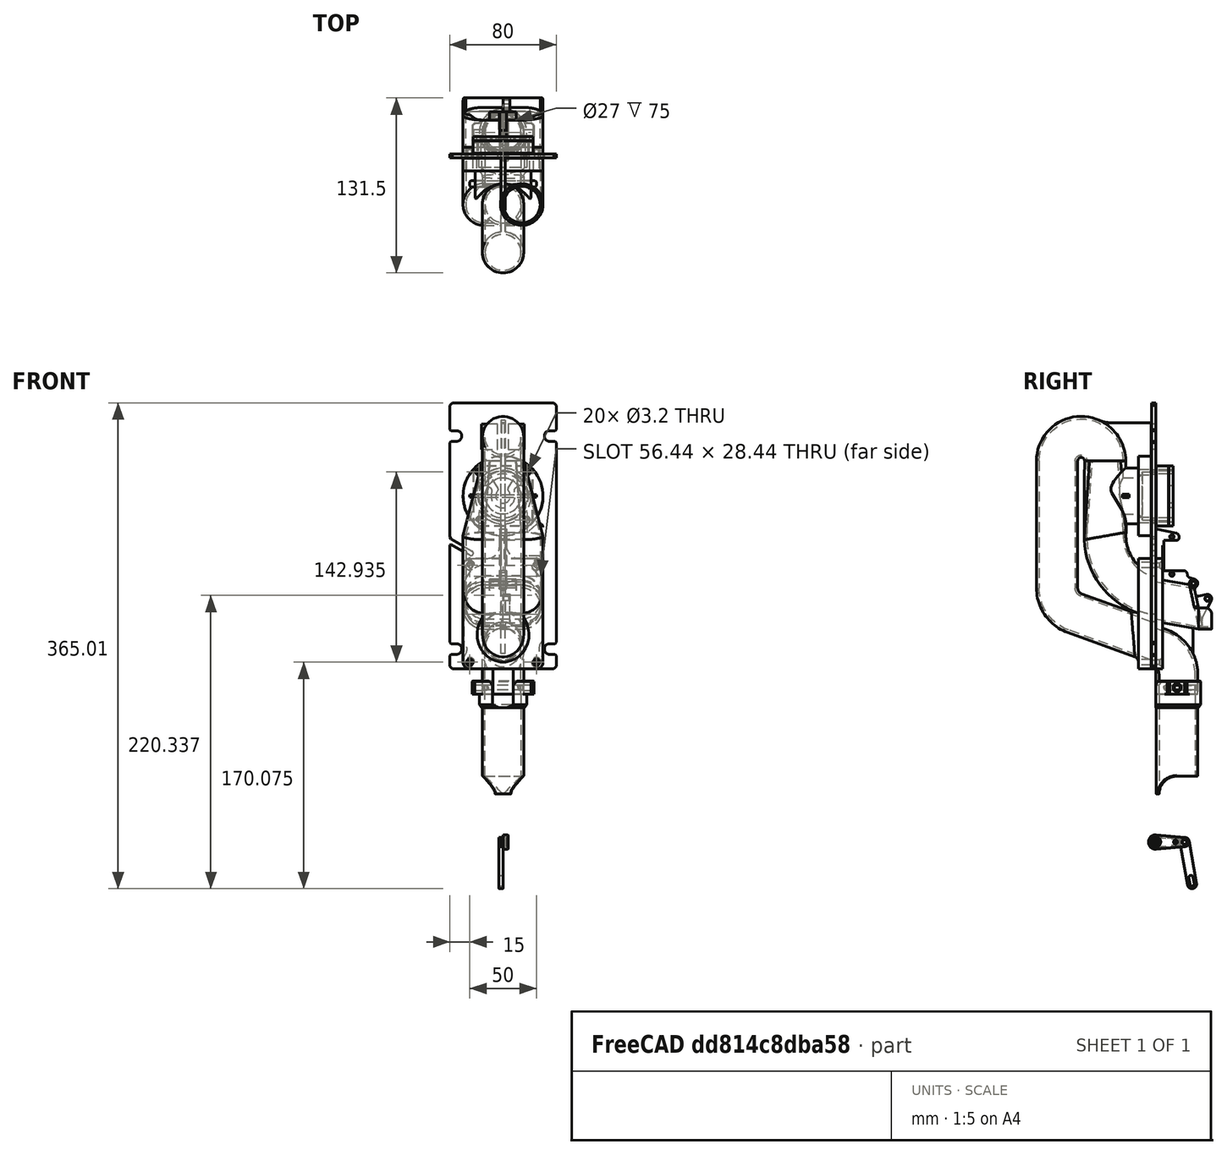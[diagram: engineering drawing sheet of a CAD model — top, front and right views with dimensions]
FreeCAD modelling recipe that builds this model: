
FCSTD DOCUMENT  (FreeCAD 2022.1128R26244 +5318 (Git))
Label: vacuum-ball
License: Creative Commons Attribution-NoDerivatives
LicenseURL: http://creativecommons.org/licenses/by-nd/4.0/
objects: Sketcher::SketchObject×58, PartDesign::Pad×27, PartDesign::Pocket×26, PartDesign::Chamfer×20, PartDesign::Fillet×20, PartDesign::Body×11, PartDesign::SubShapeBinder×9, PartDesign::SubtractivePipe×5, Part::SubShapeBinder×4, PartDesign::AdditivePipe×4, TechDraw::DrawSVGTemplate×4, TechDraw::DrawProjGroupItem×4, TechDraw::DrawProjGroup×4, TechDraw::DrawPage×4, App::Part×3, App::DocumentObjectGroup×2, PartDesign::AdditiveLoft×1, PartDesign::Line×1, PartDesign::Groove×1, PartDesign::Plane×1, +2 more types
note: 454 computed .brp shape members not serialized (recipe doc carries the construction recipe); baked Part::Feature solids carry a one-line shape summary decoded from their .brp
EXTERNAL_REF file=../table.FCStd obj=Group

FEATURE [Sketcher::SketchObject] Sketch038
  ArcFitTolerance = 1e-06
  AttachmentSupport = -> [XZ_Plane005]
  ExternalBSplineMaxDegree = 5
  ExternalBSplineTolerance = 0.0001
  FullyConstrained = true
  InternalTolerance = 1e-06
  MakeInternals = true
  MapMode = 5
  Placement = pos=(0,0,0) rot=(1,0,0;1.5708rad)
  Support = -> [XZ_Plane005]
  TreeRank = 208
  sketch-geometry (5):
    g0: LineSegment StartX=-40 StartY=130 StartZ=0 EndX=-40 EndY=330 EndZ=0
    g1: LineSegment StartX=-40 StartY=330 StartZ=0 EndX=40 EndY=330 EndZ=0
    g2: LineSegment StartX=40 StartY=330 StartZ=0 EndX=40 EndY=130 EndZ=0
    g3: LineSegment StartX=40 StartY=130 StartZ=0 EndX=-40 EndY=130 EndZ=0
    g4: GeomPoint [constr] X=2.444e-12 Y=230 Z=0
  constraints (13):
    c: Coincident(g0,g1)
    c: Coincident(g1,g2)
    c: Coincident(g2,g3)
    c: Coincident(g3,g0)
    c: Horizontal(g1)
    c: Horizontal(g3)
    c: Vertical(g0)
    c: Vertical(g2)
    c: Symmetric(g1,g0,g4)
    c: PointOnObject(g4,g-2)
    c: DistanceX(g1,g1) = 80
    c: DistanceY(g0,g0) = 200
    c: DistanceY(g-1,g0) = 130
FEATURE [PartDesign::Pad] Pad010
  AddSubType = 0
  AlongSketchNormal = false
  AutoTaperInnerAngle = true
  CheckUpToFaceLimits = true
  ClaimChildren = false
  Direction = (0,-1,2e-16)
  Fit = 0
  FitJoin = 0
  InnerFit = 0
  InnerFitJoin = 0
  Length = 3
  Length2 = 100
  Linearize = true
  NewSolid = false
  Profile = -> Sketch038
  Refine = true
  Suppress = false
  TaperInnerAngle = 0
  TaperInnerAngleRev = 0
  TreeRank = 209
  Type = 0
  _ProfileBasedVersion = 1
FEATURE [Sketcher::SketchObject] Sketch039
  ArcFitTolerance = 1e-06
  AttachmentSupport = -> [XZ_Plane005]
  ExternalBSplineMaxDegree = 5
  ExternalBSplineTolerance = 0.0001
  ExternalGeometry = -> [Pad010]
  FullyConstrained = true
  InternalTolerance = 1e-06
  MakeInternals = true
  MapMode = 5
  Placement = pos=(0,0,0) rot=(1,0,0;1.5708rad)
  Support = -> [XZ_Plane005]
  TreeRank = 211
  sketch-geometry (16):
    g0: ArcOfCircle CenterX=40 CenterY=305 CenterZ=0 NormalX=0 NormalY=0 NormalZ=1 AngleXU=0 Radius=4 StartAngle=4.71239 EndAngle=7.85398
    g1: ArcOfCircle CenterX=35 CenterY=305 CenterZ=0 NormalX=0 NormalY=0 NormalZ=1 AngleXU=0 Radius=4 StartAngle=1.5708 EndAngle=4.71239
    g2: LineSegment StartX=40 StartY=309 StartZ=0 EndX=35 EndY=309 EndZ=0
    g3: LineSegment StartX=35 StartY=301 StartZ=0 EndX=40 EndY=301 EndZ=0
    g4: ArcOfCircle CenterX=-40 CenterY=305 CenterZ=0 NormalX=0 NormalY=0 NormalZ=1 AngleXU=0 Radius=4 StartAngle=1.5708 EndAngle=4.71239
    g5: ArcOfCircle CenterX=-35 CenterY=305 CenterZ=0 NormalX=0 NormalY=0 NormalZ=1 AngleXU=0 Radius=4 StartAngle=4.71239 EndAngle=7.85398
    g6: LineSegment StartX=-40 StartY=301 StartZ=0 EndX=-35 EndY=301 EndZ=0
    g7: LineSegment StartX=-35 StartY=309 StartZ=0 EndX=-40 EndY=309 EndZ=0
    g8: ArcOfCircle CenterX=-40 CenterY=145 CenterZ=0 NormalX=0 NormalY=0 NormalZ=1 AngleXU=0 Radius=4 StartAngle=1.5708 EndAngle=4.71239
    g9: ArcOfCircle CenterX=-35 CenterY=145 CenterZ=0 NormalX=0 NormalY=0 NormalZ=1 AngleXU=0 Radius=4 StartAngle=4.71239 EndAngle=7.85398
    g10: LineSegment StartX=-40 StartY=141 StartZ=0 EndX=-35 EndY=141 EndZ=0
    g11: LineSegment StartX=-35 StartY=149 StartZ=0 EndX=-40 EndY=149 EndZ=0
    g12: ArcOfCircle CenterX=40 CenterY=145 CenterZ=0 NormalX=0 NormalY=0 NormalZ=1 AngleXU=0 Radius=4 StartAngle=4.71239 EndAngle=7.85398
    g13: ArcOfCircle CenterX=35 CenterY=145 CenterZ=0 NormalX=0 NormalY=0 NormalZ=1 AngleXU=0 Radius=4 StartAngle=1.5708 EndAngle=4.71239
    g14: LineSegment StartX=40 StartY=149 StartZ=0 EndX=35 EndY=149 EndZ=0
    g15: LineSegment StartX=35 StartY=141 StartZ=0 EndX=40 EndY=141 EndZ=0
  constraints (38):
    c: Tangent(g0,g2) = -1.5708
    c: Tangent(g2,g1) = -1.5708
    c: Tangent(g1,g3) = -1.5708
    c: Tangent(g3,g0) = -1.5708
    c: Equal(g0,g1)
    c: PointOnObject(g0,g-4)
    c: Tangent(g4,g6) = -1.5708
    c: Tangent(g6,g5) = -1.5708
    c: Tangent(g5,g7) = -1.5708
    c: Tangent(g7,g4) = -1.5708
    c: Equal(g4,g5)
    c: PointOnObject(g4,g-3)
    c: Tangent(g8,g10) = -1.5708
    c: Tangent(g10,g9) = -1.5708
    c: Tangent(g9,g11) = -1.5708
    c: Tangent(g11,g8) = -1.5708
    c: Equal(g8,g9)
    c: PointOnObject(g8,g-3)
    c: Tangent(g12,g14) = -1.5708
    c: Tangent(g14,g13) = -1.5708
    c: Tangent(g13,g15) = -1.5708
    c: Tangent(g15,g12) = -1.5708
    c: Equal(g12,g13)
    c: PointOnObject(g12,g-4)
    c: Horizontal(g14)
    c: Horizontal(g11)
    c: Horizontal(g3)
    c: Horizontal(g6)
    c: Equal(g5,g1)
    c: Equal(g5,g9)
    c: Equal(g5,g13)
    c: Radius(g5) = 4
    c: Equal(g14,g3)
    c: DistanceX(g2,g2) = 5
    c: Symmetric(g5,g1,g-2)
    c: Symmetric(g9,g13,g-2)
    c: DistanceY(g-4,g12) = 15
    c: DistanceY(g1,g-4) = 25
FEATURE [PartDesign::Pocket] Pocket012
  AddSubType = 1
  AutoTaperInnerAngle = true
  BaseFeature = -> Pad010
  CheckUpToFaceLimits = true
  ClaimChildren = false
  Fit = 0
  FitJoin = 0
  InnerFit = 0
  InnerFitJoin = 0
  Length = 5
  Length2 = 100
  Linearize = true
  NewSolid = false
  Profile = -> Sketch039
  Refine = true
  Reversed = true
  Suppress = false
  TaperInnerAngle = 0
  TaperInnerAngleRev = 0
  TreeRank = 212
  Type = 1
  _ProfileBasedVersion = 1
  _Version = 1
FEATURE [PartDesign::Chamfer] Chamfer009
  AddSubType = 0
  Angle = 45
  Base = -> Pocket012 [Edge54,Edge53,Edge44,Edge4]
  BaseFeature = -> Pocket012
  ChamferType = 0
  FlipDirection = false
  NewSolid = false
  Refine = true
  Size = 2
  Size2 = 1
  SupportTransform = false
  Suppress = false
  TreeRank = 213
FEATURE [PartDesign::Chamfer] Chamfer010
  AddSubType = 0
  Angle = 45
  Base = -> Chamfer009 [Edge3,Edge60,Edge55,Edge59,Edge61,Edge67,Edge62,Edge68]
  BaseFeature = -> Chamfer009
  ChamferType = 0
  FlipDirection = false
  NewSolid = false
  Refine = true
  Size = 1
  Size2 = 1
  SupportTransform = false
  Suppress = false
  TreeRank = 214
FEATURE [Part::SubShapeBinder] Import001  label="Import001(Chamfer010)"
  BindCopyOnChange = 0
  BindMode = 0
  ClaimChildren = false
  Context = -> <external ../table.FCStd>#Group [Link.Group002.Link017.Body006.Import001.]
  EdgeTolerance = 1e-06
  FillStyle = 0
  Fuse = false
  MakeFace = false
  MergeEdges = true
  OffsetFill = false
  OffsetIntersection = false
  OffsetJoinType = 0
  OffsetOpenResult = false
  Outline = false
  PartialLoad = false
  Relative = true
  SplitEdges = false
  Support = -> [Chamfer010]
  TightBound = false
  TreeRank = 226
  _Version = 8
FEATURE [Sketcher::SketchObject] Sketch040  label="Parcours"
  ArcFitTolerance = 1e-06
  AttachmentSupport = -> [YZ_Plane006]
  ExternalBSplineMaxDegree = 5
  ExternalBSplineTolerance = 0.0001
  ExternalGeometry = -> [Import001]
  FullyConstrained = true
  InternalTolerance = 1e-06
  MakeInternals = true
  MapMode = 5
  Placement = pos=(0,0,0) rot=(0.57735,0.57735,0.57735;2.0944rad)
  Support = -> [YZ_Plane006]
  TreeRank = 228
  sketch-geometry (13):
    g0: LineSegment StartX=16 StartY=0 StartZ=0 EndX=16 EndY=130 EndZ=0
    g1: ArcOfCircle CenterX=-4 CenterY=130 CenterZ=0 NormalX=0 NormalY=0 NormalZ=1 AngleXU=0 Radius=20 StartAngle=-8.153e-13 EndAngle=1.22173
    g2: LineSegment StartX=2.8404 StartY=148.794 StartZ=0 EndX=-60.8404 EndY=171.972 EndZ=0
    g3: ArcOfCircle CenterX=-54 CenterY=190.766 CenterZ=0 NormalX=0 NormalY=0 NormalZ=1 AngleXU=0 Radius=20 StartAngle=3.14159 EndAngle=4.36332
    g4: LineSegment StartX=-74 StartY=190.766 StartZ=0 EndX=-74 EndY=286.27 EndZ=0
    g5: ArcOfCircle CenterX=-56 CenterY=286.27 CenterZ=0 NormalX=0 NormalY=0 NormalZ=1 AngleXU=0 Radius=18 StartAngle=2.075e-13 EndAngle=3.14159
    g6: LineSegment StartX=-38 StartY=286.27 StartZ=0 EndX=-38 EndY=229.911 EndZ=0
    g7: ArcOfCircle CenterX=7.98526 CenterY=229.911 CenterZ=0 NormalX=0 NormalY=0 NormalZ=1 AngleXU=0 Radius=45.9853 StartAngle=3.14159 EndAngle=4.53786
    g8: LineSegment [constr] StartX=-90 StartY=0 StartZ=0 EndX=-90 EndY=300 EndZ=0
    g9: LineSegment [constr] StartX=-8.4e-15 StartY=130 StartZ=0 EndX=-90 EndY=130 EndZ=0
    g10: LineSegment [constr] StartX=-18.6874 StartY=156.629 StartZ=0 EndX=-7.74272 EndY=186.699 EndZ=0
    g11: LineSegment [constr] StartX=-7.74272 StartY=186.699 StartZ=0 EndX=70 EndY=158.403 EndZ=0
    g12: LineSegment StartX=-1.65748e-11 StartY=184.625 StartZ=0 EndX=32 EndY=178.982 EndZ=0
  constraints (38):
    c: Vertical(g0)
    c: Tangent(g1,g0) = -1.5708
    c: DistanceX(g-1,g0) = 16
    c: Tangent(g2,g1) = -1.5708
    c: Tangent(g3,g2) = 1.5708
    c: Vertical(g4)
    c: Tangent(g4,g3) = 1.5708
    c: Tangent(g5,g4) = 1.5708
    c: Tangent(g7,g6) = -1.5708
    c: PointOnObject(g8,g-1)
    c: Vertical(g8)
    c: DistanceX(g8,g-1) = 90
    c: DistanceY(g8,g8) = 300
    c: DistanceX(g8,g4) = 16
    c: Coincident(g9,g-3)
    c: PointOnObject(g9,g8)
    c: Horizontal(g9)
    c: Radius(g3) = 20
    c: Radius(g5) = 18
    c: Vertical(g6)
    c: PointOnObject(g10,g2)
    c: PointOnObject(g10,g7)
    c: Perpendicular(g2,g10)
    c: Coincident(g11,g10)
    c: Tangent(g11,g7)
    c: Perpendicular(g10,g11)
    c: Distance(g10) = 32
    c: PointOnObject(g7,g-2)
    c: Radius(g1) = 20
    c: PointOnObject(g0,g9)
    c: DistanceY(g5,g-4) = 43.73
    c: Tangent(g6,g5) = 1.5708
    c: Tangent(g12,g7) = -1.5708
    c: Angle(g-2,g12) = 1.39626
    c: Angle(g2,g-2) = 1.91986
    c: DistanceX(g-1,g12) = 32
    c: PointOnObject(g0,g-1)
    c: DistanceX(g11) = 70
FEATURE [Sketcher::SketchObject] Sketch041
  ArcFitTolerance = 1e-06
  AttachmentSupport = -> [XY_Plane006]
  ExternalBSplineMaxDegree = 5
  ExternalBSplineTolerance = 0.0001
  ExternalGeometry = -> [Sketch040]
  FullyConstrained = true
  InternalTolerance = 1e-06
  MakeInternals = true
  MapMode = 5
  Support = -> [XY_Plane006]
  TreeRank = 227
  sketch-geometry (1):
    g0: Circle CenterX=3.6e-15 CenterY=16 CenterZ=0 NormalX=0 NormalY=0 NormalZ=1 AngleXU=0 Radius=15.5
  constraints (2):
    c: Coincident(g0,g-3)
    c: Diameter(g0) = 31
FEATURE [PartDesign::AdditivePipe] Pipe014
  AddSubType = 0
  AuxilleryCurvelinear = true
  AuxillerySpineTangent = false
  Binormal = (0,0,0)
  ClaimChildren = false
  Fit = 0
  FitJoin = 0
  InnerFit = 0
  InnerFitJoin = 0
  Linearize = true
  Mode = 0
  MoveProfile = false
  NewSolid = false
  Profile = -> Sketch041
  Refine = true
  RotateProfile = false
  Spine = -> Sketch040 [Edge1,Edge2,Edge3,Edge4,?Edge5,?Edge6]
  SpineTangent = false
  Suppress = false
  Transformation = 0
  Transition = 1
  TreeRank = 229
  _ProfileBasedVersion = 2
FEATURE [Sketcher::SketchObject] Sketch042
  ArcFitTolerance = 1e-06
  AttachmentSupport = -> [XZ_Plane006]
  ExternalBSplineMaxDegree = 5
  ExternalBSplineTolerance = 0.0001
  ExternalGeometry = -> [Sketch040]
  FullyConstrained = true
  InternalTolerance = 1e-06
  MakeInternals = true
  MapMode = 5
  Placement = pos=(0,0,0) rot=(1,0,0;1.5708rad)
  Support = -> [XZ_Plane006]
  TreeRank = 237
  sketch-geometry (13):
    g0: LineSegment [constr] StartX=-30 StartY=200.625 StartZ=0 EndX=-30 EndY=168.625 EndZ=0
    g1: LineSegment [constr] StartX=-30 StartY=168.625 StartZ=0 EndX=30 EndY=168.625 EndZ=0
    g2: LineSegment [constr] StartX=30 StartY=168.625 StartZ=0 EndX=30 EndY=200.625 EndZ=0
    g3: LineSegment [constr] StartX=30 StartY=200.625 StartZ=0 EndX=-30 EndY=200.625 EndZ=0
    g4: GeomPoint X=-4.1e-14 Y=184.625 Z=0
    g5: ArcOfCircle CenterX=-14 CenterY=184.625 CenterZ=0 NormalX=0 NormalY=0 NormalZ=1 AngleXU=0 Radius=16 StartAngle=1.5708 EndAngle=4.71239
    g6: ArcOfCircle CenterX=14 CenterY=184.625 CenterZ=0 NormalX=0 NormalY=0 NormalZ=1 AngleXU=0 Radius=16 StartAngle=4.71239 EndAngle=7.85398
    g7: LineSegment StartX=-14 StartY=168.625 StartZ=0 EndX=14 EndY=168.625 EndZ=0
    g8: LineSegment StartX=14 StartY=200.625 StartZ=0 EndX=-14 EndY=200.625 EndZ=0
    g9: ArcOfCircle CenterX=-14 CenterY=184.625 CenterZ=0 NormalX=0 NormalY=0 NormalZ=1 AngleXU=0 Radius=14 StartAngle=1.5708 EndAngle=4.71239
    g10: ArcOfCircle CenterX=14 CenterY=184.625 CenterZ=0 NormalX=0 NormalY=0 NormalZ=1 AngleXU=0 Radius=14 StartAngle=4.71239 EndAngle=7.85398
    g11: LineSegment StartX=-14 StartY=170.625 StartZ=0 EndX=14 EndY=170.625 EndZ=0
    g12: LineSegment StartX=14 StartY=198.625 StartZ=0 EndX=-14 EndY=198.625 EndZ=0
  constraints (29):
    c: Coincident(g0,g1)
    c: Coincident(g1,g2)
    c: Coincident(g2,g3)
    c: Coincident(g3,g0)
    c: Horizontal(g1)
    c: Horizontal(g3)
    c: Vertical(g0)
    c: Vertical(g2)
    c: Symmetric(g1,g0,g4)
    c: Coincident(g4,g-3)
    c: DistanceX(g3,g3) = 60
    c: DistanceY(g2,g2) = 32
    c: Tangent(g5,g7) = -1.5708
    c: Tangent(g7,g6) = -1.5708
    c: Tangent(g6,g8) = -1.5708
    c: Tangent(g8,g5) = -1.5708
    c: Equal(g5,g6)
    c: PointOnObject(g5,g1)
    c: Tangent(g8,g3)
    c: Tangent(g5,g0)
    c: Tangent(g6,g2)
    c: Tangent(g9,g11) = -1.5708
    c: Tangent(g11,g10) = -1.5708
    c: Tangent(g10,g12) = -1.5708
    c: Tangent(g12,g9) = -1.5708
    c: Equal(g9,g10)
    c: Coincident(g10,g6)
    c: Coincident(g9,g5)
    c: DistanceY(g9,g5) = 2
FEATURE [Sketcher::SketchObject] Sketch044
  ArcFitTolerance = 1e-06
  AttachmentSupport = -> [XY_Plane006]
  ExternalBSplineMaxDegree = 5
  ExternalBSplineTolerance = 0.0001
  FullyConstrained = true
  InternalTolerance = 1e-06
  MakeInternals = true
  MapMode = 5
  Support = -> [XY_Plane006]
  TreeRank = 238
  sketch-geometry (1):
    g0: Circle CenterX=3.6e-15 CenterY=16 CenterZ=0 NormalX=0 NormalY=0 NormalZ=1 AngleXU=0 Radius=13.5
  constraints (3):
    c: Diameter(g0) = 27
    c: DistanceY(g-1,g0) = 16
    c: PointOnObject(g0,g-2)
FEATURE [PartDesign::SubtractivePipe] Pipe015
  AddSubType = 1
  AuxilleryCurvelinear = true
  AuxillerySpineTangent = false
  BaseFeature = -> Pipe014
  Binormal = (0,0,0)
  ClaimChildren = false
  Fit = 0
  FitJoin = 0
  InnerFit = 0
  InnerFitJoin = 0
  Linearize = true
  Mode = 0
  MoveProfile = false
  NewSolid = false
  Profile = -> Sketch044
  Refine = true
  RotateProfile = false
  Spine = -> Sketch040 [Edge9,Edge1,Edge2,Edge3,Edge4,Edge5,Edge6,Edge7,Edge8]
  SpineTangent = false
  Suppress = false
  Transformation = 0
  Transition = 1
  TreeRank = 239
  _ProfileBasedVersion = 2
FEATURE [PartDesign::AdditivePipe] Pipe016
  AddSubType = 0
  AuxilleryCurvelinear = true
  AuxillerySpineTangent = false
  BaseFeature = -> Pipe015
  Binormal = (0,0,0)
  ClaimChildren = false
  Fit = 0
  FitJoin = 0
  InnerFit = 0
  InnerFitJoin = 0
  Linearize = true
  Mode = 0
  MoveProfile = false
  NewSolid = false
  Profile = -> Sketch042
  Refine = true
  RotateProfile = false
  Spine = -> Sketch040 [Edge8,Edge9]
  SpineTangent = false
  Suppress = false
  Transformation = 0
  Transition = 1
  TreeRank = 240
  _ProfileBasedVersion = 2
FEATURE [PartDesign::AdditiveLoft] Loft
  AddSubType = 0
  BaseFeature = -> Pipe016
  ClaimChildren = false
  Closed = false
  Fit = 0
  FitJoin = 0
  InnerFit = 0
  InnerFitJoin = 0
  Linearize = true
  NewSolid = false
  Profile = -> Pipe016 [Face23]
  Refine = true
  Ruled = false
  Sections = -> [Pipe016]
  SplitProfile = false
  Suppress = false
  TreeRank = 241
  _ProfileBasedVersion = 1
FEATURE [Sketcher::SketchObject] Sketch045
  ArcFitTolerance = 1e-06
  AttachmentOffset = pos=(0,0,-3) rot=(0,0,1;0rad)
  AttachmentSupport = -> [XZ_Plane006]
  ExternalBSplineMaxDegree = 5
  ExternalBSplineTolerance = 0.0001
  FullyConstrained = true
  InternalTolerance = 1e-06
  MakeInternals = true
  MapMode = 5
  Placement = pos=(0,-3,-7e-16) rot=(0,0.707107,0.707107;3.14159rad)
  Support = -> [XZ_Plane006]
  TreeRank = 242
  sketch-geometry (1):
    g0: Circle CenterX=0 CenterY=260 CenterZ=0 NormalX=0 NormalY=0 NormalZ=1 AngleXU=0 Radius=21
  constraints (3):
    c: PointOnObject(g0,g-2)
    c: Diameter(g0) = 42
    c: DistanceY(g0) = 260
FEATURE [PartDesign::Pad] Pad011
  AddSubType = 0
  AlongSketchNormal = false
  AutoTaperInnerAngle = true
  BaseFeature = -> Loft
  CheckUpToFaceLimits = false
  ClaimChildren = false
  Direction = (1e-16,1,2e-16)
  Fit = 0
  FitJoin = 0
  InnerFit = 0
  InnerFitJoin = 0
  Length = 10
  Length2 = 100
  Linearize = true
  NewSolid = false
  Profile = -> Sketch045
  Refine = true
  Suppress = false
  TaperInnerAngle = 0
  TaperInnerAngleRev = 0
  TreeRank = 243
  Type = 3
  UpToFace = -> Loft [Face16]
  _ProfileBasedVersion = 1
FEATURE [Sketcher::SketchObject] Sketch046
  ArcFitTolerance = 1e-06
  AttachmentSupport = -> [Pad011]
  ExternalBSplineMaxDegree = 5
  ExternalBSplineTolerance = 0.0001
  ExternalGeometry = -> [Pad011]
  FullyConstrained = true
  InternalTolerance = 1e-06
  MakeInternals = true
  MapMode = 5
  Placement = pos=(-3e-16,-3,-7e-16) rot=(0,0.707107,0.707107;3.14159rad)
  Support = -> [Pad011]
  TreeRank = 245
  sketch-geometry (1):
    g0: Circle CenterX=0 CenterY=260 CenterZ=0 NormalX=0 NormalY=0 NormalZ=1 AngleXU=0 Radius=13.5
  constraints (2):
    c: Diameter(g0) = 27
    c: Coincident(g0,g-3)
FEATURE [Sketcher::SketchObject] Sketch047
  ArcFitTolerance = 1e-06
  AttachmentSupport = -> [Pad011]
  ExternalBSplineMaxDegree = 5
  ExternalBSplineTolerance = 0.0001
  ExternalGeometry = -> [Pad011]
  FullyConstrained = true
  InternalTolerance = 1e-06
  MakeInternals = true
  MapMode = 5
  Placement = pos=(-3e-16,-3,-7e-16) rot=(0,0.707107,0.707107;3.14159rad)
  Support = -> [Pad011]
  TreeRank = 247
  sketch-geometry (1):
    g0: Circle CenterX=0 CenterY=260 CenterZ=0 NormalX=0 NormalY=0 NormalZ=1 AngleXU=0 Radius=18.25
  constraints (2):
    c: Diameter(g0) = 36.5
    c: Coincident(g0,g-3)
FEATURE [PartDesign::Pocket] Pocket013
  AddSubType = 1
  AutoTaperInnerAngle = true
  BaseFeature = -> Pad011
  CheckUpToFaceLimits = true
  ClaimChildren = false
  Fit = 0
  FitJoin = 0
  InnerFit = 0
  InnerFitJoin = 0
  Length = 33
  Length2 = 100
  Linearize = true
  NewSolid = false
  Profile = -> Sketch046
  Refine = true
  Suppress = false
  TaperInnerAngle = 0
  TaperInnerAngleRev = 0
  TreeRank = 248
  Type = 0
  _ProfileBasedVersion = 1
  _Version = 1
FEATURE [PartDesign::Pocket] Pocket014
  AddSubType = 1
  AutoTaperInnerAngle = true
  BaseFeature = -> Pocket013
  CheckUpToFaceLimits = true
  ClaimChildren = false
  Fit = 0
  FitJoin = 0
  InnerFit = 0
  InnerFitJoin = 0
  Length = 7
  Length2 = 100
  Linearize = true
  NewSolid = false
  Profile = -> Sketch047
  Refine = true
  Suppress = false
  TaperInnerAngle = 0
  TaperInnerAngleRev = 0
  TreeRank = 249
  Type = 0
  _ProfileBasedVersion = 1
  _Version = 1
FEATURE [Sketcher::SketchObject] Sketch048
  ArcFitTolerance = 1e-06
  AttachmentSupport = -> [YZ_Plane006]
  ExternalBSplineMaxDegree = 5
  ExternalBSplineTolerance = 0.0001
  ExternalGeometry = -> [Pocket014]
  FullyConstrained = true
  InternalTolerance = 1e-06
  MakeInternals = true
  MapMode = 5
  Placement = pos=(0,0,0) rot=(0.57735,0.57735,0.57735;2.0944rad)
  Support = -> [YZ_Plane006]
  TreeRank = 250
  sketch-geometry (7):
    g0: LineSegment StartX=-21.15 StartY=257.254 StartZ=0 EndX=-20 EndY=259.246 EndZ=0
    g1: LineSegment StartX=-20 StartY=259.246 StartZ=0 EndX=-26.0622 EndY=262.746 EndZ=0
    g2: LineSegment StartX=-26.0622 StartY=262.746 StartZ=0 EndX=-27.2122 EndY=260.754 EndZ=0
    g3: LineSegment StartX=-27.2122 StartY=260.754 StartZ=0 EndX=-21.15 EndY=257.254 EndZ=0
    g4: GeomPoint [constr] X=-23.6061 Y=260 Z=0
    g5: LineSegment [constr] StartX=-27.2122 StartY=260.754 StartZ=0 EndX=-20 EndY=259.246 EndZ=0
    g6: LineSegment [constr] StartX=-23.6061 StartY=260 StartZ=0 EndX=-3 EndY=260 EndZ=0
  constraints (17):
    c: Coincident(g0,g1)
    c: Coincident(g1,g2)
    c: Coincident(g2,g3)
    c: Coincident(g3,g0)
    c: Parallel(g0,g2)
    c: Parallel(g1,g3)
    c: Perpendicular(g1,g0)
    c: Distance(g2) = 2.3
    c: Angle(g1,g-2) = 2.0944
    c: Coincident(g5,g2)
    c: Coincident(g5,g0)
    c: Symmetric(g2,g0,g4)
    c: Coincident(g6,g4)
    c: Horizontal(g6)
    c: Symmetric(g-3,g-3,g6)
    c: Distance(g3) = 7
    c: DistanceX(g0,g-4) = 10
FEATURE [PartDesign::Pocket] Pocket015
  AddSubType = 1
  AutoTaperInnerAngle = true
  BaseFeature = -> Pocket014
  CheckUpToFaceLimits = true
  ClaimChildren = false
  Fit = 0
  FitJoin = 0
  InnerFit = 0
  InnerFitJoin = 0
  Length = 5
  Length2 = 100
  Linearize = true
  Midplane = true
  NewSolid = false
  Profile = -> Sketch048
  Refine = true
  Suppress = false
  TaperInnerAngle = 0
  TaperInnerAngleRev = 0
  TreeRank = 251
  Type = 0
  _ProfileBasedVersion = 1
  _Version = 1
FEATURE [Sketcher::SketchObject] Sketch049
  ArcFitTolerance = 1e-06
  AttachmentSupport = -> [Pocket015]
  ExternalBSplineMaxDegree = 5
  ExternalBSplineTolerance = 0.0001
  FullyConstrained = true
  InternalTolerance = 1e-06
  MakeInternals = true
  MapMode = 5
  Placement = pos=(-3e-16,-3,-7e-16) rot=(0,0.707107,0.707107;3.14159rad)
  Support = -> [Pocket015]
  TreeRank = 252
  sketch-geometry (2):
    g0: Circle CenterX=0 CenterY=260 CenterZ=0 NormalX=0 NormalY=0 NormalZ=1 AngleXU=0 Radius=20
    g1: Circle CenterX=0 CenterY=260 CenterZ=0 NormalX=0 NormalY=0 NormalZ=1 AngleXU=0 Radius=30
  constraints (5):
    c: Coincident(g1,g0)
    c: Diameter(g1) = 60
    c: Diameter(g0) = 40
    c: DistanceY(g0) = 260
    c: PointOnObject(g0,g-2)
FEATURE [PartDesign::Pad] Pad012
  AddSubType = 0
  AlongSketchNormal = false
  AutoTaperInnerAngle = true
  BaseFeature = -> Pocket015
  CheckUpToFaceLimits = true
  ClaimChildren = false
  Direction = (1e-16,1,2e-16)
  Fit = 0
  FitJoin = 0
  InnerFit = 0
  InnerFitJoin = 0
  Length = 10
  Length2 = 100
  Linearize = true
  NewSolid = false
  Profile = -> Sketch049
  Refine = true
  Reversed = true
  Suppress = false
  TaperInnerAngle = 0
  TaperInnerAngleRev = 0
  TreeRank = 253
  Type = 0
  _ProfileBasedVersion = 1
FEATURE [Sketcher::SketchObject] Sketch050
  ArcFitTolerance = 1e-06
  AttachmentSupport = -> [XZ_Plane006]
  ExternalBSplineMaxDegree = 5
  ExternalBSplineTolerance = 0.0001
  ExternalGeometry = -> [Pad012]
  FullyConstrained = true
  InternalTolerance = 1e-06
  MakeInternals = true
  MapMode = 5
  Placement = pos=(0,0,0) rot=(0,0.707107,0.707107;3.14159rad)
  Support = -> [XZ_Plane006]
  TreeRank = 254
  sketch-geometry (9):
    g0: Circle CenterX=-18 CenterY=278 CenterZ=0 NormalX=0 NormalY=0 NormalZ=1 AngleXU=0 Radius=2.1
    g1: Circle CenterX=-18 CenterY=242 CenterZ=0 NormalX=0 NormalY=0 NormalZ=1 AngleXU=0 Radius=2.1
    g2: Circle CenterX=18 CenterY=242 CenterZ=0 NormalX=0 NormalY=0 NormalZ=1 AngleXU=0 Radius=2.1
    g3: Circle CenterX=18 CenterY=278 CenterZ=0 NormalX=0 NormalY=0 NormalZ=1 AngleXU=0 Radius=2.1
    g4: LineSegment [constr] StartX=18 StartY=278 StartZ=0 EndX=-18 EndY=278 EndZ=0
    g5: LineSegment [constr] StartX=-18 StartY=278 StartZ=0 EndX=-18 EndY=242 EndZ=0
    g6: LineSegment [constr] StartX=-18 StartY=242 StartZ=0 EndX=18 EndY=242 EndZ=0
    g7: LineSegment [constr] StartX=18 StartY=242 StartZ=0 EndX=18 EndY=278 EndZ=0
    g8: Circle [constr] CenterX=-2.0331e-12 CenterY=260 CenterZ=0 NormalX=0 NormalY=0 NormalZ=1 AngleXU=0 Radius=25.4558
  constraints (22):
    c: Equal(g3,g0)
    c: Equal(g3,g1)
    c: Equal(g3,g2)
    c: Diameter(g3) = 4.2
    c: Coincident(g4,g5)
    c: Coincident(g5,g6)
    c: Coincident(g6,g7)
    c: Coincident(g7,g4)
    c: Equal(g4,g5)
    c: Equal(g4,g6)
    c: Equal(g4,g7)
    c: PointOnObject(g4,g8)
    c: PointOnObject(g5,g8)
    c: PointOnObject(g6,g8)
    c: PointOnObject(g7,g8)
    c: Coincident(g8,g-3)
    c: Coincident(g7,g3)
    c: Horizontal(g4)
    c: Coincident(g0,g4)
    c: Coincident(g2,g6)
    c: Coincident(g1,g5)
    c: DistanceX(g-3,g3) = 18
FEATURE [PartDesign::Pocket] Pocket016
  AddSubType = 1
  AutoTaperInnerAngle = true
  BaseFeature = -> Pad012
  CheckUpToFaceLimits = true
  ClaimChildren = false
  Fit = 0
  FitJoin = 0
  InnerFit = 0
  InnerFitJoin = 0
  Length = 0
  Length2 = 100
  Linearize = true
  NewSolid = false
  Profile = -> Sketch050
  Refine = true
  Suppress = false
  TaperInnerAngle = 0
  TaperInnerAngleRev = 0
  TreeRank = 255
  Type = 3
  UpToFace = -> Pad012 [Face32]
  _ProfileBasedVersion = 1
  _Version = 1
FEATURE [Sketcher::SketchObject] Sketch051
  ArcFitTolerance = 1e-06
  AttachmentOffset = pos=(0,0,-3) rot=(0,0,1;0rad)
  AttachmentSupport = -> [XZ_Plane006]
  ExternalBSplineMaxDegree = 5
  ExternalBSplineTolerance = 0.0001
  FullyConstrained = true
  InternalTolerance = 1e-06
  MakeInternals = true
  MapMode = 5
  Placement = pos=(0,-3,-7e-16) rot=(0,0.707107,0.707107;3.14159rad)
  Support = -> [XZ_Plane006]
  TreeRank = 256
  sketch-geometry (4):
    g0: LineSegment StartX=-33.5 StartY=205 StartZ=0 EndX=33.5 EndY=205 EndZ=0
    g1: LineSegment StartX=33.5 StartY=205 StartZ=0 EndX=33.5 EndY=168 EndZ=0
    g2: LineSegment StartX=33.5 StartY=168 StartZ=0 EndX=-33.5 EndY=168 EndZ=0
    g3: LineSegment StartX=-33.5 StartY=168 StartZ=0 EndX=-33.5 EndY=205 EndZ=0
  constraints (11):
    c: Coincident(g0,g1)
    c: Coincident(g1,g2)
    c: Coincident(g2,g3)
    c: Coincident(g3,g0)
    c: Horizontal(g2)
    c: Vertical(g1)
    c: Vertical(g3)
    c: Symmetric(g0,g0,g-2)
    c: DistanceY(g2) = 168
    c: DistanceY(g-1,g0) = 205
    c: DistanceX(g0,g0) = 67
FEATURE [PartDesign::Pocket] Pocket017
  AddSubType = 1
  AutoTaperInnerAngle = true
  BaseFeature = -> Pocket016
  CheckUpToFaceLimits = true
  ClaimChildren = false
  Fit = 0
  FitJoin = 0
  InnerFit = 0
  InnerFitJoin = 0
  Length = 38
  Length2 = 100
  Linearize = true
  NewSolid = false
  Profile = -> Sketch051
  Refine = true
  Reversed = true
  Suppress = false
  TaperAngle = 10
  TaperInnerAngle = -10
  TaperInnerAngleRev = 0
  TreeRank = 257
  Type = 0
  _ProfileBasedVersion = 1
  _Version = 1
FEATURE [Sketcher::SketchObject] Sketch053
  ArcFitTolerance = 1e-06
  AttachmentSupport = -> [YZ_Plane006]
  ExternalBSplineMaxDegree = 5
  ExternalBSplineTolerance = 0.0001
  FullyConstrained = true
  InternalTolerance = 1e-06
  MakeInternals = true
  MapMode = 5
  Placement = pos=(0,0,0) rot=(0.57735,0.57735,0.57735;2.0944rad)
  Support = -> [YZ_Plane006]
  TreeRank = 259
  sketch-geometry (4):
    g0: LineSegment StartX=-13 StartY=3.13e-13 StartZ=0 EndX=-13 EndY=220 EndZ=0
    g1: LineSegment StartX=-13 StartY=220 StartZ=0 EndX=37 EndY=220 EndZ=0
    g2: LineSegment StartX=37 StartY=220 StartZ=0 EndX=37 EndY=0 EndZ=0
    g3: LineSegment StartX=37 StartY=0 StartZ=0 EndX=-13 EndY=3.13e-13 EndZ=0
  constraints (12):
    c: DistanceX(g0) = -13
    c: Vertical(g0)
    c: Coincident(g0,g1)
    c: Horizontal(g1)
    c: Coincident(g1,g2)
    c: PointOnObject(g2,g-1)
    c: Vertical(g2)
    c: Coincident(g2,g3)
    c: Coincident(g3,g0)
    c: PointOnObject(g0,g-1)
    c: DistanceY(g0,g0) = 220
    c: DistanceX(g3,g3) = 50
FEATURE [PartDesign::Pocket] Pocket018
  AddSubType = 1
  AutoTaperInnerAngle = true
  BaseFeature = -> Pocket017
  CheckUpToFaceLimits = true
  ClaimChildren = false
  Fit = 0
  FitJoin = 0
  InnerFit = 0
  InnerFitJoin = 0
  Length = 5
  Length2 = 100
  Linearize = true
  Midplane = true
  NewSolid = false
  Profile = -> Sketch053
  Refine = true
  Suppress = false
  TaperInnerAngle = 0
  TaperInnerAngleRev = 0
  TreeRank = 260
  Type = 1
  _ProfileBasedVersion = 1
  _Version = 1
FEATURE [Sketcher::SketchObject] Sketch054
  ArcFitTolerance = 1e-06
  AttachmentOffset = pos=(0,0,-13) rot=(0,0,1;0rad)
  AttachmentSupport = -> [XZ_Plane006]
  ExternalBSplineMaxDegree = 5
  ExternalBSplineTolerance = 0.0001
  FullyConstrained = false
  InternalTolerance = 1e-06
  MakeInternals = true
  MapMode = 5
  Placement = pos=(0,-13,-2.9e-15) rot=(0,0.707107,0.707107;3.14159rad)
  Support = -> [XZ_Plane006]
  TreeRank = 261
  sketch-geometry (15):
    g0: ArcOfCircle CenterX=-25 CenterY=207.978 CenterZ=0 NormalX=0 NormalY=0 NormalZ=1 AngleXU=0 Radius=5 StartAngle=1.5708 EndAngle=3.14159
    g1: LineSegment StartX=-25 StartY=212.978 StartZ=0 EndX=25 EndY=212.978 EndZ=0
    g2: ArcOfCircle CenterX=25 CenterY=207.978 CenterZ=0 NormalX=0 NormalY=0 NormalZ=1 AngleXU=0 Radius=5 StartAngle=-8.316e-12 EndAngle=1.5708
    g3: LineSegment StartX=30 StartY=207.978 StartZ=0 EndX=30 EndY=135.065 EndZ=0
    g4: ArcOfCircle CenterX=25 CenterY=135.065 CenterZ=0 NormalX=0 NormalY=0 NormalZ=1 AngleXU=0 Radius=5 StartAngle=4.71239 EndAngle=6.28319
    g5: LineSegment StartX=25 StartY=130.065 StartZ=0 EndX=-25 EndY=130.065 EndZ=0
    g6: ArcOfCircle CenterX=-25 CenterY=135.065 CenterZ=0 NormalX=0 NormalY=0 NormalZ=1 AngleXU=0 Radius=5 StartAngle=3.14159 EndAngle=4.71239
    g7: LineSegment StartX=-30 StartY=135.065 StartZ=0 EndX=-30 EndY=207.978 EndZ=0
    g8: GeomPoint [constr] X=-30 Y=212.978 Z=0
    g9: GeomPoint [constr] X=30 Y=130.065 Z=0
    g10: Circle CenterX=-25 CenterY=207.978 CenterZ=0 NormalX=0 NormalY=0 NormalZ=1 AngleXU=0 Radius=2.1
    g11: Circle CenterX=-25 CenterY=135.065 CenterZ=0 NormalX=0 NormalY=0 NormalZ=1 AngleXU=0 Radius=2.1
    g12: Circle CenterX=25 CenterY=135.065 CenterZ=0 NormalX=0 NormalY=0 NormalZ=1 AngleXU=0 Radius=2.1
    g13: Circle CenterX=25 CenterY=207.978 CenterZ=0 NormalX=0 NormalY=0 NormalZ=1 AngleXU=0 Radius=2.1
    g14: GeomPoint [constr] X=0 Y=138.065 Z=0
  constraints (31):
    c: Tangent(g0,g1) = 1.5708
    c: Tangent(g1,g2) = 1.5708
    c: Tangent(g2,g3) = 1.5708
    c: Tangent(g3,g4) = 1.5708
    c: Tangent(g4,g5) = 1.5708
    c: Tangent(g5,g6) = 1.5708
    c: Tangent(g6,g7) = 1.5708
    c: Tangent(g7,g0) = 1.5708
    c: Horizontal(g5)
    c: Vertical(g3)
    c: Vertical(g7)
    c: Equal(g0,g2)
    c: Equal(g2,g4)
    c: Equal(g4,g6)
    c: PointOnObject(g8,g1)
    c: PointOnObject(g8,g7)
    c: PointOnObject(g9,g3)
    c: PointOnObject(g9,g5)
    c: Symmetric(g0,g1,g-2)
    c: Coincident(g10,g0)
    c: Coincident(g11,g6)
    c: Coincident(g12,g4)
    c: Coincident(g13,g2)
    c: Equal(g13,g12)
    c: Equal(g13,g11)
    c: Equal(g13,g10)
    c: Diameter(g13) = 4.2
    c: Radius(g2) = 5
    c: DistanceX(g0,g2) = 60
    c: PointOnObject(g14,g-2)
    c: DistanceY(g4,g14) = 8
FEATURE [PartDesign::Pad] Pad013
  AddSubType = 0
  AlongSketchNormal = false
  AutoTaperInnerAngle = true
  BaseFeature = -> Pocket018
  CheckUpToFaceLimits = true
  ClaimChildren = false
  Direction = (1e-16,1,2e-16)
  Fit = 0
  FitJoin = 0
  InnerFit = 0
  InnerFitJoin = 0
  Length = 10
  Length2 = 100
  Linearize = true
  NewSolid = false
  Profile = -> Sketch054
  Refine = true
  Suppress = false
  TaperInnerAngle = 0
  TaperInnerAngleRev = 0
  TreeRank = 262
  Type = 0
  _ProfileBasedVersion = 1
FEATURE [PartDesign::SubtractivePipe] Pipe017
  AddSubType = 1
  AuxilleryCurvelinear = true
  AuxillerySpineTangent = false
  BaseFeature = -> Pad013
  Binormal = (0,0,0)
  ClaimChildren = false
  Fit = 0
  FitJoin = 0
  InnerFit = 0
  InnerFitJoin = 0
  Linearize = true
  Mode = 0
  MoveProfile = false
  NewSolid = false
  Profile = -> Sketch044
  Refine = true
  RotateProfile = false
  Spine = -> Sketch040 [Edge1,Edge2,Edge3]
  SpineTangent = false
  Suppress = false
  Transformation = 0
  Transition = 1
  TreeRank = 263
  _ProfileBasedVersion = 2
FEATURE [PartDesign::SubtractivePipe] Pipe018
  AddSubType = 1
  AuxilleryCurvelinear = true
  AuxillerySpineTangent = false
  BaseFeature = -> Pipe017
  Binormal = (0,0,0)
  ClaimChildren = false
  Fit = 0
  FitJoin = 0
  InnerFit = 0
  InnerFitJoin = 0
  Linearize = true
  Mode = 0
  MoveProfile = false
  NewSolid = false
  Profile = -> Sketch042 [InternalFace2]
  Refine = true
  RotateProfile = false
  Spine = -> Sketch040 [Edge9,Edge8]
  SpineTangent = false
  Suppress = false
  Transformation = 0
  Transition = 1
  TreeRank = 264
  _ProfileBasedVersion = 2
FEATURE [Sketcher::SketchObject] Sketch055
  ArcFitTolerance = 1e-06
  AttachmentSupport = -> [YZ_Plane006]
  ExternalBSplineMaxDegree = 5
  ExternalBSplineTolerance = 0.0001
  ExternalGeometry = -> [Sketch040,Pipe018]
  FullyConstrained = true
  InternalTolerance = 1e-06
  MakeInternals = true
  MapMode = 5
  Placement = pos=(0,0,0) rot=(0.57735,0.57735,0.57735;2.0944rad)
  Support = -> [YZ_Plane006]
  TreeRank = 265
  sketch-geometry (7):
    g0: LineSegment StartX=-3 StartY=166.35 StartZ=0 EndX=-55.8811 EndY=185.597 EndZ=0
    g1: LineSegment StartX=-59.5 StartY=190.766 StartZ=0 EndX=-59.5 EndY=286.27 EndZ=0
    g2: LineSegment StartX=-52.5 StartY=286.27 StartZ=0 EndX=-52.5 EndY=229.911 EndZ=0
    g3: ArcOfCircle CenterX=-56 CenterY=286.27 CenterZ=0 NormalX=0 NormalY=0 NormalZ=1 AngleXU=0 Radius=3.5 StartAngle=-8.642e-13 EndAngle=3.14159
    g4: ArcOfCircle CenterX=-54 CenterY=190.766 CenterZ=0 NormalX=0 NormalY=0 NormalZ=1 AngleXU=0 Radius=5.5 StartAngle=3.14159 EndAngle=4.36332
    g5: ArcOfCircle CenterX=7.98526 CenterY=229.911 CenterZ=0 NormalX=0 NormalY=0 NormalZ=1 AngleXU=0 Radius=60.4853 StartAngle=3.14159 EndAngle=4.52976
    g6: LineSegment StartX=-3 StartY=170.432 StartZ=0 EndX=-3 EndY=166.35 EndZ=0
  constraints (16):
    c: Vertical(g1)
    c: Vertical(g2)
    c: Coincident(g6,g5)
    c: Coincident(g0,g6)
    c: Vertical(g6)
    c: Tangent(g3,g2) = 1.5708
    c: Tangent(g3,g1) = 1.5708
    c: Tangent(g4,g1) = 1.5708
    c: Tangent(g4,g0) = 1.5708
    c: Tangent(g5,g2) = -1.5708
    c: Angle(g0,g-2) = 1.91986
    c: Coincident(g3,g-5)
    c: Coincident(g4,g-3)
    c: Coincident(g5,g-4)
    c: Radius(g3) = 3.5
    c: PointOnObject(g5,g-6)
FEATURE [PartDesign::Pad] Pad014
  AddSubType = 0
  AlongSketchNormal = false
  AutoTaperInnerAngle = true
  BaseFeature = -> Pipe018
  CheckUpToFaceLimits = true
  ClaimChildren = false
  Direction = (1,-2e-16,3e-16)
  Fit = 0
  FitJoin = 0
  InnerFit = 0
  InnerFitJoin = 0
  Length = 3
  Length2 = 100
  Linearize = true
  Midplane = true
  NewSolid = false
  Profile = -> Sketch055
  Refine = true
  Suppress = false
  TaperInnerAngle = 0
  TaperInnerAngleRev = 0
  TreeRank = 266
  Type = 0
  _ProfileBasedVersion = 1
FEATURE [Sketcher::SketchObject] Sketch056
  ArcFitTolerance = 1e-06
  AttachmentSupport = -> [YZ_Plane006]
  ExternalBSplineMaxDegree = 5
  ExternalBSplineTolerance = 0.0001
  ExternalGeometry = -> [Sketch040]
  FullyConstrained = true
  InternalTolerance = 1e-06
  MakeInternals = true
  MapMode = 5
  Placement = pos=(0,0,0) rot=(0.57735,0.57735,0.57735;2.0944rad)
  Support = -> [YZ_Plane006]
  TreeRank = 267
  sketch-geometry (4):
    g0: LineSegment StartX=-3 StartY=200.939 StartZ=0 EndX=-3 EndY=240.939 EndZ=0
    g1: LineSegment StartX=-3 StartY=240.939 StartZ=0 EndX=-23 EndY=240.939 EndZ=0
    g2: LineSegment StartX=-23 StartY=240.939 StartZ=0 EndX=-23 EndY=229.911 EndZ=0
    g3: ArcOfCircle CenterX=7.98526 CenterY=229.911 CenterZ=0 NormalX=0 NormalY=0 NormalZ=1 AngleXU=0 Radius=30.9853 StartAngle=3.14159 EndAngle=4.34998
  constraints (11):
    c: Vertical(g0)
    c: Coincident(g1,g0)
    c: Horizontal(g1)
    c: Coincident(g2,g1)
    c: Vertical(g2)
    c: Coincident(g3,g0)
    c: Coincident(g3,g-3)
    c: Tangent(g3,g2) = -1.5708
    c: DistanceX(g1,g1) = 20
    c: DistanceY(g0,g0) = 40
    c: DistanceX(g0) = -3
FEATURE [PartDesign::Pad] Pad015
  AddSubType = 0
  AlongSketchNormal = false
  AutoTaperInnerAngle = true
  BaseFeature = -> Pad014
  CheckUpToFaceLimits = true
  ClaimChildren = false
  Direction = (1,-2e-16,3e-16)
  Fit = 0
  FitJoin = 0
  InnerFit = 0
  InnerFitJoin = 0
  Length = 3
  Length2 = 100
  Linearize = true
  Midplane = true
  NewSolid = false
  Profile = -> Sketch056
  Refine = true
  Suppress = false
  TaperInnerAngle = 0
  TaperInnerAngleRev = 0
  TreeRank = 268
  Type = 0
  _ProfileBasedVersion = 1
FEATURE [Sketcher::SketchObject] Sketch057
  ArcFitTolerance = 1e-06
  AttachmentSupport = -> [YZ_Plane006]
  ExternalBSplineMaxDegree = 5
  ExternalBSplineTolerance = 0.0001
  ExternalGeometry = -> [Sketch040]
  FullyConstrained = false
  InternalTolerance = 1e-06
  MakeInternals = true
  MapMode = 5
  Placement = pos=(0,0,0) rot=(0.57735,0.57735,0.57735;2.0944rad)
  Support = -> [YZ_Plane006]
  TreeRank = 269
  sketch-geometry (5):
    g0: LineSegment StartX=-39.5437 StartY=315 StartZ=0 EndX=-3 EndY=315 EndZ=0
    g1: LineSegment StartX=-3 StartY=315 StartZ=0 EndX=-3 EndY=279 EndZ=0
    g2: LineSegment StartX=-3 StartY=279 StartZ=0 EndX=-23 EndY=279 EndZ=0
    g3: LineSegment StartX=-23 StartY=279 StartZ=0 EndX=-23 EndY=288.957 EndZ=0
    g4: ArcOfCircle CenterX=-56 CenterY=286.27 CenterZ=0 NormalX=0 NormalY=0 NormalZ=1 AngleXU=0 Radius=33.1092 StartAngle=0.0812516 EndAngle=1.05062
  constraints (14):
    c: Horizontal(g0)
    c: Coincident(g1,g0)
    c: Vertical(g1)
    c: Coincident(g2,g1)
    c: Horizontal(g2)
    c: Coincident(g3,g2)
    c: Vertical(g3)
    c: Coincident(g4,g0)
    c: Coincident(g4,g3)
    c: Coincident(g4,g-3)
    c: DistanceY(g1) = 279
    c: DistanceX(g2,g1) = 20
    c: DistanceY(g0) = 315
    c: DistanceX(g1) = -3
FEATURE [PartDesign::Pad] Pad016
  AddSubType = 0
  AlongSketchNormal = false
  AutoTaperInnerAngle = true
  BaseFeature = -> Pad015
  CheckUpToFaceLimits = true
  ClaimChildren = false
  Direction = (1,-2e-16,3e-16)
  Fit = 0
  FitJoin = 0
  InnerFit = 0
  InnerFitJoin = 0
  Length = 3
  Length2 = 100
  Linearize = true
  Midplane = true
  NewSolid = false
  Profile = -> Sketch057
  Refine = true
  Suppress = false
  TaperInnerAngle = 0
  TaperInnerAngleRev = 0
  TreeRank = 270
  Type = 0
  _ProfileBasedVersion = 1
FEATURE [PartDesign::Fillet] Fillet005
  AddSubType = 0
  Base = -> Pad016 [Edge28]
  BaseFeature = -> Pad016
  NewSolid = false
  Radius = 20
  Refine = true
  SupportTransform = false
  Suppress = false
  TreeRank = 271
FEATURE [PartDesign::Chamfer] Chamfer011
  AddSubType = 0
  Angle = 45
  Base = -> Fillet005 [Edge182,Edge136,Edge135,Edge179,Edge99,Edge100,Edge89,Edge90]
  BaseFeature = -> Fillet005
  ChamferType = 0
  FlipDirection = false
  NewSolid = false
  Refine = true
  Size = 0.4
  Size2 = 1
  SupportTransform = false
  Suppress = false
  TreeRank = 272
FEATURE [PartDesign::Fillet] Fillet006
  AddSubType = 0
  Base = -> Chamfer011 [Edge178]
  BaseFeature = -> Chamfer011
  NewSolid = false
  Radius = 4
  Refine = true
  SupportTransform = false
  Suppress = false
  TreeRank = 274
FEATURE [Sketcher::SketchObject] Sketch058
  ArcFitTolerance = 1e-06
  AttachmentSupport = -> [YZ_Plane006]
  ExternalBSplineMaxDegree = 5
  ExternalBSplineTolerance = 0.0001
  FullyConstrained = true
  InternalTolerance = 1e-06
  MakeInternals = true
  MapMode = 5
  Placement = pos=(0,0,0) rot=(0.57735,0.57735,0.57735;2.0944rad)
  Support = -> [YZ_Plane006]
  TreeRank = 276
  sketch-geometry (5):
    g0: LineSegment StartX=-25 StartY=261.15 StartZ=0 EndX=-20 EndY=261.15 EndZ=0
    g1: LineSegment StartX=-20 StartY=261.15 StartZ=0 EndX=-20 EndY=258.85 EndZ=0
    g2: LineSegment StartX=-20 StartY=258.85 StartZ=0 EndX=-25 EndY=258.85 EndZ=0
    g3: LineSegment StartX=-25 StartY=258.85 StartZ=0 EndX=-25 EndY=261.15 EndZ=0
    g4: LineSegment [constr] StartX=-25 StartY=260 StartZ=0 EndX=-20 EndY=260 EndZ=0
  constraints (15):
    c: Coincident(g0,g1)
    c: Coincident(g1,g2)
    c: Coincident(g2,g3)
    c: Coincident(g3,g0)
    c: Horizontal(g0)
    c: Horizontal(g2)
    c: Vertical(g1)
    c: Vertical(g3)
    c: PointOnObject(g4,g3)
    c: Symmetric(g1,g0,g4)
    c: DistanceY(g3,g3) = 2.3
    c: DistanceX(g0,g0) = 5
    c: DistanceY(g4) = 260
    c: DistanceX(g4) = -20
    c: Horizontal(g4)
FEATURE [PartDesign::Pocket] Pocket019
  AddSubType = 1
  AutoTaperInnerAngle = true
  BaseFeature = -> Fillet006
  CheckUpToFaceLimits = true
  ClaimChildren = false
  Fit = 0
  FitJoin = 0
  InnerFit = 0
  InnerFitJoin = 0
  Length = 5
  Length2 = 100
  Linearize = true
  Midplane = true
  NewSolid = false
  Profile = -> Sketch058
  Refine = true
  Suppress = false
  TaperInnerAngle = 0
  TaperInnerAngleRev = 0
  TreeRank = 277
  Type = 1
  _ProfileBasedVersion = 1
  _Version = 1
FEATURE [PartDesign::SubShapeBinder] Binder001  label="Binder001(Parcours)"
  BindCopyOnChange = 0
  BindMode = 0
  ClaimChildren = false
  Context = -> Part [Body.Binder001.]
  EdgeTolerance = 1e-06
  FillStyle = 0
  Fuse = false
  MakeFace = true
  MergeEdges = true
  OffsetFill = false
  OffsetIntersection = false
  OffsetJoinType = 0
  OffsetOpenResult = false
  Outline = false
  PartialLoad = false
  Relative = true
  SplitEdges = false
  Support = -> [Body006[Sketch040.]]
  TightBound = false
  TreeRank = 294
  _Version = 8
FEATURE [Sketcher::SketchObject] Sketch059  label="Externe"
  ArcFitTolerance = 1e-06
  AttachmentSupport = -> [XY_Plane]
  ExternalBSplineMaxDegree = 5
  ExternalBSplineTolerance = 0.0001
  ExternalGeometry = -> [Binder001]
  FullyConstrained = true
  InternalTolerance = 1e-06
  MakeInternals = true
  MapMode = 5
  Placement = pos=(0,0,0) rot=(0,1,0;3.14159rad)
  Support = -> [XY_Plane]
  TreeRank = 296
  sketch-geometry (1):
    g0: Circle CenterX=0 CenterY=16 CenterZ=0 NormalX=0 NormalY=0 NormalZ=1 AngleXU=0 Radius=15.5
  constraints (2):
    c: Coincident(g0,g-3)
    c: Diameter(g0) = 31
FEATURE [Sketcher::SketchObject] Sketch060  label="Interne"
  ArcFitTolerance = 1e-06
  AttachmentSupport = -> [XY_Plane]
  ExternalBSplineMaxDegree = 5
  ExternalBSplineTolerance = 0.0001
  ExternalGeometry = -> [Binder001]
  FullyConstrained = true
  InternalTolerance = 1e-06
  MakeInternals = true
  MapMode = 5
  Support = -> [XY_Plane]
  TreeRank = 297
  sketch-geometry (1):
    g0: Circle CenterX=0 CenterY=16 CenterZ=0 NormalX=0 NormalY=0 NormalZ=1 AngleXU=0 Radius=13.5
  constraints (2):
    c: Coincident(g0,g-3)
    c: Diameter(g0) = 27
FEATURE [PartDesign::AdditivePipe] Pipe
  AddSubType = 0
  AuxilleryCurvelinear = true
  AuxillerySpineTangent = false
  Binormal = (0,0,0)
  ClaimChildren = false
  Fit = 0
  FitJoin = 0
  InnerFit = 0
  InnerFitJoin = 0
  Linearize = true
  Mode = 0
  MoveProfile = false
  NewSolid = false
  Profile = -> Sketch059
  Refine = true
  RotateProfile = false
  Spine = -> Binder001 [Edge1,Edge2,Edge3]
  SpineTangent = false
  Suppress = false
  Transformation = 0
  Transition = 1
  TreeRank = 298
  _ProfileBasedVersion = 2
FEATURE [Sketcher::SketchObject] Sketch061
  ArcFitTolerance = 1e-06
  AttachmentSupport = -> [YZ_Plane]
  ExternalBSplineMaxDegree = 5
  ExternalBSplineTolerance = 0.0001
  FullyConstrained = true
  InternalTolerance = 1e-06
  MakeInternals = true
  MapMode = 5
  Placement = pos=(0,0,0) rot=(0.57735,0.57735,0.57735;2.0944rad)
  Support = -> [YZ_Plane]
  TreeRank = 299
  sketch-geometry (4):
    g0: LineSegment StartX=-3.25e-13 StartY=-5.36e-14 StartZ=0 EndX=-100 EndY=-5.36e-14 EndZ=0
    g1: LineSegment StartX=-100 StartY=-5.36e-14 StartZ=0 EndX=-100 EndY=330 EndZ=0
    g2: LineSegment StartX=-100 StartY=330 StartZ=0 EndX=-3.268e-13 EndY=330 EndZ=0
    g3: LineSegment StartX=-3.25e-13 StartY=330 StartZ=0 EndX=-3.25e-13 EndY=-5.68e-14 EndZ=0
  constraints (11):
    c: Coincident(g0,g1)
    c: Coincident(g1,g2)
    c: Coincident(g2,g3)
    c: Coincident(g3,g0)
    c: Horizontal(g0)
    c: Horizontal(g2)
    c: Vertical(g1)
    c: Vertical(g3)
    c: Coincident(g0,g-1)
    c: DistanceY(g3,g3) = 330
    c: DistanceX(g0,g0) = 100
FEATURE [PartDesign::Pocket] Pocket021
  AddSubType = 1
  AutoTaperInnerAngle = true
  BaseFeature = -> Pipe
  CheckUpToFaceLimits = true
  ClaimChildren = false
  Fit = 0
  FitJoin = 0
  InnerFit = 0
  InnerFitJoin = 0
  Length = 5
  Length2 = 100
  Linearize = true
  Midplane = true
  NewSolid = false
  Profile = -> Sketch061
  Refine = true
  Suppress = false
  TaperInnerAngle = 0
  TaperInnerAngleRev = 0
  TreeRank = 300
  Type = 1
  _ProfileBasedVersion = 1
  _Version = 1
FEATURE [Part::SubShapeBinder] Import  label="Import(Pocket020)"
  BindCopyOnChange = 0
  BindMode = 0
  ClaimChildren = false
  Context = -> Part [Body.Import.]
  EdgeTolerance = 1e-06
  FillStyle = 0
  Fuse = false
  MakeFace = false
  MergeEdges = true
  OffsetFill = false
  OffsetIntersection = false
  OffsetJoinType = 0
  OffsetOpenResult = false
  Outline = false
  PartialLoad = false
  Relative = true
  SplitEdges = false
  Support = -> [Body005[Pocket020.]]
  TightBound = false
  TreeRank = 302
  _Version = 8
FEATURE [Sketcher::SketchObject] Sketch062
  ArcFitTolerance = 1e-06
  AttachmentSupport = -> [XZ_Plane]
  ExternalBSplineMaxDegree = 5
  ExternalBSplineTolerance = 0.0001
  ExternalGeometry = -> [Import]
  FullyConstrained = true
  InternalTolerance = 1e-06
  MakeInternals = true
  MapMode = 5
  Placement = pos=(0,0,0) rot=(1,0,0;1.5708rad)
  Support = -> [XZ_Plane]
  TreeRank = 312
  sketch-geometry (5):
    g0: ArcOfCircle CenterX=-14 CenterY=181.627 CenterZ=0 NormalX=0 NormalY=0 NormalZ=1 AngleXU=0 Radius=16 StartAngle=1.5708 EndAngle=4.71239
    g1: ArcOfCircle CenterX=14 CenterY=181.627 CenterZ=0 NormalX=0 NormalY=0 NormalZ=1 AngleXU=0 Radius=16 StartAngle=4.71239 EndAngle=7.85398
    g2: LineSegment StartX=-14 StartY=165.627 StartZ=0 EndX=14 EndY=165.627 EndZ=0
    g3: LineSegment StartX=14 StartY=197.627 StartZ=0 EndX=-14 EndY=197.627 EndZ=0
    g4: LineSegment [constr] StartX=-30 StartY=181.627 StartZ=0 EndX=30 EndY=181.627 EndZ=0
  constraints (12):
    c: Tangent(g0,g2) = -1.5708
    c: Tangent(g2,g1) = -1.5708
    c: Tangent(g1,g3) = -1.5708
    c: Tangent(g3,g0) = -1.5708
    c: Equal(g0,g1)
    c: Symmetric(g1,g0,g-2)
    c: PointOnObject(g4,g0)
    c: PointOnObject(g4,g1)
    c: PointOnObject(g1,g4)
    c: DistanceY(g0,g0) = 32
    c: DistanceX(g4,g4) = 60
    c: Symmetric(g-3,g-4,g4)
FEATURE [Sketcher::SketchObject] Sketch064
  ArcFitTolerance = 1e-06
  AttachmentSupport = -> [XZ_Plane]
  ExternalBSplineMaxDegree = 5
  ExternalBSplineTolerance = 0.0001
  ExternalGeometry = -> [Import]
  FullyConstrained = true
  InternalTolerance = 1e-06
  MakeInternals = true
  MapMode = 5
  Placement = pos=(0,0,0) rot=(1,0,0;1.5708rad)
  Support = -> [XZ_Plane]
  TreeRank = 306
  sketch-geometry (14):
    g0: ArcOfCircle CenterX=-25 CenterY=207.978 CenterZ=0 NormalX=0 NormalY=0 NormalZ=1 AngleXU=0 Radius=5 StartAngle=1.5708 EndAngle=3.14159
    g1: LineSegment StartX=-25 StartY=212.978 StartZ=0 EndX=25 EndY=212.978 EndZ=0
    g2: ArcOfCircle CenterX=25 CenterY=207.978 CenterZ=0 NormalX=0 NormalY=0 NormalZ=1 AngleXU=0 Radius=5 StartAngle=1.15802e-11 EndAngle=1.5708
    g3: LineSegment StartX=30 StartY=207.978 StartZ=0 EndX=30 EndY=135.065 EndZ=0
    g4: ArcOfCircle CenterX=25 CenterY=135.065 CenterZ=0 NormalX=0 NormalY=0 NormalZ=1 AngleXU=0 Radius=5 StartAngle=4.71239 EndAngle=6.28319
    g5: LineSegment StartX=25 StartY=130.065 StartZ=0 EndX=-25 EndY=130.065 EndZ=0
    g6: ArcOfCircle CenterX=-25 CenterY=135.065 CenterZ=0 NormalX=0 NormalY=0 NormalZ=1 AngleXU=0 Radius=5 StartAngle=3.14159 EndAngle=4.71239
    g7: LineSegment StartX=-30 StartY=135.065 StartZ=0 EndX=-30 EndY=207.978 EndZ=0
    g8: GeomPoint [constr] X=-30 Y=212.978 Z=0
    g9: GeomPoint [constr] X=30 Y=130.065 Z=0
    g10: Circle CenterX=25 CenterY=207.978 CenterZ=0 NormalX=0 NormalY=0 NormalZ=1 AngleXU=0 Radius=1.6
    g11: Circle CenterX=-25 CenterY=135.065 CenterZ=0 NormalX=0 NormalY=0 NormalZ=1 AngleXU=0 Radius=1.6
    g12: Circle CenterX=25 CenterY=135.065 CenterZ=0 NormalX=0 NormalY=0 NormalZ=1 AngleXU=0 Radius=1.6
    g13: Circle CenterX=-25 CenterY=207.978 CenterZ=0 NormalX=0 NormalY=0 NormalZ=1 AngleXU=0 Radius=1.6
  constraints (29):
    c: Tangent(g0,g1) = 1.5708
    c: Tangent(g1,g2) = 1.5708
    c: Tangent(g2,g3) = 1.5708
    c: Tangent(g3,g4) = 1.5708
    c: Tangent(g4,g5) = 1.5708
    c: Tangent(g5,g6) = 1.5708
    c: Tangent(g6,g7) = 1.5708
    c: Tangent(g7,g0) = 1.5708
    c: Horizontal(g1)
    c: Horizontal(g5)
    c: Vertical(g3)
    c: Vertical(g7)
    c: Equal(g0,g2)
    c: PointOnObject(g8,g1)
    c: PointOnObject(g8,g7)
    c: PointOnObject(g9,g3)
    c: PointOnObject(g9,g5)
    c: Coincident(g-5,g6)
    c: Symmetric(g3,g6,g-2)
    c: Coincident(g2,g-3)
    c: Coincident(g10,g2)
    c: Coincident(g11,g6)
    c: Coincident(g12,g4)
    c: Coincident(g13,g0)
    c: Equal(g13,g10)
    c: Equal(g13,g12)
    c: Equal(g13,g11)
    c: Diameter(g13) = 3.2
    c: DistanceX(g0,g2) = 60
FEATURE [Sketcher::SketchObject] Sketch065
  ArcFitTolerance = 1e-06
  AttachmentSupport = -> [XY_Plane]
  ExternalBSplineMaxDegree = 5
  ExternalBSplineTolerance = 0.0001
  FullyConstrained = true
  InternalTolerance = 1e-06
  MakeInternals = true
  MapMode = 5
  Placement = pos=(0,0,0) rot=(0,1,0;3.14159rad)
  Support = -> [XY_Plane]
  TreeRank = 309
  sketch-geometry (4):
    g0: LineSegment StartX=-7.5 StartY=0 StartZ=0 EndX=7.5 EndY=0 EndZ=0
    g1: LineSegment StartX=7.5 StartY=0 StartZ=0 EndX=7.5 EndY=15 EndZ=0
    g2: LineSegment StartX=7.5 StartY=15 StartZ=0 EndX=-7.5 EndY=15 EndZ=0
    g3: LineSegment StartX=-7.5 StartY=15 StartZ=0 EndX=-7.5 EndY=0 EndZ=0
  constraints (11):
    c: Coincident(g0,g1)
    c: Coincident(g1,g2)
    c: Coincident(g2,g3)
    c: Coincident(g3,g0)
    c: Horizontal(g0)
    c: Horizontal(g2)
    c: Vertical(g1)
    c: Vertical(g3)
    c: Symmetric(g0,g0,g-1)
    c: DistanceY(g1,g1) = 15
    c: DistanceX(g2,g2) = 15
FEATURE [PartDesign::Pad] Pad
  AddSubType = 0
  AlongSketchNormal = false
  AutoTaperInnerAngle = true
  BaseFeature = -> Pocket021
  CheckUpToFaceLimits = true
  ClaimChildren = false
  Direction = (0,-1,-2e-16)
  Fit = 0
  FitJoin = 0
  InnerFit = 0
  InnerFitJoin = 0
  Length = 5
  Length2 = 100
  Linearize = true
  NewSolid = false
  Profile = -> Sketch064
  Refine = true
  Reversed = true
  Suppress = false
  TaperInnerAngle = 0
  TaperInnerAngleRev = 0
  TreeRank = 310
  Type = 0
  _ProfileBasedVersion = 1
FEATURE [PartDesign::Pad] Pad017
  AddSubType = 0
  AlongSketchNormal = false
  AutoTaperInnerAngle = true
  BaseFeature = -> Pad
  CheckUpToFaceLimits = true
  ClaimChildren = false
  Direction = (1e-16,0,-1)
  Fit = 0
  FitJoin = 0
  InnerFit = 0
  InnerFitJoin = 0
  Length = 10
  Length2 = 100
  Linearize = true
  NewSolid = false
  Profile = -> Sketch065
  Refine = true
  Reversed = true
  Suppress = false
  TaperInnerAngle = 0
  TaperInnerAngleRev = 0
  TreeRank = 311
  Type = 3
  UpToFace = -> Pad [Face6]
  _ProfileBasedVersion = 1
FEATURE [PartDesign::AdditivePipe] Pipe019
  AddSubType = 0
  AuxilleryCurvelinear = true
  AuxillerySpineTangent = false
  BaseFeature = -> Pad017
  Binormal = (0,0,0)
  ClaimChildren = false
  Fit = 0
  FitJoin = 0
  InnerFit = 0
  InnerFitJoin = 0
  Linearize = true
  Mode = 0
  MoveProfile = false
  NewSolid = false
  Profile = -> Sketch062
  Refine = true
  RotateProfile = false
  Spine = -> Binder001 [Edge9]
  SpineTangent = false
  Suppress = false
  Transformation = 0
  Transition = 1
  TreeRank = 313
  _ProfileBasedVersion = 2
FEATURE [Sketcher::SketchObject] Sketch066
  ArcFitTolerance = 1e-06
  AttachmentSupport = -> [YZ_Plane]
  ExternalBSplineMaxDegree = 5
  ExternalBSplineTolerance = 0.0001
  ExternalGeometry = -> [Pipe019]
  FullyConstrained = true
  InternalTolerance = 1e-06
  MakeInternals = true
  MapMode = 5
  Placement = pos=(0,0,0) rot=(0.57735,0.57735,0.57735;2.0944rad)
  Support = -> [YZ_Plane]
  TreeRank = 314
  sketch-geometry (4):
    g0: LineSegment StartX=28 StartY=191.985 StartZ=0 EndX=1.563e-13 EndY=191.985 EndZ=0
    g1: LineSegment StartX=1.556e-13 StartY=191.985 StartZ=0 EndX=1.556e-13 EndY=0 EndZ=0
    g2: LineSegment StartX=1.556e-13 StartY=0 StartZ=0 EndX=28 EndY=0 EndZ=0
    g3: LineSegment StartX=28 StartY=0 StartZ=0 EndX=28 EndY=191.985 EndZ=0
  constraints (11):
    c: Coincident(g0,g1)
    c: Coincident(g1,g2)
    c: Coincident(g2,g3)
    c: Coincident(g3,g0)
    c: Horizontal(g0)
    c: Horizontal(g2)
    c: Vertical(g1)
    c: Vertical(g3)
    c: DistanceX(g2,g2) = 28
    c: Horizontal(g0,g-3)
    c: Coincident(g1,g-1)
FEATURE [PartDesign::Pad] Pad018
  AddSubType = 0
  AlongSketchNormal = false
  AutoTaperInnerAngle = true
  BaseFeature = -> Pipe019
  CheckUpToFaceLimits = true
  ClaimChildren = false
  Direction = (1,-2e-16,3e-16)
  Fit = 0
  FitJoin = 0
  InnerFit = 0
  InnerFitJoin = 0
  Length = 3
  Length2 = 100
  Linearize = true
  Midplane = true
  NewSolid = false
  Profile = -> Sketch066
  Refine = true
  Suppress = false
  TaperInnerAngle = 0
  TaperInnerAngleRev = 0
  TreeRank = 315
  Type = 0
  _ProfileBasedVersion = 1
FEATURE [Sketcher::SketchObject] Sketch067
  ArcFitTolerance = 1e-06
  AttachmentSupport = -> [XZ_Plane]
  ExternalBSplineMaxDegree = 5
  ExternalBSplineTolerance = 0.0001
  ExternalGeometry = -> [Import]
  FullyConstrained = true
  InternalTolerance = 1e-06
  MakeInternals = true
  MapMode = 5
  Placement = pos=(0,0,0) rot=(1,0,0;1.5708rad)
  Support = -> [XZ_Plane]
  TreeRank = 316
  sketch-geometry (8):
    g0: ArcOfCircle CenterX=-40 CenterY=145 CenterZ=0 NormalX=0 NormalY=0 NormalZ=1 AngleXU=0 Radius=8 StartAngle=1.5708 EndAngle=4.71239
    g1: ArcOfCircle CenterX=-35 CenterY=145 CenterZ=0 NormalX=0 NormalY=0 NormalZ=1 AngleXU=0 Radius=8 StartAngle=4.71239 EndAngle=7.85398
    g2: LineSegment StartX=-40 StartY=137 StartZ=0 EndX=-35 EndY=137 EndZ=0
    g3: LineSegment StartX=-35 StartY=153 StartZ=0 EndX=-40 EndY=153 EndZ=0
    g4: ArcOfCircle CenterX=40 CenterY=145 CenterZ=0 NormalX=0 NormalY=0 NormalZ=1 AngleXU=0 Radius=8 StartAngle=4.71239 EndAngle=7.85398
    g5: ArcOfCircle CenterX=35 CenterY=145 CenterZ=0 NormalX=0 NormalY=0 NormalZ=1 AngleXU=0 Radius=8 StartAngle=1.5708 EndAngle=4.71239
    g6: LineSegment StartX=40 StartY=153 StartZ=0 EndX=35 EndY=153 EndZ=0
    g7: LineSegment StartX=35 StartY=137 StartZ=0 EndX=40 EndY=137 EndZ=0
  constraints (17):
    c: Tangent(g0,g2) = -1.5708
    c: Tangent(g2,g1) = -1.5708
    c: Tangent(g1,g3) = -1.5708
    c: Tangent(g3,g0) = -1.5708
    c: Equal(g0,g1)
    c: Tangent(g4,g6) = -1.5708
    c: Tangent(g6,g5) = -1.5708
    c: Tangent(g5,g7) = -1.5708
    c: Tangent(g7,g4) = -1.5708
    c: Equal(g4,g5)
    c: Horizontal(g4,g5)
    c: Coincident(g1,g-3)
    c: Equal(g5,g1)
    c: Symmetric(g5,g1,g-2)
    c: Symmetric(g4,g0,g-2)
    c: PointOnObject(g4,g-4)
    c: Radius(g1) = 8
FEATURE [PartDesign::Pocket] Pocket022
  AddSubType = 1
  AutoTaperInnerAngle = true
  BaseFeature = -> Pad018
  CheckUpToFaceLimits = true
  ClaimChildren = false
  Fit = 0
  FitJoin = 0
  InnerFit = 0
  InnerFitJoin = 0
  Length = 5
  Length2 = 100
  Linearize = true
  NewSolid = false
  Profile = -> Sketch067
  Refine = true
  Suppress = false
  TaperInnerAngle = 0
  TaperInnerAngleRev = 0
  TreeRank = 317
  Type = 1
  _ProfileBasedVersion = 1
  _Version = 1
FEATURE [PartDesign::Fillet] Fillet
  AddSubType = 0
  Base = -> Pocket022 [Edge64,Edge67,Edge49,Edge51]
  BaseFeature = -> Pocket022
  NewSolid = false
  Radius = 4
  Refine = true
  SupportTransform = false
  Suppress = false
  TreeRank = 318
FEATURE [PartDesign::Chamfer] Chamfer015
  AddSubType = 0
  Angle = 45
  Base = -> Fillet [Edge81,Edge77,Edge79,Edge75]
  BaseFeature = -> Fillet
  ChamferType = 0
  FlipDirection = false
  NewSolid = false
  Refine = true
  Size = 2
  Size2 = 1
  SupportTransform = false
  Suppress = false
  TreeRank = 319
FEATURE [PartDesign::Pocket] Pocket023
  AddSubType = 1
  AutoTaperInnerAngle = true
  BaseFeature = -> Chamfer015
  CheckUpToFaceLimits = true
  ClaimChildren = false
  Fit = 0
  FitJoin = 0
  InnerFit = 0
  InnerFitJoin = 0
  Length = 111
  Length2 = 100
  Linearize = true
  NewSolid = false
  Profile = -> Chamfer015 [Face13]
  Refine = true
  Suppress = false
  TaperInnerAngle = 0
  TaperInnerAngleRev = 0
  TreeRank = 320
  Type = 0
  _ProfileBasedVersion = 1
  _Version = 1
FEATURE [Sketcher::SketchObject] Sketch068
  ArcFitTolerance = 1e-06
  AttachmentSupport = -> [YZ_Plane]
  ExternalBSplineMaxDegree = 5
  ExternalBSplineTolerance = 0.0001
  ExternalGeometry = -> [Pocket023]
  FullyConstrained = true
  InternalTolerance = 1e-06
  MakeInternals = true
  MapMode = 5
  Placement = pos=(0,0,0) rot=(0.57735,0.57735,0.57735;2.0944rad)
  Support = -> [YZ_Plane]
  TreeRank = 321
  sketch-geometry (9):
    g0: LineSegment StartX=31.4967 StartY=117.6 StartZ=0 EndX=30.4967 EndY=117.6 EndZ=0
    g1: LineSegment StartX=30.4967 StartY=117.6 StartZ=0 EndX=30.4967 EndY=114.4 EndZ=0
    g2: LineSegment StartX=30.4967 StartY=114.4 StartZ=0 EndX=31.4967 EndY=114.4 EndZ=0
    g3: LineSegment [constr] StartX=31.4967 StartY=114.4 StartZ=0 EndX=31.4967 EndY=117.6 EndZ=0
    g4: LineSegment [constr] StartX=30.4967 StartY=116 StartZ=0 EndX=31.4967 EndY=116 EndZ=0
    g5: LineSegment [constr] StartX=16.966 StartY=111 StartZ=0 EndX=16.966 EndY=0 EndZ=0
    g6: LineSegment StartX=31.4967 StartY=117.6 StartZ=0 EndX=32.4967 EndY=117.6 EndZ=0
    g7: LineSegment StartX=32.4967 StartY=117.6 StartZ=0 EndX=32.4967 EndY=114.4 EndZ=0
    g8: LineSegment StartX=32.4967 StartY=114.4 StartZ=0 EndX=31.4967 EndY=114.4 EndZ=0
  constraints (26):
    c: Coincident(g0,g1)
    c: Coincident(g1,g2)
    c: Coincident(g2,g3)
    c: Coincident(g3,g0)
    c: Horizontal(g0)
    c: Horizontal(g2)
    c: Vertical(g1)
    c: Vertical(g3)
    c: PointOnObject(g4,g1)
    c: Horizontal(g4)
    c: Symmetric(g2,g0,g4)
    c: Vertical(g2,g-3)
    c: DistanceY(g1,g1) = 3.2
    c: DistanceX(g0,g0) = 1
    c: DistanceY(g-3,g4) = 5
    c: Vertical(g5)
    c: PointOnObject(g5,g-1)
    c: Symmetric(g-3,g-3,g5)
    c: Coincident(g6,g0)
    c: Horizontal(g6)
    c: Coincident(g7,g6)
    c: Vertical(g7)
    c: Coincident(g8,g7)
    c: Coincident(g8,g2)
    c: Horizontal(g8)
    c: Equal(g6,g0)
FEATURE [PartDesign::Line] DatumLine
  AttacherType = Attacher::AttachEngineLine
  AttachmentSupport = -> [Sketch059]
  Length = 235.37
  MapMode = 42
  MinimumLength = 10
  Placement = pos=(-1.07e-14,16,0) rot=(0,0,1;0rad)
  ResizeMode = 0
  Support = -> [Sketch059]
  TreeRank = 322
FEATURE [PartDesign::Groove] Groove
  AddSubType = 1
  Angle = 260
  Axis = (0,0,1)
  Base = (-1.07e-14,16,0)
  BaseFeature = -> Pocket023
  ClaimChildren = false
  Fit = 0
  FitJoin = 0
  InnerFit = 0
  InnerFitJoin = 0
  Linearize = true
  Midplane = true
  NewSolid = false
  Profile = -> Sketch068
  ReferenceAxis = -> DatumLine
  Refine = true
  Suppress = false
  TreeRank = 323
  _ProfileBasedVersion = 1
FEATURE [PartDesign::Fillet] Fillet007
  AddSubType = 0
  Base = -> Groove [Edge142,Edge132,Edge140,Edge135,Edge137]
  BaseFeature = -> Groove
  NewSolid = false
  Radius = 1.5
  Refine = true
  SupportTransform = false
  Suppress = false
  TreeRank = 324
FEATURE [PartDesign::SubtractivePipe] Pipe020
  AddSubType = 1
  AuxilleryCurvelinear = true
  AuxillerySpineTangent = false
  BaseFeature = -> Fillet007
  Binormal = (0,0,0)
  ClaimChildren = false
  Fit = 0
  FitJoin = 0
  InnerFit = 0
  InnerFitJoin = 0
  Linearize = true
  Mode = 0
  MoveProfile = false
  NewSolid = false
  Profile = -> Sketch060
  Refine = true
  RotateProfile = false
  Spine = -> Binder001 [Edge1,Edge2,Edge3]
  SpineTangent = false
  Suppress = false
  Transformation = 0
  Transition = 1
  TreeRank = 325
  _ProfileBasedVersion = 2
FEATURE [Sketcher::SketchObject] Sketch069
  ArcFitTolerance = 1e-06
  AttachmentSupport = -> [XZ_Plane]
  ExternalBSplineMaxDegree = 5
  ExternalBSplineTolerance = 0.0001
  ExternalGeometry = -> [Sketch062]
  FullyConstrained = true
  InternalTolerance = 1e-06
  MakeInternals = true
  MapMode = 5
  Placement = pos=(0,0,0) rot=(1,0,0;1.5708rad)
  Support = -> [XZ_Plane]
  TreeRank = 326
  sketch-geometry (4):
    g0: ArcOfCircle CenterX=-14 CenterY=181.627 CenterZ=0 NormalX=0 NormalY=0 NormalZ=1 AngleXU=0 Radius=14 StartAngle=1.5708 EndAngle=4.71239
    g1: ArcOfCircle CenterX=14 CenterY=181.627 CenterZ=0 NormalX=0 NormalY=0 NormalZ=1 AngleXU=0 Radius=14 StartAngle=4.71239 EndAngle=7.85398
    g2: LineSegment StartX=-14 StartY=167.627 StartZ=0 EndX=14 EndY=167.627 EndZ=0
    g3: LineSegment StartX=14 StartY=195.627 StartZ=0 EndX=-14 EndY=195.627 EndZ=0
  constraints (8):
    c: Tangent(g0,g2) = -1.5708
    c: Tangent(g2,g1) = -1.5708
    c: Tangent(g1,g3) = -1.5708
    c: Tangent(g3,g0) = -1.5708
    c: Equal(g0,g1)
    c: Coincident(g0,g-3)
    c: Coincident(g1,g-4)
    c: DistanceY(g1,g-4) = 2
FEATURE [PartDesign::SubtractivePipe] Pipe021
  AddSubType = 1
  AuxilleryCurvelinear = true
  AuxillerySpineTangent = false
  BaseFeature = -> Pipe020
  Binormal = (0,0,0)
  ClaimChildren = false
  Fit = 0
  FitJoin = 0
  InnerFit = 0
  InnerFitJoin = 0
  Linearize = true
  Mode = 0
  MoveProfile = false
  NewSolid = false
  Profile = -> Sketch069
  Refine = true
  RotateProfile = false
  Spine = -> Binder001 [Edge8,Edge9]
  SpineTangent = false
  Suppress = false
  Transformation = 0
  Transition = 1
  TreeRank = 327
  _ProfileBasedVersion = 2
FEATURE [Sketcher::SketchObject] Sketch070
  ArcFitTolerance = 1e-06
  AttachmentSupport = -> [XY_Plane007]
  ExternalBSplineMaxDegree = 5
  ExternalBSplineTolerance = 0.0001
  FullyConstrained = true
  InternalTolerance = 1e-06
  MakeInternals = true
  MapMode = 5
  Placement = pos=(0,0,0) rot=(0,1,0;3.14159rad)
  Support = -> [XY_Plane007]
  TreeRank = 338
  sketch-geometry (2):
    g0: Circle CenterX=0 CenterY=16 CenterZ=0 NormalX=0 NormalY=0 NormalZ=1 AngleXU=0 Radius=13.5
    g1: Circle CenterX=0 CenterY=16 CenterZ=0 NormalX=0 NormalY=0 NormalZ=1 AngleXU=0 Radius=15.5
  constraints (5):
    c: PointOnObject(g0,g-2)
    c: Coincident(g1,g0)
    c: Diameter(g1) = 31
    c: Diameter(g0) = 27
    c: DistanceY(g-1,g0) = 16
FEATURE [PartDesign::SubShapeBinder] Import002  label="Import002(Pipe021)"
  BindCopyOnChange = 0
  BindMode = 0
  ClaimChildren = false
  Context = -> Part [Body007.Import002.]
  EdgeTolerance = 1e-06
  FillStyle = 0
  Fuse = false
  MakeFace = false
  MergeEdges = true
  OffsetFill = false
  OffsetIntersection = false
  OffsetJoinType = 0
  OffsetOpenResult = false
  Outline = false
  PartialLoad = false
  Relative = true
  SplitEdges = false
  Support = -> [Body[Pipe021.Face10]]
  TightBound = false
  TreeRank = 340
  _Version = 8
FEATURE [PartDesign::Pad] Pad019
  AddSubType = 0
  AlongSketchNormal = false
  AutoTaperInnerAngle = true
  CheckUpToFaceLimits = true
  ClaimChildren = false
  Direction = (1e-16,0,-1)
  Fit = 0
  FitJoin = 0
  InnerFit = 0
  InnerFitJoin = 0
  Length = 10
  Length2 = 100
  Linearize = true
  NewSolid = false
  Profile = -> Sketch070
  Refine = true
  Reversed = true
  Suppress = false
  TaperInnerAngle = 0
  TaperInnerAngleRev = 0
  TreeRank = 339
  Type = 3
  UpToFace = -> Import002
  _ProfileBasedVersion = 1
FEATURE [Sketcher::SketchObject] Sketch071
  ArcFitTolerance = 1e-06
  AttachmentSupport = -> [Pad019]
  ExternalBSplineMaxDegree = 5
  ExternalBSplineTolerance = 0.0001
  ExternalGeometry = -> [Pad019]
  FullyConstrained = true
  InternalTolerance = 1e-06
  MakeInternals = true
  MapMode = 5
  Placement = pos=(-3.59e-14,1.27e-14,111) rot=(0,0,1;0rad)
  Support = -> [Pad019]
  TreeRank = 341
  sketch-geometry (4):
    g0: ArcOfCircle CenterX=-8.6903e-12 CenterY=16 CenterZ=0 NormalX=0 NormalY=0 NormalZ=1 AngleXU=0 Radius=15.5 StartAngle=5.23599 EndAngle=10.472
    g1: ArcOfCircle CenterX=-8.6903e-12 CenterY=16 CenterZ=0 NormalX=0 NormalY=0 NormalZ=1 AngleXU=0 Radius=17.7781 StartAngle=5.16346 EndAngle=10.5445
    g2: LineSegment StartX=7.75 StartY=-8.926e-13 StartZ=0 EndX=7.75 EndY=2.57661 EndZ=0
    g3: LineSegment StartX=-7.75 StartY=2.57661 StartZ=0 EndX=-7.75 EndY=-1.39573e-11 EndZ=0
  constraints (12):
    c: Coincident(g0,g-3)
    c: PointOnObject(g0,g-3)
    c: Coincident(g1,g0)
    c: PointOnObject(g1,g-1)
    c: PointOnObject(g1,g-1)
    c: Horizontal(g0,g0)
    c: DistanceX(g0,g0) = 15.5
    c: Coincident(g2,g1)
    c: Coincident(g2,g0)
    c: Coincident(g3,g0)
    c: Coincident(g3,g1)
    c: Vertical(g3)
FEATURE [Sketcher::SketchObject] Sketch072
  ArcFitTolerance = 1e-06
  AttachmentSupport = -> [Pad019]
  ExternalBSplineMaxDegree = 5
  ExternalBSplineTolerance = 0.0001
  ExternalGeometry = -> [Sketch071]
  FullyConstrained = true
  InternalTolerance = 1e-06
  MakeInternals = true
  MapMode = 5
  Placement = pos=(-3.59e-14,1.27e-14,111) rot=(0,0,1;0rad)
  Support = -> [Pad019]
  TreeRank = 342
  sketch-geometry (3):
    g0: ArcOfCircle CenterX=0 CenterY=16 CenterZ=0 NormalX=0 NormalY=0 NormalZ=1 AngleXU=0 Radius=17.7781 StartAngle=5.16346 EndAngle=10.5445
    g1: LineSegment StartX=-7.75 StartY=0 StartZ=0 EndX=7.75 EndY=-8.926e-13 EndZ=0
    g2: Circle CenterX=0 CenterY=16 CenterZ=0 NormalX=0 NormalY=0 NormalZ=1 AngleXU=0 Radius=14.5
  constraints (8):
    c: PointOnObject(g0,g-2)
    c: PointOnObject(g0,g-1)
    c: Coincident(g1,g0)
    c: Coincident(g1,g0)
    c: Coincident(g-3,g0)
    c: Tangent(g0,g-4)
    c: Coincident(g2,g0)
    c: Diameter(g2) = 29
FEATURE [PartDesign::Pad] Pad020
  AddSubType = 0
  AlongSketchNormal = false
  AutoTaperInnerAngle = true
  BaseFeature = -> Pad019
  CheckUpToFaceLimits = true
  ClaimChildren = false
  Direction = (-3e-16,1e-16,1)
  Fit = 0
  FitJoin = 0
  InnerFit = 0
  InnerFitJoin = 0
  Length = 10
  Length2 = 100
  Linearize = true
  NewSolid = false
  Profile = -> Sketch072
  Refine = true
  Reversed = true
  Suppress = false
  TaperInnerAngle = 0
  TaperInnerAngleRev = 0
  TreeRank = 343
  Type = 0
  _ProfileBasedVersion = 1
FEATURE [PartDesign::Pad] Pad021
  AddSubType = 0
  AlongSketchNormal = false
  AutoTaperInnerAngle = true
  BaseFeature = -> Pad020
  CheckUpToFaceLimits = true
  ClaimChildren = false
  Direction = (-3e-16,1e-16,1)
  Fit = 0
  FitJoin = 0
  InnerFit = 0
  InnerFitJoin = 0
  Length = 10
  Length2 = 100
  Linearize = true
  NewSolid = false
  Profile = -> Sketch071
  Refine = true
  Suppress = false
  TaperInnerAngle = 0
  TaperInnerAngleRev = 0
  TreeRank = 344
  Type = 0
  _ProfileBasedVersion = 1
FEATURE [PartDesign::Pocket] Pocket024
  AddSubType = 1
  AutoTaperInnerAngle = true
  BaseFeature = -> Pad021
  CheckUpToFaceLimits = true
  ClaimChildren = false
  Fit = 0
  FitJoin = 0
  InnerFit = 0
  InnerFitJoin = 0
  Length = 36
  Length2 = 100
  Linearize = true
  NewSolid = false
  Profile = -> Pad021 [Face3]
  Refine = true
  Suppress = false
  TaperInnerAngle = 0
  TaperInnerAngleRev = 0
  TreeRank = 345
  Type = 0
  _ProfileBasedVersion = 1
  _Version = 1
FEATURE [Sketcher::SketchObject] Sketch073
  ArcFitTolerance = 1e-06
  AttachmentSupport = -> [YZ_Plane007]
  ExternalBSplineMaxDegree = 5
  ExternalBSplineTolerance = 0.0001
  ExternalGeometry = -> [Pocket024]
  FullyConstrained = true
  InternalTolerance = 1e-06
  MakeInternals = true
  MapMode = 5
  Placement = pos=(0,0,0) rot=(0.57735,0.57735,0.57735;2.0944rad)
  Support = -> [YZ_Plane007]
  TreeRank = 346
  sketch-geometry (4):
    g0: ArcOfCircle CenterX=16 CenterY=36 CenterZ=0 NormalX=0 NormalY=0 NormalZ=1 AngleXU=0 Radius=13.5 StartAngle=1.5708 EndAngle=3.14159
    g1: LineSegment StartX=16 StartY=49.5 StartZ=0 EndX=35 EndY=49.5 EndZ=0
    g2: LineSegment StartX=35 StartY=49.5 StartZ=0 EndX=35 EndY=36 EndZ=0
    g3: LineSegment StartX=35 StartY=36 StartZ=0 EndX=2.5 EndY=36 EndZ=0
  constraints (11):
    c: Horizontal(g1)
    c: Coincident(g2,g1)
    c: Vertical(g2)
    c: Coincident(g3,g0)
    c: Coincident(g3,g2)
    c: Horizontal(g3)
    c: PointOnObject(g0,g3)
    c: DistanceX(g0) = 16
    c: Coincident(g0,g-3)
    c: Tangent(g1,g0) = 1.5708
    c: DistanceX(g2) = 35
FEATURE [PartDesign::Pocket] Pocket025
  AddSubType = 1
  AutoTaperInnerAngle = true
  BaseFeature = -> Pocket024
  CheckUpToFaceLimits = true
  ClaimChildren = false
  Fit = 0
  FitJoin = 0
  InnerFit = 0
  InnerFitJoin = 0
  Length = 5
  Length2 = 100
  Linearize = true
  Midplane = true
  NewSolid = false
  Profile = -> Sketch073
  Refine = true
  Suppress = false
  TaperInnerAngle = 0
  TaperInnerAngleRev = 0
  TreeRank = 347
  Type = 1
  _ProfileBasedVersion = 1
  _Version = 1
FEATURE [PartDesign::Chamfer] Chamfer016
  AddSubType = 0
  Angle = 45
  Base = -> Pocket025 [Edge11]
  BaseFeature = -> Pocket025
  ChamferType = 0
  FlipDirection = false
  NewSolid = false
  Refine = true
  Size = 2
  Size2 = 1
  SupportTransform = false
  Suppress = false
  TreeRank = 348
FEATURE [PartDesign::Fillet] Fillet008
  AddSubType = 0
  Base = -> Chamfer016 [Edge17]
  BaseFeature = -> Chamfer016
  NewSolid = false
  Radius = 0.5
  Refine = true
  SupportTransform = false
  Suppress = false
  TreeRank = 349
FEATURE [PartDesign::Chamfer] Chamfer017
  AddSubType = 0
  Angle = 45
  Base = -> Fillet008 [Edge44,Edge42]
  BaseFeature = -> Fillet008
  ChamferType = 0
  FlipDirection = false
  NewSolid = false
  Refine = true
  Size = 3
  Size2 = 1
  SupportTransform = false
  Suppress = false
  TreeRank = 350
FEATURE [Sketcher::SketchObject] Sketch074
  ArcFitTolerance = 1e-06
  AttachmentSupport = -> [YZ_Plane007]
  ExternalBSplineMaxDegree = 5
  ExternalBSplineTolerance = 0.0001
  ExternalGeometry = -> [Chamfer017]
  FullyConstrained = true
  InternalTolerance = 1e-06
  MakeInternals = true
  MapMode = 5
  Placement = pos=(0,0,0) rot=(0.57735,0.57735,0.57735;2.0944rad)
  Support = -> [YZ_Plane007]
  TreeRank = 351
  sketch-geometry (1):
    g0: Circle CenterX=16 CenterY=116 CenterZ=0 NormalX=0 NormalY=0 NormalZ=1 AngleXU=0 Radius=2.1
  constraints (3):
    c: DistanceX(g0) = 16
    c: DistanceY(g0,g-3) = 5
    c: Diameter(g0) = 4.2
FEATURE [Sketcher::SketchObject] Sketch075
  ArcFitTolerance = 1e-06
  AttachmentSupport = -> [Chamfer017]
  ExternalBSplineMaxDegree = 5
  ExternalBSplineTolerance = 0.0001
  ExternalGeometry = -> [Chamfer017]
  FullyConstrained = true
  InternalTolerance = 1e-06
  MakeInternals = true
  MapMode = 5
  Placement = pos=(-3.19e-14,1.92e-14,121) rot=(0,0,1;0rad)
  Support = -> [Chamfer017]
  TreeRank = 352
  sketch-geometry (9):
    g0: LineSegment StartX=16.1187 StartY=23.5 StartZ=0 EndX=23.1187 EndY=23.5 EndZ=0
    g1: LineSegment StartX=23.1187 StartY=23.5 StartZ=0 EndX=23.1187 EndY=8.5 EndZ=0
    g2: LineSegment StartX=23.1187 StartY=8.5 StartZ=0 EndX=16.1187 EndY=8.5 EndZ=0
    g3: LineSegment StartX=16.1187 StartY=8.5 StartZ=0 EndX=16.1187 EndY=23.5 EndZ=0
    g4: LineSegment [constr] StartX=-8.7138e-12 StartY=16 StartZ=0 EndX=23.1187 EndY=16 EndZ=0
    g5: LineSegment StartX=-16.1187 StartY=23.5 StartZ=0 EndX=-23.1187 EndY=23.5 EndZ=0
    g6: LineSegment StartX=-23.1187 StartY=23.5 StartZ=0 EndX=-23.1187 EndY=8.5 EndZ=0
    g7: LineSegment StartX=-23.1187 StartY=8.5 StartZ=0 EndX=-16.1187 EndY=8.5 EndZ=0
    g8: LineSegment StartX=-16.1187 StartY=8.5 StartZ=0 EndX=-16.1187 EndY=23.5 EndZ=0
  constraints (26):
    c: Coincident(g0,g1)
    c: Coincident(g1,g2)
    c: Coincident(g2,g3)
    c: Coincident(g3,g0)
    c: Horizontal(g0)
    c: Horizontal(g2)
    c: Vertical(g1)
    c: Vertical(g3)
    c: Coincident(g4,g-3)
    c: PointOnObject(g4,g1)
    c: Symmetric(g2,g0,g4)
    c: PointOnObject(g0,g-3)
    c: DistanceX(g0,g0) = 7
    c: DistanceY(g1,g1) = 15
    c: Coincident(g5,g6)
    c: Coincident(g6,g7)
    c: Coincident(g7,g8)
    c: Coincident(g8,g5)
    c: Horizontal(g5)
    c: Horizontal(g7)
    c: Vertical(g6)
    c: Vertical(g8)
    c: PointOnObject(g5,g-3)
    c: PointOnObject(g7,g-3)
    c: Equal(g8,g3)
    c: Equal(g5,g0)
FEATURE [PartDesign::Pad] Pad022
  AddSubType = 0
  AlongSketchNormal = false
  AutoTaperInnerAngle = true
  BaseFeature = -> Chamfer017
  CheckUpToFaceLimits = true
  ClaimChildren = false
  Direction = (-3e-16,2e-16,1)
  Fit = 0
  FitJoin = 0
  InnerFit = 0
  InnerFitJoin = 0
  Length = 10
  Length2 = 100
  Linearize = true
  NewSolid = false
  Profile = -> Sketch075
  Refine = true
  Reversed = true
  Suppress = false
  TaperInnerAngle = 0
  TaperInnerAngleRev = 0
  TreeRank = 353
  Type = 0
  _ProfileBasedVersion = 1
FEATURE [PartDesign::Fillet] Fillet009
  AddSubType = 0
  Base = -> Pad022 [Edge3,Edge5,Edge7,Edge9]
  BaseFeature = -> Pad022
  NewSolid = false
  Radius = 4
  Refine = true
  SupportTransform = false
  Suppress = false
  TreeRank = 354
FEATURE [PartDesign::Chamfer] Chamfer018
  AddSubType = 0
  Angle = 45
  Base = -> Fillet009 [Edge65,Edge66,Edge67,Edge63]
  BaseFeature = -> Fillet009
  ChamferType = 0
  FlipDirection = false
  NewSolid = false
  Refine = true
  Size = 2
  Size2 = 1
  SupportTransform = false
  Suppress = false
  TreeRank = 355
FEATURE [PartDesign::Pocket] Pocket026
  AddSubType = 1
  AutoTaperInnerAngle = true
  BaseFeature = -> Chamfer018
  CheckUpToFaceLimits = true
  ClaimChildren = false
  Fit = 0
  FitJoin = 0
  InnerFit = 0
  InnerFitJoin = 0
  Length = 5
  Length2 = 100
  Linearize = true
  Midplane = true
  NewSolid = false
  Profile = -> Sketch074
  Refine = true
  Suppress = false
  TaperInnerAngle = 0
  TaperInnerAngleRev = 0
  TreeRank = 356
  Type = 1
  _ProfileBasedVersion = 1
  _Version = 1
FEATURE [PartDesign::Chamfer] Chamfer019
  AddSubType = 0
  Angle = 45
  Base = -> Pocket026 [Face1]
  BaseFeature = -> Pocket026
  ChamferType = 0
  FlipDirection = false
  NewSolid = false
  Refine = true
  Size = 0.4
  Size2 = 1
  SupportTransform = false
  Suppress = false
  TreeRank = 357
FEATURE [PartDesign::Chamfer] Chamfer020
  AddSubType = 0
  Angle = 45
  Base = -> Chamfer019 [Edge120,Edge74]
  BaseFeature = -> Chamfer019
  ChamferType = 0
  FlipDirection = false
  NewSolid = false
  Refine = true
  Size = 1
  Size2 = 1
  SupportTransform = false
  Suppress = false
  TreeRank = 358
FEATURE [PartDesign::Body] Body007  label="TubeEntree"
  AutoGroupSolids = false
  ClaimAllChildren = false
  ExportMode = 0
  Group = -> [Sketch070,Pad019,Import002,Sketch071,Sketch072,Pad020,Pad021,Pocket024,Sketch073,Pocket025,Chamfer016,Fillet008,Chamfer017,Sketch074,Sketch075,Pad022,Fillet009,Chamfer018,Pocket026,Chamfer019,Chamfer020]
  Origin = -> Origin009
  SingleSolid = true
  Tip = -> Chamfer020
  TreeRank = 337
  _ExportChildren = -> [Pad019,Import002,Pad020,Pad021,Pocket024,Pocket025,Chamfer016,Fillet008,Chamfer017,Pad022,Fillet009,Chamfer018,Pocket026,Chamfer019,Chamfer020]
  _GroupVersion = 1
FEATURE [PartDesign::SubShapeBinder] Binder002  label="Binder002(Pocket020)"
  BindCopyOnChange = 0
  BindMode = 0
  ClaimChildren = false
  Context = -> Part [Body008.Binder002.]
  EdgeTolerance = 1e-06
  FillStyle = 0
  Fuse = false
  MakeFace = true
  MergeEdges = true
  OffsetFill = false
  OffsetIntersection = false
  OffsetJoinType = 0
  OffsetOpenResult = false
  Outline = false
  PartialLoad = false
  Relative = true
  SplitEdges = false
  Support = -> [Body005[Pocket020.Face2]]
  TightBound = false
  TreeRank = 369
  _Version = 8
FEATURE [Sketcher::SketchObject] Sketch076
  ArcFitTolerance = 1e-06
  AttachmentSupport = -> [XZ_Plane008]
  ExternalBSplineMaxDegree = 5
  ExternalBSplineTolerance = 0.0001
  ExternalGeometry = -> [Binder002]
  FullyConstrained = true
  InternalTolerance = 1e-06
  MakeInternals = true
  MapMode = 5
  Placement = pos=(0,0,0) rot=(1,0,0;1.5708rad)
  Support = -> [XZ_Plane008]
  TreeRank = 370
  sketch-geometry (15):
    g0: Circle CenterX=-2e-16 CenterY=260 CenterZ=0 NormalX=0 NormalY=0 NormalZ=1 AngleXU=0 Radius=18.65
    g1: Circle CenterX=-18 CenterY=278 CenterZ=0 NormalX=0 NormalY=0 NormalZ=1 AngleXU=0 Radius=1.6
    g2: Circle CenterX=18 CenterY=278 CenterZ=0 NormalX=0 NormalY=0 NormalZ=1 AngleXU=0 Radius=1.6
    g3: Circle CenterX=18 CenterY=242 CenterZ=0 NormalX=0 NormalY=0 NormalZ=1 AngleXU=0 Radius=1.6
    g4: Circle CenterX=-18 CenterY=242 CenterZ=0 NormalX=0 NormalY=0 NormalZ=1 AngleXU=0 Radius=1.6
    g5: ArcOfCircle CenterX=-18 CenterY=278 CenterZ=0 NormalX=0 NormalY=0 NormalZ=1 AngleXU=0 Radius=4.5 StartAngle=1.5708 EndAngle=3.14159
    g6: LineSegment StartX=-18 StartY=282.5 StartZ=0 EndX=18 EndY=282.5 EndZ=0
    g7: ArcOfCircle CenterX=18 CenterY=278 CenterZ=0 NormalX=0 NormalY=0 NormalZ=1 AngleXU=0 Radius=4.5 StartAngle=-7.274e-13 EndAngle=1.5708
    g8: LineSegment StartX=22.5 StartY=278 StartZ=0 EndX=22.5 EndY=242 EndZ=0
    g9: ArcOfCircle CenterX=18 CenterY=242 CenterZ=0 NormalX=0 NormalY=0 NormalZ=1 AngleXU=0 Radius=4.5 StartAngle=4.71239 EndAngle=6.28319
    g10: LineSegment StartX=18 StartY=237.5 StartZ=0 EndX=-18 EndY=237.5 EndZ=0
    g11: ArcOfCircle CenterX=-18 CenterY=242 CenterZ=0 NormalX=0 NormalY=0 NormalZ=1 AngleXU=0 Radius=4.5 StartAngle=3.14159 EndAngle=4.71239
    g12: LineSegment StartX=-22.5 StartY=242 StartZ=0 EndX=-22.5 EndY=278 EndZ=0
    g13: GeomPoint [constr] X=-22.5 Y=282.5 Z=0
    g14: GeomPoint [constr] X=22.5 Y=237.5 Z=0
  constraints (32):
    c: Tangent(g0,g-3) = -1.5708
    c: Equal(g0,g-3)
    c: Coincident(g1,g-4)
    c: Coincident(g2,g-5)
    c: Coincident(g3,g-6)
    c: Coincident(g4,g-7)
    c: Equal(g4,g1)
    c: Equal(g4,g2)
    c: Equal(g4,g3)
    c: Diameter(g4) = 3.2
    c: Tangent(g5,g6) = 1.5708
    c: Tangent(g6,g7) = 1.5708
    c: Tangent(g7,g8) = 1.5708
    c: Tangent(g8,g9) = 1.5708
    c: Tangent(g9,g10) = 1.5708
    c: Tangent(g10,g11) = 1.5708
    c: Tangent(g11,g12) = 1.5708
    c: Tangent(g12,g5) = 1.5708
    c: Horizontal(g6)
    c: Horizontal(g10)
    c: Vertical(g8)
    c: Vertical(g12)
    c: Equal(g5,g7)
    c: Equal(g7,g9)
    c: Equal(g9,g11)
    c: PointOnObject(g13,g6)
    c: PointOnObject(g13,g12)
    c: PointOnObject(g14,g8)
    c: PointOnObject(g14,g10)
    c: Coincident(g9,g3)
    c: Coincident(g5,g1)
    c: DistanceX(g5,g7) = 45
FEATURE [PartDesign::Pad] Pad023
  AddSubType = 0
  AlongSketchNormal = false
  AutoTaperInnerAngle = true
  CheckUpToFaceLimits = true
  ClaimChildren = false
  Direction = (0,-1,-2e-16)
  Fit = 0
  FitJoin = 0
  InnerFit = 0
  InnerFitJoin = 0
  Length = 10
  Length2 = 100
  Linearize = true
  NewSolid = false
  Profile = -> Sketch076
  Refine = true
  Reversed = true
  Suppress = false
  TaperInnerAngle = 0
  TaperInnerAngleRev = 0
  TreeRank = 371
  Type = 0
  _ProfileBasedVersion = 1
FEATURE [PartDesign::Chamfer] Chamfer021
  AddSubType = 0
  Angle = 45
  Base = -> Pad023 [Face14,Face15]
  BaseFeature = -> Pad023
  ChamferType = 0
  FlipDirection = false
  NewSolid = false
  Refine = true
  Size = 0.4
  Size2 = 1
  SupportTransform = false
  Suppress = false
  TreeRank = 372
FEATURE [PartDesign::Body] Body008  label="SpacerTurbine"
  AutoGroupSolids = false
  ClaimAllChildren = false
  ExportMode = 0
  Group = -> [Binder002,Sketch076,Pad023,Chamfer021]
  Origin = -> Origin010
  SingleSolid = true
  Tip = -> Chamfer021
  TreeRank = 368
  _ExportChildren = -> [Binder002,Pad023,Chamfer021]
  _GroupVersion = 1
FEATURE [PartDesign::SubShapeBinder] Binder003  label="Binder003(Pad023)"
  BindCopyOnChange = 0
  BindMode = 0
  ClaimChildren = false
  Context = -> Part [Body009.Binder003.]
  EdgeTolerance = 1e-06
  FillStyle = 0
  Fuse = false
  MakeFace = true
  MergeEdges = true
  OffsetFill = false
  OffsetIntersection = false
  OffsetJoinType = 0
  OffsetOpenResult = false
  Outline = false
  PartialLoad = false
  Relative = true
  SplitEdges = false
  Support = -> [Body008[Pad023.Face15]]
  TightBound = false
  TreeRank = 384
  _Version = 8
FEATURE [Sketcher::SketchObject] Sketch077
  ArcFitTolerance = 1e-06
  AttachmentSupport = -> [Binder003]
  ExternalBSplineMaxDegree = 5
  ExternalBSplineTolerance = 0.0001
  ExternalGeometry = -> [Binder003]
  FullyConstrained = true
  InternalTolerance = 1e-06
  MakeInternals = true
  MapMode = 5
  Placement = pos=(0,10,2.2e-15) rot=(0,0.707107,0.707107;3.14159rad)
  Support = -> [Binder003]
  TreeRank = 385
  sketch-geometry (12):
    g0: Circle CenterX=-18 CenterY=278 CenterZ=0 NormalX=0 NormalY=0 NormalZ=1 AngleXU=0 Radius=1.6
    g1: Circle CenterX=18 CenterY=278 CenterZ=0 NormalX=0 NormalY=0 NormalZ=1 AngleXU=0 Radius=1.6
    g2: Circle CenterX=18 CenterY=242 CenterZ=0 NormalX=0 NormalY=0 NormalZ=1 AngleXU=0 Radius=1.6
    g3: Circle CenterX=-18 CenterY=242 CenterZ=0 NormalX=0 NormalY=0 NormalZ=1 AngleXU=0 Radius=1.6
    g4: ArcOfCircle CenterX=1.79506e-11 CenterY=260 CenterZ=0 NormalX=0 NormalY=0 NormalZ=1 AngleXU=0 Radius=18.65 StartAngle=1.00488 EndAngle=2.13672
    g5: ArcOfCircle CenterX=1.79506e-11 CenterY=260 CenterZ=0 NormalX=0 NormalY=0 NormalZ=1 AngleXU=0 Radius=5.5 StartAngle=2.13672 EndAngle=7.28806
    g6: LineSegment StartX=-2.94906 StartY=264.643 StartZ=0 EndX=-10 EndY=275.742 EndZ=0
    g7: LineSegment StartX=2.94906 StartY=264.643 StartZ=0 EndX=10 EndY=275.742 EndZ=0
    g8: ArcOfCircle CenterX=1.79506e-11 CenterY=260 CenterZ=0 NormalX=0 NormalY=0 NormalZ=1 AngleXU=0 Radius=9 StartAngle=2.58391 EndAngle=6.84087
    g9: ArcOfCircle CenterX=1.79506e-11 CenterY=260 CenterZ=0 NormalX=0 NormalY=0 NormalZ=1 AngleXU=0 Radius=16.5 StartAngle=2.58391 EndAngle=6.84087
    g10: LineSegment StartX=-14 StartY=268.732 StartZ=0 EndX=-7.63636 EndY=264.763 EndZ=0
    g11: LineSegment StartX=7.63636 StartY=264.763 StartZ=0 EndX=14 EndY=268.732 EndZ=0
  constraints (32):
    c: Coincident(g0,g-4)
    c: Coincident(g1,g-10)
    c: Coincident(g2,g-8)
    c: Coincident(g3,g-6)
    c: Equal(g1,g2)
    c: Equal(g1,g3)
    c: Equal(g1,g0)
    c: Diameter(g1) = 3.2
    c: Coincident(g4,g-11)
    c: PointOnObject(g4,g-11)
    c: Horizontal(g4,g4)
    c: DistanceX(g4,g4) = 20
    c: Coincident(g5,g4)
    c: Horizontal(g5,g5)
    c: Diameter(g5) = 11
    c: Coincident(g6,g5)
    c: Coincident(g6,g4)
    c: Coincident(g7,g5)
    c: Coincident(g7,g4)
    c: PointOnObject(g4,g7)
    c: Coincident(g8,g4)
    c: Coincident(g9,g4)
    c: Coincident(g10,g8)
    c: Coincident(g11,g8)
    c: Coincident(g11,g9)
    c: Coincident(g9,g10)
    c: PointOnObject(g4,g11)
    c: PointOnObject(g4,g10)
    c: Horizontal(g8,g8)
    c: Diameter(g8) = 18
    c: Diameter(g9) = 33
    c: DistanceX(g9,g9) = 28
FEATURE [PartDesign::Pad] Pad024
  AddSubType = 0
  AlongSketchNormal = false
  AutoTaperInnerAngle = true
  CheckUpToFaceLimits = true
  ClaimChildren = false
  Direction = (0,1,2e-16)
  Fit = 0
  FitJoin = 0
  InnerFit = 0
  InnerFitJoin = 0
  Length = 3
  Length2 = 100
  Linearize = true
  NewSolid = false
  Profile = -> Sketch077
  Refine = true
  Suppress = false
  TaperInnerAngle = 0
  TaperInnerAngleRev = 0
  TreeRank = 386
  Type = 0
  _ProfileBasedVersion = 1
FEATURE [PartDesign::Fillet] Fillet010
  AddSubType = 0
  Base = -> Pad024 [Edge26,Edge25,Edge41,Edge44,Edge29,Edge32,Edge37,Edge38]
  BaseFeature = -> Pad024
  NewSolid = false
  Radius = 2
  Refine = true
  SupportTransform = false
  Suppress = false
  TreeRank = 387
FEATURE [PartDesign::Body] Body009  label="CacheTurbine"
  AutoGroupSolids = false
  ClaimAllChildren = false
  ExportMode = 0
  Group = -> [Binder003,Sketch077,Pad024,Fillet010]
  Origin = -> Origin011
  SingleSolid = true
  Tip = -> Fillet010
  TreeRank = 382
  _ExportChildren = -> [Binder003,Pad024,Fillet010]
  _GroupVersion = 1
FEATURE [TechDraw::DrawSVGTemplate] Template
  Height = 210
  Orientation = 1
  TreeRank = 389
  Width = 297
FEATURE [TechDraw::DrawProjGroupItem] ProjItem  label="Front"
  CoarseView = false
  Direction = (0,1,0)
  Focus = 100
  HardHidden = false
  IsoCount = 0
  IsoHidden = false
  IsoVisible = false
  LockPosition = true
  Perspective = false
  Rotation = 0
  RotationVector = (1,0,0)
  ScaleType = 2
  SeamHidden = false
  SeamVisible = true
  SmoothHidden = false
  SmoothVisible = true
  Source = -> [Fillet010]
  TreeRank = 392
  Type = 0
  X = 0
  XDirection = (1,0,0)
  Y = 0
FEATURE [TechDraw::DrawProjGroup] ProjGroup
  Anchor = -> ProjItem
  AutoDistribute = true
  LockPosition = false
  ProjectionType = 0
  Rotation = 0
  ScaleType = 0
  Source = -> [Fillet010]
  TreeRank = 393
  Views = -> [ProjItem]
  X = 26.388
  Y = 184.2
  spacingX = 15
  spacingY = 15
FEATURE [TechDraw::DrawPage] Page  label="CacheTurbine3mmLaser"
  KeepUpdated = true
  NextBalloonIndex = 1
  ProjectionType = 0
  Template = -> Template
  TreeRank = 390
  Views = -> [ProjGroup]
FEATURE [Part::SubShapeBinder] Import003  label="Import003(Chamfer)"
  BindCopyOnChange = 0
  BindMode = 0
  ClaimChildren = false
  Context = -> Part [Body010.Import003.]
  EdgeTolerance = 1e-06
  FillStyle = 0
  Fuse = false
  MakeFace = false
  MergeEdges = true
  OffsetFill = false
  OffsetIntersection = false
  OffsetJoinType = 0
  OffsetOpenResult = false
  Outline = false
  PartialLoad = false
  Relative = true
  SplitEdges = false
  Support = -> [Body006[Chamfer.]]
  TightBound = false
  TreeRank = 405
  _Version = 8
FEATURE [Sketcher::SketchObject] Sketch078
  ArcFitTolerance = 1e-06
  AttachmentSupport = -> [YZ_Plane010]
  ExternalBSplineMaxDegree = 5
  ExternalBSplineTolerance = 0.0001
  ExternalGeometry = -> [Import003]
  FullyConstrained = true
  InternalTolerance = 1e-06
  MakeInternals = true
  MapMode = 5
  Placement = pos=(0,0,0) rot=(0.57735,0.57735,0.57735;2.0944rad)
  Support = -> [YZ_Plane010]
  TreeRank = 404
  sketch-geometry (4):
    g0: LineSegment StartX=-24.9 StartY=261.05 StartZ=0 EndX=-20.1 EndY=261.05 EndZ=0
    g1: LineSegment StartX=-20.1 StartY=261.05 StartZ=0 EndX=-20.1 EndY=258.95 EndZ=0
    g2: LineSegment StartX=-20.1 StartY=258.95 StartZ=0 EndX=-24.9 EndY=258.95 EndZ=0
    g3: LineSegment StartX=-24.9 StartY=258.95 StartZ=0 EndX=-24.9 EndY=261.05 EndZ=0
  constraints (12):
    c: Coincident(g0,g1)
    c: Coincident(g1,g2)
    c: Coincident(g2,g3)
    c: Coincident(g3,g0)
    c: Horizontal(g0)
    c: Horizontal(g2)
    c: Vertical(g1)
    c: Vertical(g3)
    c: DistanceX(g0,g-3) = 0.1
    c: DistanceX(g-3,g0) = 0.1
    c: DistanceY(g0,g-3) = 0.1
    c: DistanceY(g-4,g1) = 0.1
FEATURE [PartDesign::Pad] Pad025
  AddSubType = 0
  AlongSketchNormal = false
  AutoTaperInnerAngle = true
  CheckUpToFaceLimits = true
  ClaimChildren = false
  Direction = (1,-2e-16,3e-16)
  Fit = 0
  FitJoin = 0
  InnerFit = 0
  InnerFitJoin = 0
  Length = 50
  Length2 = 100
  Linearize = true
  Midplane = true
  NewSolid = false
  Profile = -> Sketch078
  Refine = true
  Suppress = false
  TaperInnerAngle = 0
  TaperInnerAngleRev = 0
  TreeRank = 406
  Type = 0
  _ProfileBasedVersion = 1
FEATURE [PartDesign::Chamfer] Chamfer022
  AddSubType = 0
  Angle = 45
  Base = -> Pad025 [Edge7,Edge12,Edge6,Edge11]
  BaseFeature = -> Pad025
  ChamferType = 0
  FlipDirection = false
  NewSolid = false
  Refine = true
  Size = 1
  Size2 = 1
  SupportTransform = false
  Suppress = false
  TreeRank = 407
FEATURE [PartDesign::Body] Body010  label="LamelleTurbine"
  AutoGroupSolids = false
  ClaimAllChildren = false
  ExportMode = 0
  Group = -> [Sketch078,Import003,Pad025,Chamfer022]
  Origin = -> Origin012
  SingleSolid = true
  Tip = -> Chamfer022
  TreeRank = 403
  _ExportChildren = -> [Import003,Pad025,Chamfer022]
  _GroupVersion = 1
FEATURE [TechDraw::DrawSVGTemplate] Template001
  Height = 210
  Orientation = 1
  TreeRank = 409
  Width = 297
FEATURE [TechDraw::DrawProjGroupItem] ProjItem001  label="Front001"
  CoarseView = false
  Direction = (0,0,1)
  Focus = 100
  HardHidden = false
  IsoCount = 0
  IsoHidden = false
  IsoVisible = false
  LockPosition = true
  Perspective = false
  Rotation = 0
  RotationVector = (0,-1,0)
  ScaleType = 2
  SeamHidden = false
  SeamVisible = true
  SmoothHidden = false
  SmoothVisible = true
  Source = -> [Chamfer022]
  TreeRank = 412
  Type = 0
  X = 0
  XDirection = (0,-1,0)
  Y = 0
FEATURE [TechDraw::DrawProjGroup] ProjGroup001
  Anchor = -> ProjItem001
  AutoDistribute = true
  LockPosition = false
  ProjectionType = 0
  Rotation = 0
  ScaleType = 0
  Source = -> [Chamfer022]
  TreeRank = 413
  Views = -> [ProjItem001]
  X = 9.78
  Y = 181.8
  spacingX = 15
  spacingY = 15
FEATURE [TechDraw::DrawPage] Page001  label="LamelleTurbine2mmLaser"
  KeepUpdated = true
  NextBalloonIndex = 1
  ProjectionType = 0
  Template = -> Template001
  TreeRank = 410
  Views = -> [ProjGroup001]
FEATURE [Sketcher::SketchObject] Sketch079
  ArcFitTolerance = 1e-06
  AttachmentSupport = -> [XZ_Plane005]
  ExternalBSplineMaxDegree = 5
  ExternalBSplineTolerance = 0.0001
  FullyConstrained = true
  InternalTolerance = 1e-06
  MakeInternals = true
  MapMode = 5
  Placement = pos=(0,0,0) rot=(0,0.707107,0.707107;3.14159rad)
  Support = -> [XZ_Plane005]
  TreeRank = 414
  sketch-geometry (8):
    g0: LineSegment StartX=-16 StartY=314 StartZ=0 EndX=-4 EndY=314 EndZ=0
    g1: LineSegment StartX=-4 StartY=314 StartZ=0 EndX=-4 EndY=295 EndZ=0
    g2: LineSegment StartX=-4 StartY=295 StartZ=0 EndX=-16 EndY=295 EndZ=0
    g3: LineSegment StartX=-16 StartY=295 StartZ=0 EndX=-16 EndY=314 EndZ=0
    g4: LineSegment StartX=4 StartY=314 StartZ=0 EndX=16 EndY=314 EndZ=0
    g5: LineSegment StartX=16 StartY=314 StartZ=0 EndX=16 EndY=295 EndZ=0
    g6: LineSegment StartX=16 StartY=295 StartZ=0 EndX=4 EndY=295 EndZ=0
    g7: LineSegment StartX=4 StartY=295 StartZ=0 EndX=4 EndY=314 EndZ=0
  constraints (23):
    c: Coincident(g0,g1)
    c: Coincident(g1,g2)
    c: Coincident(g2,g3)
    c: Coincident(g3,g0)
    c: Horizontal(g0)
    c: Horizontal(g2)
    c: Vertical(g1)
    c: Vertical(g3)
    c: Coincident(g4,g5)
    c: Coincident(g5,g6)
    c: Coincident(g6,g7)
    c: Coincident(g7,g4)
    c: Horizontal(g4)
    c: Horizontal(g6)
    c: Vertical(g5)
    c: Vertical(g7)
    c: Equal(g7,g1)
    c: Equal(g4,g0)
    c: Symmetric(g4,g0,g-2)
    c: DistanceY(g3,g3) = 19
    c: DistanceX(g0,g0) = 12
    c: DistanceX(g0,g4) = 8
    c: DistanceY(g2) = 295
FEATURE [TechDraw::DrawSVGTemplate] Template002
  Height = 210
  Orientation = 1
  TreeRank = 424
  Width = 297
FEATURE [PartDesign::Pad] Pad026
  AddSubType = 0
  AlongSketchNormal = false
  AutoTaperInnerAngle = true
  BaseFeature = -> Pipe021
  CheckUpToFaceLimits = true
  ClaimChildren = false
  Direction = (0,1,3e-16)
  Fit = 0
  FitJoin = 0
  InnerFit = 0
  InnerFitJoin = 0
  Length = 10
  Length2 = 100
  Linearize = true
  NewSolid = false
  Profile = -> Pipe021 [Face59]
  Refine = true
  Suppress = false
  TaperInnerAngle = 0
  TaperInnerAngleRev = 0
  TreeRank = 429
  Type = 0
  _ProfileBasedVersion = 1
FEATURE [Sketcher::SketchObject] Sketch082
  ArcFitTolerance = 1e-06
  AttachmentSupport = -> [YZ_Plane]
  ExternalBSplineMaxDegree = 5
  ExternalBSplineTolerance = 0.0001
  ExternalGeometry = -> [Pad026]
  FullyConstrained = true
  InternalTolerance = 1e-06
  MakeInternals = true
  MapMode = 5
  Placement = pos=(0,0,0) rot=(0.57735,0.57735,0.57735;2.0944rad)
  Support = -> [YZ_Plane]
  TreeRank = 430
  sketch-geometry (4):
    g0: LineSegment StartX=29 StartY=175.985 StartZ=0 EndX=24.7143 EndY=195.985 EndZ=0
    g1: LineSegment StartX=24.7143 StartY=195.985 StartZ=0 EndX=42 EndY=195.985 EndZ=0
    g2: LineSegment StartX=42 StartY=195.985 StartZ=0 EndX=42 EndY=175.985 EndZ=0
    g3: LineSegment StartX=29 StartY=175.985 StartZ=0 EndX=42 EndY=175.985 EndZ=0
  constraints (11):
    c: Coincident(g1,g0)
    c: Horizontal(g1)
    c: Coincident(g2,g1)
    c: Vertical(g2)
    c: Coincident(g3,g0)
    c: Coincident(g3,g2)
    c: Symmetric(g-3,g-3,g3)
    c: PointOnObject(g-4,g0)
    c: PointOnObject(g2,g-3)
    c: DistanceX(g0,g-4) = 3
    c: DistanceY(g2,g2) = 20
FEATURE [PartDesign::Pocket] Pocket030
  AddSubType = 1
  AutoTaperInnerAngle = true
  BaseFeature = -> Pad026
  CheckUpToFaceLimits = true
  ClaimChildren = false
  Fit = 0
  FitJoin = 0
  InnerFit = 0
  InnerFitJoin = 0
  Length = 5
  Length2 = 100
  Linearize = true
  Midplane = true
  NewSolid = false
  Profile = -> Sketch082
  Refine = true
  Suppress = false
  TaperInnerAngle = 0
  TaperInnerAngleRev = 0
  TreeRank = 431
  Type = 1
  _ProfileBasedVersion = 1
  _Version = 1
FEATURE [PartDesign::Fillet] Fillet013
  AddSubType = 0
  Base = -> Pocket030 [Edge191,Edge182]
  BaseFeature = -> Pocket030
  NewSolid = false
  Radius = 5
  Refine = true
  SupportTransform = false
  Suppress = false
  TreeRank = 432
FEATURE [Sketcher::SketchObject] Sketch083
  ArcFitTolerance = 1e-06
  AttachmentSupport = -> [YZ_Plane]
  ExternalBSplineMaxDegree = 5
  ExternalBSplineTolerance = 0.0001
  ExternalGeometry = -> [Fillet013]
  FullyConstrained = true
  InternalTolerance = 1e-06
  MakeInternals = true
  MapMode = 5
  Placement = pos=(0,0,0) rot=(0.57735,0.57735,0.57735;2.0944rad)
  Support = -> [YZ_Plane]
  TreeRank = 433
  sketch-geometry (5):
    g0: LineSegment StartX=-3.449e-13 StartY=212.978 StartZ=0 EndX=1.689e-13 EndY=235.37 EndZ=0
    g1: LineSegment StartX=1.689e-13 StartY=235.37 StartZ=0 EndX=17.0513 EndY=231.746 EndZ=0
    g2: LineSegment StartX=17.0513 StartY=231.746 StartZ=0 EndX=25.5417 EndY=192.124 EndZ=0
    g3: LineSegment StartX=25.5417 StartY=192.124 StartZ=0 EndX=5 EndY=195.746 EndZ=0
    g4: LineSegment StartX=5 StartY=195.746 StartZ=0 EndX=5 EndY=212.978 EndZ=0
  constraints (13):
    c: Coincident(g0,g-3)
    c: PointOnObject(g0,g-2)
    c: Coincident(g1,g0)
    c: Coincident(g2,g1)
    c: Coincident(g3,g2)
    c: Coincident(g4,g3)
    c: Coincident(g4,g-3)
    c: Vertical(g4)
    c: Parallel(g3,g-4)
    c: Tangent(g-5,g2)
    c: DistanceY(g3,g-4) = 1
    c: DistanceY(g-4,g1) = 35
    c: Angle(g0,g1) = 1.36136
FEATURE [PartDesign::Pad] Pad027
  AddSubType = 0
  AlongSketchNormal = false
  AutoTaperInnerAngle = true
  BaseFeature = -> Fillet013
  CheckUpToFaceLimits = true
  ClaimChildren = false
  Direction = (1,-2e-16,3e-16)
  Fit = 0
  FitJoin = 0
  InnerFit = 0
  InnerFitJoin = 0
  Length = 5
  Length2 = 100
  Linearize = true
  Midplane = true
  NewSolid = false
  Profile = -> Sketch083
  Refine = true
  Suppress = false
  TaperInnerAngle = 0
  TaperInnerAngleRev = 0
  TreeRank = 434
  Type = 0
  _ProfileBasedVersion = 1
FEATURE [Sketcher::SketchObject] Sketch084
  ArcFitTolerance = 1e-06
  AttachmentSupport = -> [YZ_Plane]
  ExternalBSplineMaxDegree = 5
  ExternalBSplineTolerance = 0.0001
  ExternalGeometry = -> [Pad027]
  FullyConstrained = true
  InternalTolerance = 1e-06
  MakeInternals = true
  MapMode = 5
  Placement = pos=(0,0,0) rot=(0.57735,0.57735,0.57735;2.0944rad)
  Support = -> [YZ_Plane]
  TreeRank = 435
  sketch-geometry (8):
    g0: LineSegment StartX=18.1227 StartY=226.746 StartZ=0 EndX=6.12268 EndY=226.746 EndZ=0
    g1: LineSegment StartX=6.12268 StartY=226.746 StartZ=0 EndX=6.12268 EndY=203.746 EndZ=0
    g2: LineSegment StartX=6.12268 StartY=203.746 StartZ=0 EndX=23.0513 EndY=203.746 EndZ=0
    g3: LineSegment StartX=18.1227 StartY=226.746 StartZ=0 EndX=23.0513 EndY=203.746 EndZ=0
    g4: Circle CenterX=12.1227 CenterY=229.246 CenterZ=0 NormalX=0 NormalY=0 NormalZ=1 AngleXU=0 Radius=1.25
    g5: Circle CenterX=12.1227 CenterY=201.246 CenterZ=0 NormalX=0 NormalY=0 NormalZ=1 AngleXU=0 Radius=1.25
    g6: LineSegment [constr] StartX=12.1227 StartY=229.246 StartZ=0 EndX=12.1227 EndY=201.246 EndZ=0
    g7: LineSegment [constr] StartX=12.1227 StartY=215.246 StartZ=0 EndX=6.12268 EndY=215.246 EndZ=0
  constraints (22):
    c: PointOnObject(g0,g-3)
    c: Horizontal(g0)
    c: Coincident(g1,g0)
    c: Vertical(g1)
    c: Coincident(g2,g1)
    c: PointOnObject(g2,g-3)
    c: Horizontal(g2)
    c: DistanceY(g1,g1) = 23
    c: DistanceY(g0,g-4) = 5
    c: Coincident(g3,g0)
    c: Coincident(g3,g2)
    c: DistanceX(g0,g0) = 12
    c: Vertical(g5,g4)
    c: Equal(g4,g5)
    c: Diameter(g4) = 2.5
    c: Coincident(g6,g4)
    c: Coincident(g6,g5)
    c: Horizontal(g7)
    c: Symmetric(g5,g4,g7)
    c: DistanceX(g0,g4) = 6
    c: DistanceY(g6,g6) = 28
    c: Symmetric(g1,g0,g7)
FEATURE [PartDesign::Pocket] Pocket031
  AddSubType = 1
  AutoTaperInnerAngle = true
  BaseFeature = -> Pad027
  CheckUpToFaceLimits = true
  ClaimChildren = false
  Fit = 0
  FitJoin = 0
  InnerFit = 0
  InnerFitJoin = 0
  Length = 5
  Length2 = 100
  Linearize = true
  Midplane = true
  NewSolid = false
  Profile = -> Sketch084
  Refine = true
  Suppress = false
  TaperInnerAngle = 0
  TaperInnerAngleRev = 0
  TreeRank = 436
  Type = 1
  _ProfileBasedVersion = 1
  _Version = 1
FEATURE [PartDesign::Fillet] Fillet014
  AddSubType = 0
  Base = -> Pocket031 [Edge84,Edge104]
  BaseFeature = -> Pocket031
  NewSolid = false
  Radius = 10
  Refine = true
  SupportTransform = false
  Suppress = false
  TreeRank = 437
FEATURE [PartDesign::Fillet] Fillet015
  AddSubType = 0
  Base = -> Fillet014 [Edge59]
  BaseFeature = -> Fillet014
  NewSolid = false
  Radius = 3
  Refine = true
  SupportTransform = false
  Suppress = false
  TreeRank = 438
FEATURE [PartDesign::Fillet] Fillet016
  AddSubType = 0
  Base = -> Fillet015 [Edge55,Edge69]
  BaseFeature = -> Fillet015
  NewSolid = false
  Radius = 2
  Refine = true
  SupportTransform = false
  Suppress = false
  TreeRank = 439
FEATURE [Sketcher::SketchObject] Sketch085
  ArcFitTolerance = 1e-06
  AttachmentSupport = -> [YZ_Plane]
  ExternalBSplineMaxDegree = 5
  ExternalBSplineTolerance = 0.0001
  ExternalGeometry = -> [Fillet016]
  FullyConstrained = true
  InternalTolerance = 1e-06
  MakeInternals = true
  MapMode = 5
  Placement = pos=(0,0,0) rot=(0.57735,0.57735,0.57735;2.0944rad)
  Support = -> [YZ_Plane]
  TreeRank = 440
  sketch-geometry (6):
    g0: Circle CenterX=28.3513 CenterY=194.284 CenterZ=0 NormalX=0 NormalY=0 NormalZ=1 AngleXU=0 Radius=1.6
    g1: ArcOfCircle CenterX=28.3513 CenterY=194.284 CenterZ=0 NormalX=0 NormalY=0 NormalZ=1 AngleXU=0 Radius=3.2 StartAngle=4.71239 EndAngle=7.53339
    g2: LineSegment StartX=29.3597 StartY=197.321 StartZ=0 EndX=24.0501 EndY=199.084 EndZ=0
    g3: LineSegment StartX=25.7644 StartY=191.084 StartZ=0 EndX=28.3513 EndY=191.084 EndZ=0
    g4: LineSegment StartX=25.7644 StartY=191.084 StartZ=0 EndX=24.0501 EndY=199.084 EndZ=0
    g5: Circle [constr] CenterX=28.3513 CenterY=194.284 CenterZ=0 NormalX=0 NormalY=0 NormalZ=1 AngleXU=0 Radius=3.2
  constraints (14):
    c: Diameter(g0) = 3.2
    c: Tangent(g1,g2) = -1.5708
    c: Tangent(g3,g1) = -1.5708
    c: Coincident(g1,g0)
    c: Horizontal(g3)
    c: Coincident(g4,g3)
    c: Coincident(g4,g2)
    c: Coincident(g3,g-5)
    c: PointOnObject(g2,g-4)
    c: Radius(g1) = 3.2
    c: Coincident(g5,g0)
    c: PointOnObject(g1,g5)
    c: Tangent(g5,g4)
    c: DistanceY(g3,g2) = 8
FEATURE [PartDesign::Pad] Pad028
  AddSubType = 0
  AlongSketchNormal = false
  AutoTaperInnerAngle = true
  BaseFeature = -> Fillet016
  CheckUpToFaceLimits = true
  ClaimChildren = false
  Direction = (1,-2e-16,3e-16)
  Fit = 0
  FitJoin = 0
  InnerFit = 0
  InnerFitJoin = 0
  Length = 5
  Length2 = 100
  Linearize = true
  Midplane = true
  NewSolid = false
  Profile = -> Sketch085
  Refine = true
  Suppress = false
  TaperInnerAngle = 0
  TaperInnerAngleRev = 0
  TreeRank = 441
  Type = 0
  _ProfileBasedVersion = 1
FEATURE [PartDesign::Fillet] Fillet017
  AddSubType = 0
  Base = -> Pad028 [Edge73]
  BaseFeature = -> Pad028
  NewSolid = false
  Radius = 2
  Refine = true
  SupportTransform = false
  Suppress = false
  TreeRank = 442
FEATURE [PartDesign::Chamfer] Chamfer024
  AddSubType = 0
  Angle = 45
  Base = -> Fillet017 [Edge45,Edge46,Edge23,Edge24,Edge44,Edge22]
  BaseFeature = -> Fillet017
  ChamferType = 0
  FlipDirection = false
  NewSolid = false
  Refine = true
  Size = 0.4
  Size2 = 1
  SupportTransform = false
  Suppress = false
  TreeRank = 443
FEATURE [PartDesign::Body] Body  label="TubeExterne"
  AutoGroupSolids = false
  ClaimAllChildren = false
  ExportMode = 0
  Group = -> [Binder001,Sketch059,Sketch060,Pipe,Sketch061,Pocket021,Sketch064,Import,Sketch062,Sketch065,Pad,Pad017,Pipe019,Sketch066,Pad018,Sketch067,Pocket022,Fillet,Chamfer015,Pocket023,Sketch068,DatumLine,Groove,Fillet007,Pipe020,Sketch069,Pipe021,Pad026,Sketch082,Pocket030,Fillet013,Sketch083,Pad027,Sketch084,Pocket031,Fillet014,Fillet015,Fillet016,Sketch085,Pad028,Fillet017,Chamfer024]
  Origin = -> Origin
  SingleSolid = true
  Tip = -> Chamfer024
  TreeRank = 293
  _ExportChildren = -> [Pipe,Pocket021,Import,Pad,Pad017,Pipe019,Pad018,Pocket022,Fillet,Chamfer015,Pocket023,DatumLine,Groove,Fillet007,Pipe020,Pipe021,Pad026,Pocket030,Fillet013,Pad027,Pocket031,Fillet014,Fillet015,Fillet016,Pad028,Fillet017,Chamfer024]
  _GroupVersion = 1
FEATURE [PartDesign::SubShapeBinder] Binder004  label="Binder004(Pipe021)"
  BindCopyOnChange = 0
  BindMode = 0
  ClaimChildren = false
  Context = -> <external ../table.FCStd>#Group [Link.Group002.Link017.Body011.Binder004.]
  EdgeTolerance = 1e-06
  FillStyle = 0
  Fuse = false
  MakeFace = true
  MergeEdges = true
  OffsetFill = false
  OffsetIntersection = false
  OffsetJoinType = 0
  OffsetOpenResult = false
  Outline = false
  PartialLoad = false
  Relative = true
  SplitEdges = false
  Support = -> [Body[Pipe021.Face59]]
  TightBound = false
  TreeRank = 454
  _Version = 8
FEATURE [PartDesign::SubShapeBinder] Binder005  label="Binder005(Chamfer024)..."
  BindCopyOnChange = 0
  BindMode = 0
  ClaimChildren = false
  Context = -> <external ../table.FCStd>#Group [Link.Group002.Link017.Body011.Binder005.]
  EdgeTolerance = 1e-06
  FillStyle = 0
  Fuse = false
  MakeFace = true
  MergeEdges = true
  OffsetFill = false
  OffsetIntersection = false
  OffsetJoinType = 0
  OffsetOpenResult = false
  Outline = false
  PartialLoad = false
  Relative = true
  SplitEdges = false
  Support = -> [Body[Chamfer024.Face12,Chamfer024.Face63]]
  TightBound = false
  TreeRank = 455
  _Version = 8
FEATURE [PartDesign::SubShapeBinder] Binder006  label="Binder006(Chamfer024)"
  BindCopyOnChange = 0
  BindMode = 0
  ClaimChildren = false
  Context = -> <external ../table.FCStd>#Group [Link.Group002.Link017.Body011.Binder006.]
  EdgeTolerance = 1e-06
  FillStyle = 0
  Fuse = false
  MakeFace = true
  MergeEdges = true
  OffsetFill = false
  OffsetIntersection = false
  OffsetJoinType = 0
  OffsetOpenResult = false
  Outline = false
  PartialLoad = false
  Relative = true
  SplitEdges = false
  Support = -> [Body[Chamfer024.Face24]]
  TightBound = false
  TreeRank = 456
  _Version = 8
FEATURE [PartDesign::Plane] DatumPlane
  AttachmentSupport = -> [Binder005]
  Length = 60
  MapMode = 5
  MinimumLength = 10
  MinimumWidth = 10
  Placement = pos=(-4e-16,-3.1268,-0.670029) rot=(0,0.628678,0.777666;3.14159rad)
  ResizeMode = 0
  Support = -> [Binder005]
  TreeRank = 457
  Width = 80.4167
FEATURE [Sketcher::SketchObject] Sketch086
  ArcFitTolerance = 1e-06
  AttachmentSupport = -> [DatumPlane]
  ExternalBSplineMaxDegree = 5
  ExternalBSplineTolerance = 0.0001
  ExternalGeometry = -> [Binder005]
  FullyConstrained = false
  InternalTolerance = 1e-06
  MakeInternals = true
  MapMode = 5
  Placement = pos=(-4e-16,-3.1268,-0.670029) rot=(0,0.628678,0.777666;3.14159rad)
  Support = -> [DatumPlane]
  TreeRank = 458
  sketch-geometry (9):
    g0: LineSegment StartX=-14 StartY=-0.457175 StartZ=0 EndX=14 EndY=-0.457175 EndZ=0
    g1: ArcOfCircle CenterX=-14 CenterY=-16.4848 CenterZ=0 NormalX=0 NormalY=0 NormalZ=1 AngleXU=0 Radius=16.0276 StartAngle=1.5708 EndAngle=3.2003
    g2: LineSegment StartX=-30 StartY=-17.4252 StartZ=0 EndX=-27.8 EndY=-17.4252 EndZ=0
    g3: ArcOfCircle CenterX=14 CenterY=-16.4848 CenterZ=0 NormalX=0 NormalY=0 NormalZ=1 AngleXU=0 Radius=16.0276 StartAngle=6.22448 EndAngle=7.85398
    g4: LineSegment StartX=30 StartY=-17.4252 StartZ=0 EndX=27.8 EndY=-17.4252 EndZ=0
    g5: ArcOfCircle CenterX=-13.22 CenterY=-17.4252 CenterZ=0 NormalX=0 NormalY=0 NormalZ=1 AngleXU=0 Radius=14.58 StartAngle=3.14159 EndAngle=4.71239
    g6: LineSegment [constr] StartX=-27.8 StartY=-17.4252 StartZ=0 EndX=-27.8 EndY=-32.0818 EndZ=0
    g7: ArcOfCircle CenterX=13.22 CenterY=-17.4252 CenterZ=0 NormalX=0 NormalY=0 NormalZ=1 AngleXU=0 Radius=14.58 StartAngle=4.71239 EndAngle=6.28319
    g8: LineSegment StartX=-13.22 StartY=-32.0052 StartZ=0 EndX=13.22 EndY=-32.0052 EndZ=0
  constraints (22):
    c: Coincident(g0,g-6)
    c: Coincident(g2,g1)
    c: Horizontal(g2)
    c: Coincident(g4,g3)
    c: Horizontal(g4)
    c: DistanceY(g-7,g1) = 0.6
    c: Symmetric(g3,g1,g-2)
    c: Tangent(g3,g0) = 1.5708
    c: Coincident(g5,g2)
    c: Coincident(g6,g2)
    c: Vertical(g6)
    c: Tangent(g6,g5)
    c: DistanceX(g2,g2) = 2.2
    c: DistanceX(g1) = -30
    c: Equal(g4,g2)
    c: Coincident(g7,g4)
    c: Tangent(g8,g7) = -1.5708
    c: Tangent(g8,g5) = -1.5708
    c: Symmetric(g7,g5,g-2)
    c: Tangent(g1,g0) = 1.5708
    c: Coincident(g0,g-5)
    c: Radius(g7) = 14.58
FEATURE [PartDesign::Pad] Pad029
  AddSubType = 0
  AlongSketchNormal = false
  AutoTaperInnerAngle = true
  CheckUpToFaceLimits = true
  ClaimChildren = false
  Direction = (1e-16,0.977802,0.209529)
  Fit = 0
  FitJoin = 0
  InnerFit = 0
  InnerFitJoin = 0
  Length = 3
  Length2 = 100
  Linearize = true
  NewSolid = false
  Profile = -> Sketch086
  Refine = true
  Suppress = false
  TaperInnerAngle = 0
  TaperInnerAngleRev = 0
  TreeRank = 459
  Type = 0
  _ProfileBasedVersion = 1
FEATURE [Sketcher::SketchObject] Sketch087
  ArcFitTolerance = 1e-06
  AttachmentSupport = -> [YZ_Plane011]
  ExternalBSplineMaxDegree = 5
  ExternalBSplineTolerance = 0.0001
  ExternalGeometry = -> [Pad029,Binder005]
  FullyConstrained = true
  InternalTolerance = 1e-06
  MakeInternals = true
  MapMode = 5
  Placement = pos=(0,0,0) rot=(0.57735,0.57735,0.57735;2.0944rad)
  Support = -> [YZ_Plane011]
  TreeRank = 460
  sketch-geometry (2):
    g0: Circle [constr] CenterX=0 CenterY=0 CenterZ=0 NormalX=0 NormalY=0 NormalZ=1 AngleXU=0 Radius=1.6
    g1: Circle CenterX=0 CenterY=0 CenterZ=0 NormalX=0 NormalY=0 NormalZ=1 AngleXU=0 Radius=3.2
  constraints (4):
    c: Coincident(g0,g-1)
    c: Coincident(g1,g0)
    c: Diameter(g1) = 6.4
    c: Diameter(g0) = 3.2
FEATURE [PartDesign::Pocket] Pocket032
  AddSubType = 1
  AutoTaperInnerAngle = true
  BaseFeature = -> Pad029
  CheckUpToFaceLimits = true
  ClaimChildren = false
  Fit = 0
  FitJoin = 0
  InnerFit = 0
  InnerFitJoin = 0
  Length = 5
  Length2 = 100
  Linearize = true
  Midplane = true
  NewSolid = false
  Profile = -> Sketch087
  Refine = true
  Suppress = false
  TaperInnerAngle = 0
  TaperInnerAngleRev = 0
  TreeRank = 461
  Type = 1
  _ProfileBasedVersion = 1
  _Version = 1
FEATURE [PartDesign::Pad] Pad030
  AddSubType = 0
  AlongSketchNormal = false
  AutoTaperInnerAngle = true
  BaseFeature = -> Pocket032
  CheckUpToFaceLimits = true
  ClaimChildren = false
  Direction = (1,-2e-16,3e-16)
  Fit = 0
  FitJoin = 0
  InnerFit = 0
  InnerFitJoin = 0
  Length = 20
  Length2 = 100
  Linearize = true
  Midplane = true
  NewSolid = false
  Profile = -> Sketch087
  Refine = true
  Suppress = false
  TaperInnerAngle = 0
  TaperInnerAngleRev = 0
  TreeRank = 462
  Type = 0
  _ProfileBasedVersion = 1
FEATURE [PartDesign::Fillet] Fillet018
  AddSubType = 0
  Base = -> Pad030 [Edge33]
  BaseFeature = -> Pad030
  NewSolid = false
  Radius = 3
  Refine = true
  SupportTransform = false
  Suppress = false
  TreeRank = 463
FEATURE [Sketcher::SketchObject] Sketch088
  ArcFitTolerance = 1e-06
  AttachmentSupport = -> [DatumPlane]
  ExternalBSplineMaxDegree = 5
  ExternalBSplineTolerance = 0.0001
  FullyConstrained = true
  InternalTolerance = 1e-06
  MakeInternals = true
  MapMode = 5
  Placement = pos=(-4e-16,-3.1268,-0.670029) rot=(0,0.628678,0.777666;3.14159rad)
  Support = -> [DatumPlane]
  TreeRank = 464
  sketch-geometry (4):
    g0: LineSegment StartX=-2.7 StartY=4.5 StartZ=0 EndX=2.7 EndY=4.5 EndZ=0
    g1: LineSegment StartX=2.7 StartY=4.5 StartZ=0 EndX=2.7 EndY=-4.5 EndZ=0
    g2: LineSegment StartX=2.7 StartY=-4.5 StartZ=0 EndX=-2.7 EndY=-4.5 EndZ=0
    g3: LineSegment StartX=-2.7 StartY=-4.5 StartZ=0 EndX=-2.7 EndY=4.5 EndZ=0
  constraints (10):
    c: Coincident(g0,g1)
    c: Coincident(g1,g2)
    c: Coincident(g2,g3)
    c: Coincident(g3,g0)
    c: Horizontal(g2)
    c: Vertical(g3)
    c: Symmetric(g0,g0,g-2)
    c: DistanceX(g0,g0) = 5.4
    c: Symmetric(g1,g0,g-1)
    c: DistanceY(g1,g1) = 9
FEATURE [PartDesign::Pocket] Pocket033
  AddSubType = 1
  AutoTaperInnerAngle = true
  BaseFeature = -> Fillet018
  CheckUpToFaceLimits = true
  ClaimChildren = false
  Fit = 0
  FitJoin = 0
  InnerFit = 0
  InnerFitJoin = 0
  Length = 5
  Length2 = 100
  Linearize = true
  NewSolid = false
  Profile = -> Sketch088
  Refine = true
  Reversed = true
  Suppress = false
  TaperInnerAngle = 0
  TaperInnerAngleRev = 0
  TreeRank = 465
  Type = 1
  _ProfileBasedVersion = 1
  _Version = 1
FEATURE [PartDesign::Fillet] Fillet019
  AddSubType = 0
  Base = -> Pocket033 [Edge38,Edge27,Edge31,Edge42]
  BaseFeature = -> Pocket033
  NewSolid = false
  Radius = 1
  Refine = true
  SupportTransform = false
  Suppress = false
  TreeRank = 466
FEATURE [PartDesign::Chamfer] Chamfer025
  AddSubType = 0
  Angle = 45
  Base = -> Fillet019 [Edge74,Edge73]
  BaseFeature = -> Fillet019
  ChamferType = 0
  FlipDirection = false
  NewSolid = false
  Refine = true
  Size = 1
  Size2 = 1
  SupportTransform = false
  Suppress = false
  TreeRank = 467
FEATURE [Sketcher::SketchObject] Sketch089
  ArcFitTolerance = 1e-06
  AttachmentSupport = -> [YZ_Plane011]
  ExternalBSplineMaxDegree = 5
  ExternalBSplineTolerance = 0.0001
  FullyConstrained = true
  InternalTolerance = 1e-06
  MakeInternals = true
  MapMode = 5
  Placement = pos=(0,0,0) rot=(0.57735,0.57735,0.57735;2.0944rad)
  Support = -> [YZ_Plane011]
  TreeRank = 468
  sketch-geometry (1):
    g0: Circle CenterX=0 CenterY=0 CenterZ=0 NormalX=0 NormalY=0 NormalZ=1 AngleXU=0 Radius=1.6
  constraints (2):
    c: Coincident(g0,g-1)
    c: Diameter(g0) = 3.2
FEATURE [PartDesign::Pocket] Pocket034
  AddSubType = 1
  AutoTaperInnerAngle = true
  BaseFeature = -> Chamfer025
  CheckUpToFaceLimits = true
  ClaimChildren = false
  Fit = 0
  FitJoin = 0
  InnerFit = 0
  InnerFitJoin = 0
  Length = 5
  Length2 = 100
  Linearize = true
  Midplane = true
  NewSolid = false
  Profile = -> Sketch089
  Refine = true
  Suppress = false
  TaperInnerAngle = 0
  TaperInnerAngleRev = 0
  TreeRank = 469
  Type = 1
  _ProfileBasedVersion = 1
  _Version = 1
FEATURE [PartDesign::Chamfer] Chamfer026
  AddSubType = 0
  Angle = 45
  Base = -> Pocket034 [Edge34,Edge56,Edge54,Edge17]
  BaseFeature = -> Pocket034
  ChamferType = 0
  FlipDirection = false
  NewSolid = false
  Refine = true
  Size = 0.4
  Size2 = 1
  SupportTransform = false
  Suppress = false
  TreeRank = 470
FEATURE [PartDesign::Fillet] Fillet020
  AddSubType = 0
  Base = -> Chamfer026 [Edge82,Edge86]
  BaseFeature = -> Chamfer026
  NewSolid = false
  Radius = 3
  Refine = true
  SupportTransform = false
  Suppress = false
  TreeRank = 471
FEATURE [Part::SubShapeBinder] Import004  label="Import004(Chamfer024)"
  BindCopyOnChange = 0
  BindMode = 0
  ClaimChildren = false
  Context = -> <external ../table.FCStd>#Group [Link.Group002.Link017.Body011.Import004.]
  EdgeTolerance = 1e-06
  FillStyle = 0
  Fuse = false
  MakeFace = false
  MergeEdges = true
  OffsetFill = false
  OffsetIntersection = false
  OffsetJoinType = 0
  OffsetOpenResult = false
  Outline = false
  PartialLoad = false
  Relative = true
  SplitEdges = false
  Support = -> [Body[Chamfer024.]]
  TightBound = false
  TreeRank = 473
  _Version = 8
FEATURE [Sketcher::SketchObject] Sketch090
  ArcFitTolerance = 1e-06
  AttachmentSupport = -> [YZ_Plane011]
  ExternalBSplineMaxDegree = 5
  ExternalBSplineTolerance = 0.0001
  ExternalGeometry = -> [Fillet020,Import004]
  FullyConstrained = true
  InternalTolerance = 1e-06
  MakeInternals = true
  MapMode = 5
  Placement = pos=(0,0,0) rot=(0.57735,0.57735,0.57735;2.0944rad)
  Support = -> [YZ_Plane011]
  TreeRank = 472
  sketch-geometry (5):
    g0: LineSegment StartX=5.65605 StartY=-27.3388 StartZ=0 EndX=1.94058 EndY=-10 EndZ=0
    g1: LineSegment StartX=1.94058 StartY=-10 StartZ=0 EndX=9.77951 EndY=-8.32023 EndZ=0
    g2: ArcOfCircle CenterX=10.45 CenterY=-11.4492 CenterZ=0 NormalX=0 NormalY=0 NormalZ=1 AngleXU=0 Radius=3.2 StartAngle=5.79615 EndAngle=8.06507
    g3: LineSegment StartX=5.65605 StartY=-27.3388 StartZ=0 EndX=13.2779 EndY=-12.9468 EndZ=0
    g4: Circle CenterX=10.45 CenterY=-11.4492 CenterZ=0 NormalX=0 NormalY=0 NormalZ=1 AngleXU=0 Radius=1.6
  constraints (13):
    c: PointOnObject(g0,g-4)
    c: PointOnObject(g0,g-3)
    c: Coincident(g1,g0)
    c: Coincident(g3,g0)
    c: Tangent(g3,g2) = -1.5708
    c: Tangent(g2,g1) = 1.5708
    c: Coincident(g4,g2)
    c: Diameter(g4) = 3.2
    c: Radius(g2) = 3.2
    c: Tangent(g2,g-5)
    c: Perpendicular(g-3,g1)
    c: DistanceY(g0) = -10
    c: Angle(g1,g3) = 0.872665
FEATURE [PartDesign::Pad] Pad031
  AddSubType = 0
  AlongSketchNormal = false
  AutoTaperInnerAngle = true
  BaseFeature = -> Fillet020
  CheckUpToFaceLimits = true
  ClaimChildren = false
  Direction = (1,-2e-16,3e-16)
  Fit = 0
  FitJoin = 0
  InnerFit = 0
  InnerFitJoin = 0
  Length = 5
  Length2 = 100
  Linearize = true
  NewSolid = false
  Profile = -> Sketch090
  Refine = true
  Suppress = false
  TaperInnerAngle = 0
  TaperInnerAngleRev = 0
  TreeRank = 474
  Type = 0
  _ProfileBasedVersion = 1
FEATURE [PartDesign::Fillet] Fillet021
  AddSubType = 0
  Base = -> Pad031 [Edge23]
  BaseFeature = -> Pad031
  NewSolid = false
  Radius = 2
  Refine = true
  SupportTransform = false
  Suppress = false
  TreeRank = 475
FEATURE [PartDesign::Fillet] Fillet022
  AddSubType = 0
  Base = -> Fillet021 [Edge4]
  BaseFeature = -> Fillet021
  NewSolid = false
  Radius = 9
  Refine = true
  SupportTransform = false
  Suppress = false
  TreeRank = 476
FEATURE [PartDesign::Fillet] Fillet023
  AddSubType = 0
  Base = -> Fillet022 [Edge2]
  BaseFeature = -> Fillet022
  NewSolid = false
  Radius = 2
  Refine = true
  SupportTransform = false
  Suppress = false
  TreeRank = 477
FEATURE [PartDesign::Chamfer] Chamfer027
  AddSubType = 0
  Angle = 45
  Base = -> Fillet023 [Edge36,Edge93]
  BaseFeature = -> Fillet023
  ChamferType = 0
  FlipDirection = false
  NewSolid = false
  Refine = true
  Size = 0.4
  Size2 = 1
  SupportTransform = false
  Suppress = false
  TreeRank = 478
FEATURE [Sketcher::SketchObject] Sketch091
  ArcFitTolerance = 1e-06
  AttachmentSupport = -> [YZ_Plane012]
  ExternalBSplineMaxDegree = 5
  ExternalBSplineTolerance = 0.0001
  FullyConstrained = true
  InternalTolerance = 1e-06
  MakeInternals = true
  MapMode = 5
  Placement = pos=(0,0,0) rot=(0.57735,0.57735,0.57735;2.0944rad)
  Support = -> [YZ_Plane012]
  TreeRank = 523
  sketch-geometry (7):
    g0: ArcOfCircle CenterX=1.1618e-12 CenterY=6.7287e-12 CenterZ=0 NormalX=0 NormalY=0 NormalZ=1 AngleXU=0 Radius=3.45 StartAngle=1.48033 EndAngle=4.80286
    g1: LineSegment StartX=0.311682 StartY=3.43589 StartZ=0 EndX=16.2307 EndY=1.99182 EndZ=0
    g2: LineSegment StartX=0.311682 StartY=-3.43589 StartZ=0 EndX=16.2307 EndY=-1.99182 EndZ=0
    g3: ArcOfCircle CenterX=16.05 CenterY=-4.132e-13 CenterZ=0 NormalX=0 NormalY=0 NormalZ=1 AngleXU=0 Radius=2 StartAngle=4.80286 EndAngle=7.76352
    g4: GeomPoint [constr] X=-3.45 Y=-1.4e-15 Z=0
    g5: GeomPoint [constr] X=18.05 Y=0 Z=0
    g6: Circle CenterX=1.1618e-12 CenterY=6.7287e-12 CenterZ=0 NormalX=0 NormalY=0 NormalZ=1 AngleXU=0 Radius=1.1
  constraints (15):
    c: Coincident(g0,g-1)
    c: PointOnObject(g3,g-1)
    c: Tangent(g3,g1) = 1.5708
    c: Tangent(g3,g2) = -1.5708
    c: Tangent(g1,g0) = 1.5708
    c: Tangent(g2,g0) = -1.5708
    c: PointOnObject(g4,g0)
    c: PointOnObject(g5,g3)
    c: PointOnObject(g5,g-1)
    c: PointOnObject(g4,g-1)
    c: DistanceX(g4,g5) = 21.5
    c: Diameter(g0) = 6.9
    c: Diameter(g3) = 4
    c: Coincident(g6,g0)
    c: Diameter(g6) = 2.2
FEATURE [PartDesign::Pad] Pad032
  AddSubType = 0
  AlongSketchNormal = false
  AutoTaperInnerAngle = true
  CheckUpToFaceLimits = true
  ClaimChildren = false
  Direction = (1,-2e-16,3e-16)
  Fit = 0
  FitJoin = 0
  InnerFit = 0
  InnerFitJoin = 0
  Length = 2
  Length2 = 100
  Linearize = true
  NewSolid = false
  Profile = -> Sketch091
  Refine = true
  Suppress = false
  TaperInnerAngle = 0
  TaperInnerAngleRev = 0
  TreeRank = 524
  Type = 0
  _ProfileBasedVersion = 1
FEATURE [Sketcher::SketchObject] Sketch092
  ArcFitTolerance = 1e-06
  AttachmentSupport = -> [YZ_Plane012]
  ExternalBSplineMaxDegree = 5
  ExternalBSplineTolerance = 0.0001
  ExternalGeometry = -> [Pad032]
  FullyConstrained = true
  InternalTolerance = 1e-06
  MakeInternals = true
  MapMode = 5
  Placement = pos=(0,0,0) rot=(0.57735,0.57735,0.57735;2.0944rad)
  Support = -> [YZ_Plane012]
  TreeRank = 525
  sketch-geometry (2):
    g0: Circle CenterX=6.533e-13 CenterY=4.5832e-12 CenterZ=0 NormalX=0 NormalY=0 NormalZ=1 AngleXU=0 Radius=3.45
    g1: Circle CenterX=6.533e-13 CenterY=4.5832e-12 CenterZ=0 NormalX=0 NormalY=0 NormalZ=1 AngleXU=0 Radius=2.25
  constraints (4):
    c: Coincident(g0,g-3)
    c: PointOnObject(g-3,g0)
    c: Coincident(g1,g0)
    c: Diameter(g1) = 4.5
FEATURE [PartDesign::Pad] Pad033
  AddSubType = 0
  AlongSketchNormal = false
  AutoTaperInnerAngle = true
  BaseFeature = -> Pad032
  CheckUpToFaceLimits = true
  ClaimChildren = false
  Direction = (1,-2e-16,3e-16)
  Fit = 0
  FitJoin = 0
  InnerFit = 0
  InnerFitJoin = 0
  Length = 2
  Length2 = 100
  Linearize = true
  NewSolid = false
  Profile = -> Sketch092
  Refine = true
  Reversed = true
  Suppress = false
  TaperInnerAngle = 0
  TaperInnerAngleRev = 0
  TreeRank = 526
  Type = 0
  _ProfileBasedVersion = 1
FEATURE [PartDesign::Body] Body012  label="ServoArm"
  AutoGroupSolids = false
  ClaimAllChildren = false
  ExportMode = 0
  Group = -> [Sketch091,Pad032,Sketch092,Pad033]
  Origin = -> Origin014
  SingleSolid = true
  Tip = -> Pad033
  TreeRank = 512
  _ExportChildren = -> [Pad032,Pad033]
  _GroupVersion = 1
FEATURE [PartDesign::SubShapeBinder] Binder007  label="Binder007(Pad033)"
  BindCopyOnChange = 0
  BindMode = 0
  ClaimChildren = false
  Context = -> <external ../table.FCStd>#Group [Link.Group002.Link017.Part001.Body013.Binder007.]
  EdgeTolerance = 1e-06
  FillStyle = 0
  Fuse = false
  MakeFace = true
  MergeEdges = true
  OffsetFill = false
  OffsetIntersection = false
  OffsetJoinType = 0
  OffsetOpenResult = false
  Outline = false
  PartialLoad = false
  Relative = true
  SplitEdges = false
  Support = -> [Body012[Pad033.Face5]]
  TightBound = false
  TreeRank = 527
  _Version = 8
FEATURE [Sketcher::SketchObject] Sketch093
  ArcFitTolerance = 1e-06
  AttachmentSupport = -> [YZ_Plane013]
  ExternalBSplineMaxDegree = 5
  ExternalBSplineTolerance = 0.0001
  ExternalGeometry = -> [Binder007]
  FullyConstrained = true
  InternalTolerance = 1e-06
  MakeInternals = true
  MapMode = 5
  Placement = pos=(0,0,0) rot=(0.57735,0.57735,0.57735;2.0944rad)
  Support = -> [YZ_Plane013]
  TreeRank = 528
  sketch-geometry (9):
    g0: ArcOfCircle CenterX=9.4e-13 CenterY=-1.741e-13 CenterZ=0 NormalX=0 NormalY=0 NormalZ=1 AngleXU=0 Radius=5.45 StartAngle=1.48033 EndAngle=4.80286
    g1: LineSegment StartX=0.492368 StartY=5.42771 StartZ=0 EndX=21.9657 EndY=3.47979 EndZ=0
    g2: LineSegment StartX=0.492368 StartY=-5.42771 StartZ=0 EndX=21.9657 EndY=-3.47979 EndZ=0
    g3: Circle CenterX=21.65 CenterY=7.1251e-12 CenterZ=0 NormalX=0 NormalY=0 NormalZ=1 AngleXU=0 Radius=1.6
    g4: ArcOfCircle CenterX=21.65 CenterY=7.1251e-12 CenterZ=0 NormalX=0 NormalY=0 NormalZ=1 AngleXU=0 Radius=3.49408 StartAngle=4.80286 EndAngle=7.76352
    g5: LineSegment [constr] StartX=16.4114 StartY=3.98364 StartZ=0 EndX=16.2307 EndY=1.99182 EndZ=0
    g6: GeomPoint [constr] X=18.05 Y=0 Z=0
    g7: GeomPoint [constr] X=20.05 Y=-6.448e-13 Z=0
    g8: Circle CenterX=9.4e-13 CenterY=-1.741e-13 CenterZ=0 NormalX=0 NormalY=0 NormalZ=1 AngleXU=0 Radius=1.25
  constraints (20):
    c: Coincident(g0,g-1)
    c: Diameter(g3) = 3.2
    c: Coincident(g4,g3)
    c: Coincident(g4,g2)
    c: Tangent(g1,g0) = 1.5708
    c: Tangent(g2,g0) = -1.5708
    c: Symmetric(g1,g2,g-1)
    c: PointOnObject(g5,g1)
    c: Perpendicular(g1,g5)
    c: Distance(g5) = 2
    c: Parallel(g-3,g1)
    c: PointOnObject(g7,g3)
    c: PointOnObject(g6,g-1)
    c: PointOnObject(g6,g-4)
    c: PointOnObject(g7,g-1)
    c: DistanceX(g6,g7) = 2
    c: Tangent(g4,g1) = 1.5708
    c: Coincident(g5,g-4)
    c: Coincident(g8,g0)
    c: Diameter(g8) = 2.5
FEATURE [PartDesign::Pad] Pad034
  AddSubType = 0
  AlongSketchNormal = false
  AutoTaperInnerAngle = true
  CheckUpToFaceLimits = true
  ClaimChildren = false
  Direction = (1,-2e-16,3e-16)
  Fit = 0
  FitJoin = 0
  InnerFit = 0
  InnerFitJoin = 0
  Length = 4
  Length2 = 100
  Linearize = true
  NewSolid = false
  Profile = -> Sketch093
  Refine = true
  Suppress = false
  TaperInnerAngle = 0
  TaperInnerAngleRev = 0
  TreeRank = 529
  Type = 0
  _ProfileBasedVersion = 1
FEATURE [Sketcher::SketchObject] Sketch094
  ArcFitTolerance = 1e-06
  AttachmentSupport = -> [Binder007]
  ExternalBSplineMaxDegree = 5
  ExternalBSplineTolerance = 0.0001
  ExternalGeometry = -> [Binder007]
  FullyConstrained = true
  InternalTolerance = 1e-06
  MakeInternals = true
  MapMode = 5
  Placement = pos=(2,-4e-16,4e-16) rot=(0.57735,0.57735,0.57735;2.0944rad)
  Support = -> [Binder007]
  TreeRank = 530
FEATURE [PartDesign::Pocket] Pocket035
  AddSubType = 1
  AutoTaperInnerAngle = true
  BaseFeature = -> Pad034
  CheckUpToFaceLimits = true
  ClaimChildren = false
  Fit = 0
  FitJoin = 0
  InnerFit = 0
  InnerFitJoin = 0
  Length = 2
  Length2 = 100
  Linearize = true
  NewSolid = false
  Profile = -> Sketch094
  Refine = true
  Suppress = false
  TaperAngle = 3
  TaperInnerAngle = -3
  TaperInnerAngleRev = 0
  TreeRank = 531
  Type = 0
  _ProfileBasedVersion = 1
  _Version = 1
FEATURE [Sketcher::SketchObject] Sketch095
  ArcFitTolerance = 1e-06
  AttachmentSupport = -> [Pocket035]
  ExternalBSplineMaxDegree = 5
  ExternalBSplineTolerance = 0.0001
  FullyConstrained = true
  InternalTolerance = 1e-06
  MakeInternals = true
  MapMode = 5
  Placement = pos=(4,-9e-16,9e-16) rot=(0.57735,0.57735,0.57735;2.0944rad)
  Support = -> [Pocket035]
  TreeRank = 532
  sketch-geometry (1):
    g0: Circle CenterX=0 CenterY=0 CenterZ=0 NormalX=0 NormalY=0 NormalZ=1 AngleXU=0 Radius=2.25
  constraints (2):
    c: Coincident(g0,g-1)
    c: Diameter(g0) = 4.5
FEATURE [PartDesign::Pocket] Pocket036
  AddSubType = 1
  AutoTaperInnerAngle = true
  BaseFeature = -> Pocket035
  CheckUpToFaceLimits = true
  ClaimChildren = false
  Fit = 0
  FitJoin = 0
  InnerFit = 0
  InnerFitJoin = 0
  Length = 1.5
  Length2 = 100
  Linearize = true
  NewSolid = false
  Profile = -> Sketch095
  Refine = true
  Suppress = false
  TaperInnerAngle = 0
  TaperInnerAngleRev = 0
  TreeRank = 533
  Type = 0
  _ProfileBasedVersion = 1
  _Version = 1
FEATURE [Sketcher::SketchObject] Sketch096
  ArcFitTolerance = 1e-06
  AttachmentSupport = -> [YZ_Plane013]
  ExternalBSplineMaxDegree = 5
  ExternalBSplineTolerance = 0.0001
  FullyConstrained = true
  InternalTolerance = 1e-06
  MakeInternals = true
  MapMode = 5
  Placement = pos=(0,0,0) rot=(0.57735,0.57735,0.57735;2.0944rad)
  Support = -> [YZ_Plane013]
  TreeRank = 534
  sketch-geometry (1):
    g0: Circle CenterX=14.8 CenterY=0 CenterZ=0 NormalX=0 NormalY=0 NormalZ=1 AngleXU=0 Radius=1.1
  constraints (3):
    c: PointOnObject(g0,g-1)
    c: DistanceX(g-1,g0) = 14.8
    c: Diameter(g0) = 2.2
FEATURE [PartDesign::Pocket] Pocket037
  AddSubType = 1
  AutoTaperInnerAngle = true
  BaseFeature = -> Pocket036
  CheckUpToFaceLimits = true
  ClaimChildren = false
  Fit = 0
  FitJoin = 0
  InnerFit = 0
  InnerFitJoin = 0
  Length = 5
  Length2 = 100
  Linearize = true
  NewSolid = false
  Profile = -> Sketch096
  Refine = true
  Reversed = true
  Suppress = false
  TaperInnerAngle = 0
  TaperInnerAngleRev = 0
  TreeRank = 535
  Type = 0
  _ProfileBasedVersion = 1
  _Version = 1
FEATURE [PartDesign::Chamfer] Chamfer028
  AddSubType = 0
  Angle = 45
  Base = -> Pocket037 [Edge20]
  BaseFeature = -> Pocket037
  ChamferType = 0
  FlipDirection = false
  NewSolid = false
  Refine = true
  Size = 1.49
  Size2 = 1
  SupportTransform = false
  Suppress = false
  TreeRank = 536
FEATURE [PartDesign::Chamfer] Chamfer029
  AddSubType = 0
  Angle = 45
  Base = -> Chamfer028 [Edge6,Edge7,Edge5,Edge21,Edge26]
  BaseFeature = -> Chamfer028
  ChamferType = 0
  FlipDirection = false
  NewSolid = false
  Refine = true
  Size = 0.4
  Size2 = 1
  SupportTransform = false
  Suppress = false
  TreeRank = 537
FEATURE [PartDesign::Body] Body013  label="BigServoArm"
  AutoGroupSolids = false
  ClaimAllChildren = false
  ExportMode = 0
  Group = -> [Binder007,Sketch093,Pad034,Sketch094,Pocket035,Sketch095,Pocket036,Sketch096,Pocket037,Chamfer028,Chamfer029]
  Origin = -> Origin015
  SingleSolid = true
  Tip = -> Chamfer029
  TreeRank = 522
  _ExportChildren = -> [Binder007,Pad034,Pocket035,Pocket036,Pocket037,Chamfer028,Chamfer029]
  _GroupVersion = 1
FEATURE [Sketcher::SketchObject] Sketch097
  ArcFitTolerance = 1e-06
  AttachmentSupport = -> [YZ_Plane015]
  ExternalBSplineMaxDegree = 5
  ExternalBSplineTolerance = 0.0001
  FullyConstrained = true
  InternalTolerance = 1e-06
  MakeInternals = true
  MapMode = 5
  Placement = pos=(0,0,0) rot=(0.57735,0.57735,0.57735;2.0944rad)
  Support = -> [YZ_Plane015]
  TreeRank = 563
  sketch-geometry (9):
    g0: ArcOfCircle CenterX=-1.065e-12 CenterY=-8.642e-13 CenterZ=0 NormalX=0 NormalY=0 NormalZ=1 AngleXU=0 Radius=3.5 StartAngle=1.5708 EndAngle=4.71239
    g1: ArcOfCircle CenterX=32 CenterY=-2.3876e-12 CenterZ=0 NormalX=0 NormalY=0 NormalZ=1 AngleXU=0 Radius=3.5 StartAngle=4.71239 EndAngle=7.85398
    g2: LineSegment StartX=-4.15056e-11 StartY=-3.5 StartZ=0 EndX=32 EndY=-3.5 EndZ=0
    g3: LineSegment StartX=32 StartY=3.5 StartZ=0 EndX=3.90088e-11 EndY=3.5 EndZ=0
    g4: Circle CenterX=-1.065e-12 CenterY=-8.642e-13 CenterZ=0 NormalX=0 NormalY=0 NormalZ=1 AngleXU=0 Radius=1.6
    g5: ArcOfCircle CenterX=32 CenterY=-2.3876e-12 CenterZ=0 NormalX=0 NormalY=0 NormalZ=1 AngleXU=0 Radius=1.6 StartAngle=4.71239 EndAngle=7.85398
    g6: ArcOfCircle CenterX=27 CenterY=-2.2926e-12 CenterZ=0 NormalX=0 NormalY=0 NormalZ=1 AngleXU=0 Radius=1.6 StartAngle=1.5708 EndAngle=4.71239
    g7: LineSegment StartX=32 StartY=1.6 StartZ=0 EndX=27 EndY=1.6 EndZ=0
    g8: LineSegment StartX=27 StartY=-1.6 StartZ=0 EndX=32 EndY=-1.6 EndZ=0
  constraints (20):
    c: Tangent(g0,g2) = -1.5708
    c: Tangent(g2,g1) = -1.5708
    c: Tangent(g1,g3) = -1.5708
    c: Tangent(g3,g0) = -1.5708
    c: Equal(g0,g1)
    c: Coincident(g0,g-1)
    c: PointOnObject(g1,g-1)
    c: DistanceX(g0,g1) = 32
    c: Diameter(g1) = 7
    c: Coincident(g4,g0)
    c: Diameter(g4) = 3.2
    c: Tangent(g5,g7) = -1.5708
    c: Tangent(g7,g6) = -1.5708
    c: Tangent(g6,g8) = -1.5708
    c: Tangent(g8,g5) = -1.5708
    c: Equal(g5,g6)
    c: Coincident(g5,g1)
    c: PointOnObject(g6,g-1)
    c: Equal(g5,g4)
    c: DistanceX(g6,g1) = 5
FEATURE [PartDesign::Pad] Pad035
  AddSubType = 0
  AlongSketchNormal = false
  AutoTaperInnerAngle = true
  CheckUpToFaceLimits = true
  ClaimChildren = false
  Direction = (1,-2e-16,3e-16)
  Fit = 0
  FitJoin = 0
  InnerFit = 0
  InnerFitJoin = 0
  Length = 3
  Length2 = 100
  Linearize = true
  NewSolid = false
  Profile = -> Sketch097
  Refine = true
  Reversed = true
  Suppress = false
  TaperInnerAngle = 0
  TaperInnerAngleRev = 0
  TreeRank = 564
  Type = 0
  _ProfileBasedVersion = 1
FEATURE [PartDesign::Body] Body014  label="ArmLink"
  AutoGroupSolids = false
  ClaimAllChildren = false
  ExportMode = 0
  Group = -> [Sketch097,Pad035]
  Origin = -> Origin017
  Placement = pos=(5.3e-15,21.65,6.0174e-12) rot=(1,0,0;4.88692rad)
  SingleSolid = true
  Tip = -> Pad035
  TreeRank = 562
  _ExportChildren = -> [Pad035]
  _GroupVersion = 1
FEATURE [App::Part] Part001  label="EnsembleServoArm"
  ClaimAllChildren = false
  ExportMode = 1
  Group = -> [Body012,Body013,Body014]
  Origin = -> Origin016
  Placement = pos=(15.7,12.1227,220.996) rot=(0,0,1;0rad)
  TreeRank = 540
  _ExportChildren = -> [Body012,Body013,Body014]
  _GroupVersion = 1
FEATURE [App::Part] Part002  label="EnsembleServo"
  ClaimAllChildren = false
  ExportMode = 1
  Group = -> [Part001]
  Origin = -> Origin018
  Placement = pos=(-7.4,-2.86102e-07,-2.84e-14) rot=(0,0,1;0rad)
  TreeRank = 567
  _ExportChildren = -> [Part001]
  _GroupVersion = 1
FEATURE [TechDraw::DrawSVGTemplate] Template003
  Height = 210
  Orientation = 1
  TreeRank = 569
  Width = 297
FEATURE [TechDraw::DrawProjGroupItem] ProjItem003  label="Front003"
  CoarseView = false
  Direction = (1,0,0)
  Focus = 100
  HardHidden = false
  IsoCount = 0
  IsoHidden = false
  IsoVisible = false
  LockPosition = true
  Perspective = false
  Rotation = 0
  RotationVector = (0,-1,0)
  ScaleType = 2
  SeamHidden = false
  SeamVisible = true
  SmoothHidden = false
  SmoothVisible = true
  Source = -> [Pad035]
  TreeRank = 572
  Type = 0
  X = 0
  XDirection = (0,-1,0)
  Y = 0
FEATURE [TechDraw::DrawProjGroup] ProjGroup003
  Anchor = -> ProjItem003
  AutoDistribute = true
  LockPosition = false
  ProjectionType = 0
  Rotation = 0
  ScaleType = 0
  Source = -> [Pad035]
  TreeRank = 573
  Views = -> [ProjItem003]
  X = 22.5
  Y = 202.899
  spacingX = 15
  spacingY = 15
FEATURE [TechDraw::DrawPage] Page003  label="ArmLink3mmLaser"
  KeepUpdated = true
  NextBalloonIndex = 1
  ProjectionType = 0
  Template = -> Template003
  TreeRank = 570
  Views = -> [ProjGroup003]
FEATURE [Mesh::Feature] vacuum_ball_TubeInterne  label="vacuum-ball-TubeInterne"
  TreeRank = 576
FEATURE [PartDesign::Chamfer] Chamfer014
  AddSubType = 0
  Angle = 45
  Base = -> Pocket019 [Edge236]
  BaseFeature = -> Pocket019
  ChamferType = 0
  FlipDirection = false
  NewSolid = false
  Refine = true
  Size = 3
  Size2 = 1
  SupportTransform = false
  Suppress = false
  TreeRank = 577
FEATURE [PartDesign::Chamfer] Chamfer
  AddSubType = 0
  Angle = 45
  Base = -> Chamfer014 [Face34]
  BaseFeature = -> Chamfer014
  ChamferType = 0
  FlipDirection = false
  NewSolid = false
  Refine = true
  Size = 0.4
  Size2 = 1
  SupportTransform = false
  Suppress = false
  TreeRank = 578
FEATURE [PartDesign::Body] Body006  label="TubeInterne"
  AutoGroupSolids = false
  ClaimAllChildren = false
  ExportMode = 0
  Group = -> [Sketch040,Import001,Sketch041,Pipe014,Sketch042,Sketch044,Pipe015,Pipe016,Loft,Sketch045,Pad011,Sketch046,Sketch047,Pocket013,Pocket014,Sketch048,Pocket015,Sketch049,Pad012,Sketch050,Pocket016,Sketch051,Pocket017,Sketch053,Pocket018,Sketch054,Pad013,Pipe017,Pipe018,Sketch055,Pad014,Sketch056,Pad015,Sketch057,Pad016,Fillet005,Chamfer011,Fillet006,Sketch058,Pocket019,Chamfer014,Chamfer]
  Origin = -> Origin008
  Tip = -> Chamfer
  TreeRank = 224
  _ExportChildren = -> [Import001,Pipe014,Pipe015,Pipe016,Loft,Pad011,Pocket013,Pocket014,Pocket015,Pad012,Pocket016,Pocket017,Pocket018,Pad013,Pipe017,Pipe018,Pad014,Pad015,Pad016,Fillet005,Chamfer011,Fillet006,Pocket019,Chamfer014,Chamfer]
  _GroupVersion = 1
FEATURE [PartDesign::SubShapeBinder] Binder  label="ProjectionTubeInterne"
  BindCopyOnChange = 0
  BindMode = 0
  ClaimChildren = false
  Context = -> Part [Body005.Binder.]
  EdgeTolerance = 1e-06
  FillStyle = 0
  Fuse = false
  MakeFace = true
  MergeEdges = true
  OffsetFill = false
  OffsetIntersection = false
  OffsetJoinType = 0
  OffsetOpenResult = false
  Outline = false
  PartialLoad = false
  Relative = true
  SplitEdges = false
  Support = -> [Body006[Pocket019.Face37]]
  TightBound = false
  TreeRank = 579
  _Version = 8
FEATURE [Sketcher::SketchObject] Sketch
  ArcFitTolerance = 1e-06
  AttachmentSupport = -> [XZ_Plane005]
  ExternalBSplineMaxDegree = 5
  ExternalBSplineTolerance = 0.0001
  ExternalGeometry = -> [Binder]
  FullyConstrained = true
  InternalTolerance = 1e-06
  MakeInternals = true
  MapMode = 5
  Placement = pos=(0,0,0) rot=(0,0.707107,0.707107;3.14159rad)
  Support = -> [XZ_Plane005]
  TreeRank = 281
  sketch-geometry (10):
    g0: Circle CenterX=-18 CenterY=278 CenterZ=0 NormalX=0 NormalY=0 NormalZ=1 AngleXU=0 Radius=1.6
    g1: Circle CenterX=-18 CenterY=242 CenterZ=0 NormalX=0 NormalY=0 NormalZ=1 AngleXU=0 Radius=1.6
    g2: Circle CenterX=18 CenterY=242 CenterZ=0 NormalX=0 NormalY=0 NormalZ=1 AngleXU=0 Radius=1.6
    g3: Circle CenterX=18 CenterY=278 CenterZ=0 NormalX=0 NormalY=0 NormalZ=1 AngleXU=0 Radius=1.6
    g4: Circle CenterX=25 CenterY=207.978 CenterZ=0 NormalX=0 NormalY=0 NormalZ=1 AngleXU=0 Radius=1.6
    g5: Circle CenterX=-25 CenterY=207.978 CenterZ=0 NormalX=0 NormalY=0 NormalZ=1 AngleXU=0 Radius=1.6
    g6: Circle CenterX=-25 CenterY=135.065 CenterZ=0 NormalX=0 NormalY=0 NormalZ=1 AngleXU=0 Radius=1.6
    g7: Circle CenterX=25 CenterY=135.065 CenterZ=0 NormalX=0 NormalY=0 NormalZ=1 AngleXU=0 Radius=1.6
    g8: ArcOfCircle CenterX=-13.9999 CenterY=185.327 CenterZ=0 NormalX=0 NormalY=0 NormalZ=1 AngleXU=0 Radius=14.2206 StartAngle=1.5708 EndAngle=4.71238
    g9: ArcOfCircle CenterX=14 CenterY=185.327 CenterZ=0 NormalX=0 NormalY=0 NormalZ=1 AngleXU=0 Radius=14.2206 StartAngle=4.71239 EndAngle=7.85398
  constraints (21):
    c: Coincident(g0,g-5)
    c: Coincident(g1,g-4)
    c: Coincident(g2,g-6)
    c: Coincident(g3,g-3)
    c: Coincident(g4,g-13)
    c: Coincident(g5,g-12)
    c: Coincident(g6,g-15)
    c: Coincident(g7,g-14)
    c: Equal(g7,g6)
    c: Equal(g7,g5)
    c: Equal(g7,g4)
    c: Equal(g7,g2)
    c: Equal(g7,g1)
    c: Equal(g7,g0)
    c: Equal(g7,g3)
    c: Diameter(g7) = 3.2
    c: Coincident(g8,g-10)
    c: Coincident(g8,g-11)
    c: Coincident(g9,g-11)
    c: Tangent(g9,g-9) = 1.5708
    c: Tangent(g8,g-9)
FEATURE [PartDesign::Pocket] Pocket
  AddSubType = 1
  AutoTaperInnerAngle = true
  BaseFeature = -> Chamfer010
  CheckUpToFaceLimits = true
  ClaimChildren = false
  Fit = 0
  FitJoin = 0
  InnerFit = 0
  InnerFitJoin = 0
  Length = 5
  Length2 = 100
  Linearize = true
  NewSolid = false
  Profile = -> Sketch
  Refine = true
  Suppress = false
  TaperInnerAngle = 0
  TaperInnerAngleRev = 0
  TreeRank = 282
  Type = 1
  _ProfileBasedVersion = 1
  _Version = 1
FEATURE [PartDesign::Pocket] Pocket027
  AddSubType = 1
  AutoTaperInnerAngle = true
  BaseFeature = -> Pocket
  CheckUpToFaceLimits = true
  ClaimChildren = false
  Fit = 0
  FitJoin = 0
  InnerFit = 0
  InnerFitJoin = 0
  Length = 5
  Length2 = 100
  Linearize = true
  NewSolid = false
  Profile = -> Sketch079
  Refine = true
  Suppress = false
  TaperInnerAngle = 0
  TaperInnerAngleRev = 0
  TreeRank = 415
  Type = 1
  _ProfileBasedVersion = 1
  _Version = 1
FEATURE [Sketcher::SketchObject] Sketch080
  ArcFitTolerance = 1e-06
  AttachmentSupport = -> [XZ_Plane005]
  ExternalBSplineMaxDegree = 5
  ExternalBSplineTolerance = 0.0001
  ExternalGeometry = -> [Pocket027]
  FullyConstrained = true
  InternalTolerance = 1e-06
  MakeInternals = true
  MapMode = 5
  Placement = pos=(0,0,0) rot=(0,0.707107,0.707107;3.14159rad)
  Support = -> [XZ_Plane005]
  TreeRank = 416
  sketch-geometry (7):
    g0: ArcOfCircle CenterX=40.9 CenterY=226.699 CenterZ=0 NormalX=0 NormalY=0 NormalZ=1 AngleXU=0 Radius=1.8 StartAngle=5.23599 EndAngle=8.37758
    g1: ArcOfCircle CenterX=24.1 CenterY=217 CenterZ=0 NormalX=0 NormalY=0 NormalZ=1 AngleXU=0 Radius=1.8 StartAngle=2.0944 EndAngle=5.23599
    g2: LineSegment StartX=40 StartY=228.258 StartZ=0 EndX=23.2 EndY=218.559 EndZ=0
    g3: LineSegment [constr] StartX=25 StartY=215.441 StartZ=0 EndX=41.8 EndY=225.141 EndZ=0
    g4: ArcOfCircle CenterX=28.701 CenterY=217.578 CenterZ=0 NormalX=0 NormalY=0 NormalZ=1 AngleXU=0 Radius=1.5 StartAngle=0.523599 EndAngle=3.66519
    g5: LineSegment StartX=25 StartY=215.441 StartZ=0 EndX=27.4019 EndY=216.828 EndZ=0
    g6: LineSegment StartX=30 StartY=218.328 StartZ=0 EndX=41.8 EndY=225.141 EndZ=0
  constraints (19):
    c: Tangent(g0,g2) = -1.5708
    c: Tangent(g2,g1) = -1.5708
    c: Tangent(g1,g3) = -1.5708
    c: Tangent(g3,g0) = -1.5708
    c: Equal(g0,g1)
    c: Radius(g0) = 1.8
    c: PointOnObject(g0,g-3)
    c: Angle(g3,g-3) = 1.0472
    c: DistanceX(g1,g0) = 15
    c: PointOnObject(g4,g3)
    c: PointOnObject(g4,g3)
    c: PointOnObject(g4,g3)
    c: Coincident(g5,g1)
    c: Coincident(g5,g4)
    c: Coincident(g6,g0)
    c: Coincident(g6,g4)
    c: Radius(g4) = 1.5
    c: DistanceX(g4,g0) = 10
    c: DistanceY(g1) = 217
FEATURE [PartDesign::Pocket] Pocket028
  AddSubType = 1
  AutoTaperInnerAngle = true
  BaseFeature = -> Pocket027
  CheckUpToFaceLimits = true
  ClaimChildren = false
  Fit = 0
  FitJoin = 0
  InnerFit = 0
  InnerFitJoin = 0
  Length = 5
  Length2 = 100
  Linearize = true
  NewSolid = false
  Profile = -> Sketch080
  Refine = true
  Suppress = false
  TaperInnerAngle = 0
  TaperInnerAngleRev = 0
  TreeRank = 417
  Type = 1
  _ProfileBasedVersion = 1
  _Version = 1
FEATURE [PartDesign::Fillet] Fillet011
  AddSubType = 0
  Base = -> Pocket028 [Edge151,Edge150]
  BaseFeature = -> Pocket028
  NewSolid = false
  Radius = 1
  Refine = true
  SupportTransform = false
  Suppress = false
  TreeRank = 418
FEATURE [PartDesign::Chamfer] Chamfer023
  AddSubType = 0
  Angle = 45
  Base = -> Fillet011 [Edge73,Edge78]
  BaseFeature = -> Fillet011
  ChamferType = 0
  FlipDirection = false
  NewSolid = false
  Refine = true
  Size = 1
  Size2 = 1
  SupportTransform = false
  Suppress = false
  TreeRank = 419
FEATURE [Sketcher::SketchObject] Sketch081
  ArcFitTolerance = 1e-06
  AttachmentSupport = -> [XZ_Plane005]
  ExternalBSplineMaxDegree = 5
  ExternalBSplineTolerance = 0.0001
  ExternalGeometry = -> [Chamfer023]
  FullyConstrained = true
  InternalTolerance = 1e-06
  MakeInternals = true
  MapMode = 5
  Placement = pos=(0,0,0) rot=(0,0.707107,0.707107;3.14159rad)
  Support = -> [XZ_Plane005]
  TreeRank = 420
  sketch-geometry (4):
    g0: LineSegment StartX=-30 StartY=215 StartZ=0 EndX=-30 EndY=243 EndZ=0
    g1: LineSegment StartX=-30 StartY=243 StartZ=0 EndX=-15 EndY=230 EndZ=0
    g2: LineSegment StartX=-15 StartY=230 StartZ=0 EndX=-15 EndY=215 EndZ=0
    g3: LineSegment StartX=-30 StartY=215 StartZ=0 EndX=-15 EndY=215 EndZ=0
  constraints (12):
    c: Vertical(g0)
    c: Coincident(g1,g0)
    c: Vertical(g2)
    c: Coincident(g3,g0)
    c: Coincident(g3,g2)
    c: Horizontal(g3)
    c: DistanceX(g-3,g0) = 10
    c: DistanceY(g0) = 215
    c: Coincident(g1,g2)
    c: DistanceX(g2) = -15
    c: DistanceY(g1) = 230
    c: DistanceY(g0) = 243
FEATURE [PartDesign::Pocket] Pocket029
  AddSubType = 1
  AutoTaperInnerAngle = true
  BaseFeature = -> Chamfer023
  CheckUpToFaceLimits = true
  ClaimChildren = false
  Fit = 0
  FitJoin = 0
  InnerFit = 0
  InnerFitJoin = 0
  Length = 5
  Length2 = 100
  Linearize = true
  NewSolid = false
  Profile = -> Sketch081
  Refine = true
  Suppress = false
  TaperInnerAngle = 0
  TaperInnerAngleRev = 0
  TreeRank = 421
  Type = 1
  _ProfileBasedVersion = 1
  _Version = 1
FEATURE [PartDesign::Fillet] Fillet012
  AddSubType = 0
  Base = -> Pocket029 [Edge195,Edge197,Edge201,Edge199]
  BaseFeature = -> Pocket029
  NewSolid = false
  Radius = 3
  Refine = true
  SupportTransform = false
  Suppress = false
  TreeRank = 422
FEATURE [PartDesign::Body] Body005  label="CarterVac"
  AutoGroupSolids = false
  ClaimAllChildren = false
  ExportMode = 0
  Group = -> [Sketch038,Binder,Pad010,Sketch039,Pocket012,Chamfer009,Chamfer010,Sketch,Pocket,Sketch079,Pocket027,Sketch080,Pocket028,Fillet011,Chamfer023,Sketch081,Pocket029,Fillet012]
  Origin = -> Origin006
  SingleSolid = true
  Tip = -> Fillet012
  TreeRank = 204
  _ExportChildren = -> [Binder,Pad010,Pocket012,Chamfer009,Chamfer010,Pocket,Pocket027,Pocket028,Fillet011,Chamfer023,Pocket029,Fillet012]
  _GroupVersion = 1
FEATURE [TechDraw::DrawProjGroupItem] ProjItem002  label="Front002"
  CoarseView = false
  Direction = (0,1,0)
  Focus = 100
  HardHidden = false
  IsoCount = 0
  IsoHidden = false
  IsoVisible = false
  LockPosition = true
  Perspective = false
  Rotation = 0
  RotationVector = (0,0,-1)
  ScaleType = 2
  SeamHidden = false
  SeamVisible = true
  SmoothHidden = false
  SmoothVisible = true
  Source = -> [Fillet012]
  TreeRank = 427
  Type = 0
  X = 0
  XDirection = (0,0,-1)
  Y = 0
FEATURE [TechDraw::DrawProjGroup] ProjGroup002
  Anchor = -> ProjItem002
  AutoDistribute = true
  LockPosition = false
  ProjectionType = 0
  Rotation = 0
  ScaleType = 0
  Source = -> [Fillet012]
  TreeRank = 428
  Views = -> [ProjItem002]
  X = 103.437
  Y = 166.765
  spacingX = 15
  spacingY = 15
FEATURE [TechDraw::DrawPage] Page002  label="CarterVac3mmLaser"
  KeepUpdated = true
  NextBalloonIndex = 1
  ProjectionType = 0
  Template = -> Template002
  TreeRank = 425
  Views = -> [ProjGroup002]
FEATURE [App::DocumentObjectGroup] Group001  label="Laser"
  ClaimAllChildren = true
  ExportMode = 1
  Group = -> [Page,Page001,Page002,Page003]
  TreeRank = 574
  _GroupVersion = 1
FEATURE [App::Part] Part  label="BallActionneur"
  ClaimAllChildren = false
  ExportMode = 1
  Group = -> [Body005,Body006,Body,Body007,Body008,Body009,Body010,Body011,Part002,Group002]
  Origin = -> Origin003
  TreeRank = 98
  _ExportChildren = -> [Body005,Body006,Body,Group002]
  _GroupVersion = 1
FEATURE [PartDesign::Body] Body011  label="Trappe"
  AutoGroupSolids = false
  ClaimAllChildren = false
  ExportMode = 0
  Group = -> [Binder004,Binder005,Binder006,DatumPlane,Sketch086,Pad029,Sketch087,Pocket032,Pad030,Fillet018,Sketch088,Pocket033,Fillet019,Chamfer025,Sketch089,Pocket034,Chamfer026,Fillet020,Sketch090,Import004,Pad031,Fillet021,Fillet022,Fillet023,Chamfer027,Group]
  Origin = -> Origin013
  Placement = pos=(0,28.35,194.28) rot=(0,0,1;0rad)
  SingleSolid = true
  Tip = -> Chamfer027
  TreeRank = 453
  _ExportChildren = -> [Binder004,Binder005,Binder006,DatumPlane,Pad029,Pocket032,Pad030,Fillet018,Pocket033,Fillet019,Chamfer025,Pocket034,Chamfer026,Fillet020,Import004,Pad031,Fillet021,Fillet022,Fillet023,Chamfer027,Group]
  _GroupVersion = 1
FEATURE [PartDesign::AuxGroup] Group
  TreeRank = 479
FEATURE [App::DocumentObjectGroup] Group002  label="Ok"
  ClaimAllChildren = true
  ExportMode = 1
  Group = -> [Body007,Body008,Body009,Body010,Body011,Part002]
  TreeRank = 575
  _GroupVersion = 1
